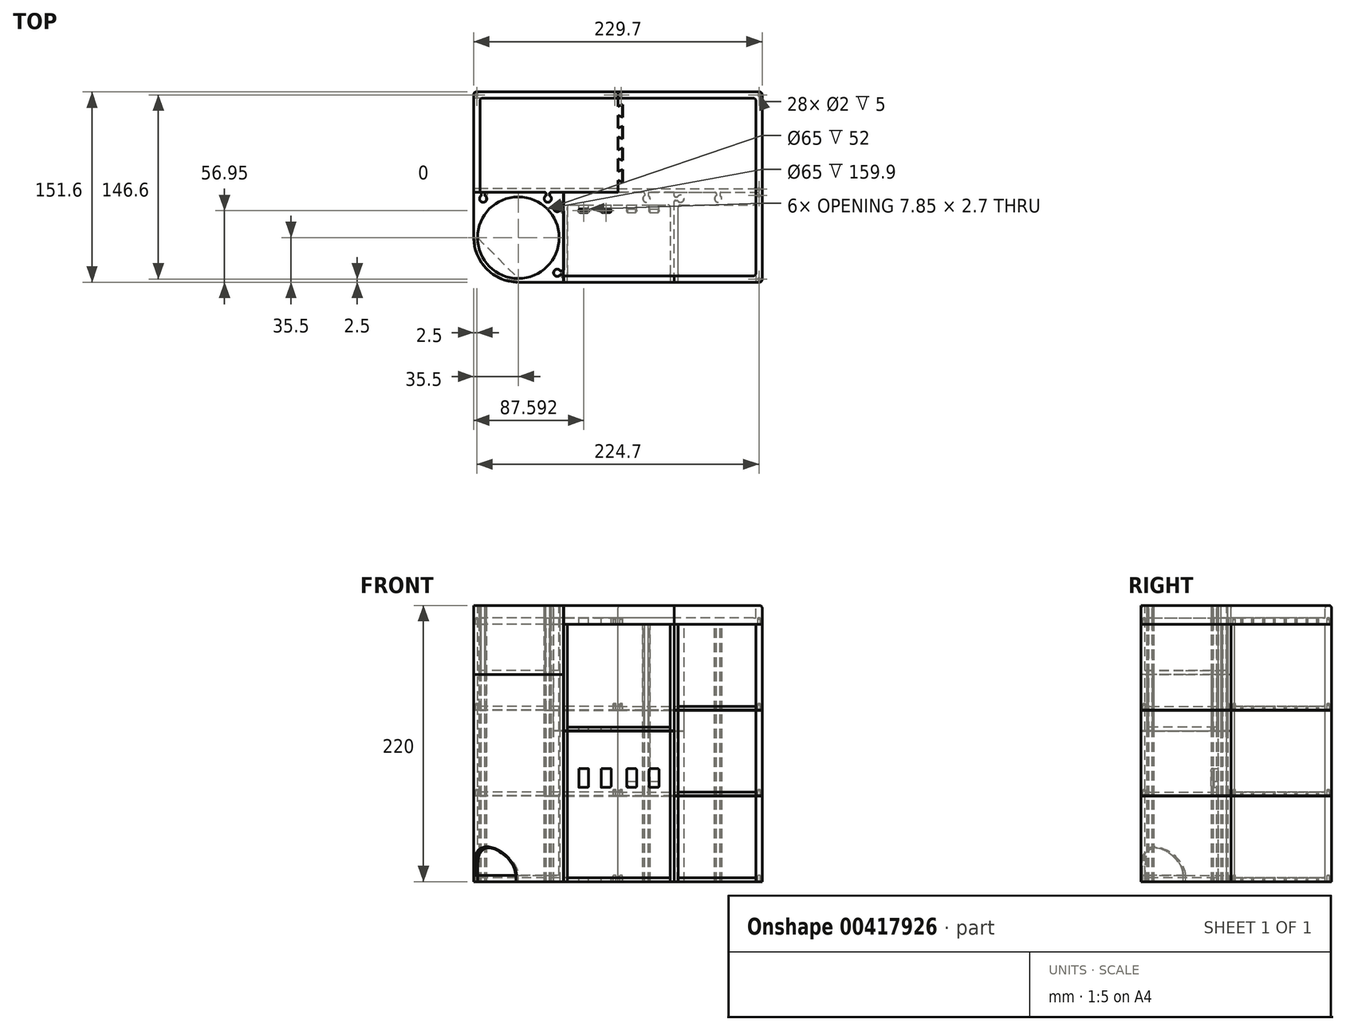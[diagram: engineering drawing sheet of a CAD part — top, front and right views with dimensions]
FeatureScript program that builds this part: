
annotation { "Feature Type Name" : "Feature", "Feature Type Description" : "" }
export const myFeature = defineFeature(function(context is Context, id is Id, definition is map)
    precondition{}
    {
        {
            var Q0;
            Q0=qCreatedBy(makeId("Top.planeOp"),FACE);
            var sketch = newSketch(context, id + "F0", { "sketchPlane" : qUnion([Q0])});
            skLineSegment(sketch, "E0", {"start": v(-2, 0) * mm, "end": v(-114.85, 0) * mm});
            skLineSegment(sketch, "E1", {"start": v(-114.85, 0) * mm, "end": v(-114.95, 0) * mm, "construction": true});
            skLineSegment(sketch, "E2", {"start": v(-114.95, 0) * mm, "end": v(-227.7, 0) * mm});
            skLineSegment(sketch, "E3", {"start": v(0, -2) * mm, "end": v(0, -80) * mm});
            skLineSegment(sketch, "E4", {"start": v(0, -80) * mm, "end": v(0, -80.1) * mm});
            skLineSegment(sketch, "E5", {"start": v(0, -80.1) * mm, "end": v(0, -149.6) * mm});
            skLineSegment(sketch, "E6", {"start": v(-2, -151.6) * mm, "end": v(-70, -151.6) * mm});
            skLineSegment(sketch, "E7", {"start": v(-70, -151.6) * mm, "end": v(-70.1, -151.6) * mm});
            skLineSegment(sketch, "E8", {"start": v(-70.1, -151.6) * mm, "end": v(-158.1, -151.6) * mm});
            skLineSegment(sketch, "E9", {"start": v(-158.1, -151.6) * mm, "end": v(-158.1, -146.26) * mm});
            skLineSegment(sketch, "E10", {"start": v(-70, -151.6) * mm, "end": v(-70, -87.55) * mm});
            skLineSegment(sketch, "E11", {"start": v(-70, -80.1) * mm, "end": v(-37.5, -80.1) * mm});
            skLineSegment(sketch, "E12", {"start": v(-70.1, -151.6) * mm, "end": v(-70.1, -87.21) * mm});
            skLineSegment(sketch, "E13", {"start": v(-70.1, -80.1) * mm, "end": v(-89.6, -80.1) * mm});
            skLineSegment(sketch, "E14", {"start": v(-70.1, -151.6) * mm, "end": v(-70, -151.6) * mm});
            skLineSegment(sketch, "E15", {"start": v(-158.1, -151.6) * mm, "end": v(-158.2, -151.6) * mm, "construction": true});
            skLineSegment(sketch, "E16", {"start": v(-158.2, -151.6) * mm, "end": v(-194.2, -151.6) * mm});
            skLineSegment(sketch, "E17", {"start": v(-194.2, -151.6) * mm, "end": v(-194.2, -116.1) * mm, "construction": true});
            skLineSegment(sketch, "E18", {"start": v(-194.2, -116.1) * mm, "end": v(-229.7, -116.1) * mm, "construction": true});
            skCircle(sketch, "E19", {"center": v(-194.2, -116.1) * mm, "radius": 32.5 * mm});
            skArc(sketch, "E20", {"start": v(-229.7, -116.1) * mm, "mid": v(-219.3, -141.2) * mm, "end": v(-194.2, -151.6) * mm});
            skLineSegment(sketch, "E21", {"start": v(-194.2, -151.6) * mm, "end": v(-194.2, -148.6) * mm});
            skLineSegment(sketch, "E22", {"start": v(-229.7, -116.1) * mm, "end": v(-226.7, -116.1) * mm});
            skLineSegment(sketch, "E23", {"start": v(-226.7, -116.1) * mm, "end": v(-194.2, -148.6) * mm});
            skLineSegment(sketch, "E24", {"start": v(-229.7, -116.1) * mm, "end": v(-229.7, -80.1) * mm});
            skLineSegment(sketch, "E25", {"start": v(-229.7, -80.1) * mm, "end": v(-224.7, -80.1) * mm});
            skLineSegment(sketch, "E26", {"start": v(-158.2, -80.1) * mm, "end": v(-158.2, -90.1) * mm});
            skLineSegment(sketch, "E27", {"start": v(-229.7, -80.1) * mm, "end": v(-229.7, -80) * mm, "construction": true});
            skLineSegment(sketch, "E28", {"start": v(-229.7, -80) * mm, "end": v(-229.7, -2) * mm});
            skLineSegment(sketch, "E29", {"start": v(-114.85, -80) * mm, "end": v(-94.26, -80) * mm});
            skLineSegment(sketch, "E30", {"start": v(-220.7, -81.1) * mm, "end": v(-220.7, -82.6) * mm});
            skLineSegment(sketch, "E31", {"start": v(-220.7, -82.6) * mm, "end": v(-222.2, -82.6) * mm, "construction": true});
            skLineSegment(sketch, "E32", {"start": v(-222.2, -82.6) * mm, "end": v(-222.2, -80.1) * mm, "construction": true});
            skLineSegment(sketch, "E33", {"start": v(-222.2, -82.6) * mm, "end": v(-222.2, -85.1) * mm, "construction": true});
            skArc(sketch, "E34", {"start": v(-220.7, -82.6) * mm, "mid": v(-219.4, -85.88) * mm, "end": v(-222.2, -88.02) * mm});
            skArc(sketch, "E35", {"start": v(-220.7, -81.1) * mm, "mid": v(-220.4, -80.4) * mm, "end": v(-219.7, -80.1) * mm});
            skPoint(sketch, "E36.orphan", {"position": v(-220.7, -80.1) * mm});
            skArc(sketch, "E37.MirrorCS", {"start": v(-223.7, -81.1) * mm, "mid": v(-224, -80.4) * mm, "end": v(-224.7, -80.1) * mm});
            skLineSegment(sketch, "E38.MirrorCS", {"start": v(-223.7, -81.1) * mm, "end": v(-223.7, -82.6) * mm});
            skArc(sketch, "E39.MirrorCS", {"start": v(-223.7, -82.6) * mm, "mid": v(-225, -85.88) * mm, "end": v(-222.2, -88.02) * mm});
            skArc(sketch, "E40.0", {"start": v(-223.55, -81.1) * mm, "mid": v(-223.78, -80.42) * mm, "end": v(-224.36, -80) * mm});
            skLineSegment(sketch, "E40.1", {"start": v(-223.55, -81.1) * mm, "end": v(-223.55, -82.69) * mm});
            skArc(sketch, "E40.2", {"start": v(-220.85, -81.1) * mm, "mid": v(-220.62, -80.42) * mm, "end": v(-220.04, -80) * mm});
            skLineSegment(sketch, "E40.3", {"start": v(-220.85, -81.1) * mm, "end": v(-220.85, -82.69) * mm});
            skArc(sketch, "E40.4", {"start": v(-220.85, -82.69) * mm, "mid": v(-219.52, -85.8) * mm, "end": v(-222.2, -87.87) * mm});
            skArc(sketch, "E40.5", {"start": v(-223.55, -82.69) * mm, "mid": v(-224.88, -85.8) * mm, "end": v(-222.2, -87.87) * mm});
            skLineSegment(sketch, "E41.trimOffspring", {"start": v(-224.13, -80.1) * mm, "end": v(-220.27, -80.1) * mm, "construction": true});
            skLineSegment(sketch, "E42.trimOffspring", {"start": v(-219.7, -80.1) * mm, "end": v(-173.2, -80.1) * mm});
            skLineSegment(sketch, "E43.trimOffspring", {"start": v(-224.36, -80) * mm, "end": v(-229.7, -80) * mm});
            skLineSegment(sketch, "E44", {"start": v(-169.2, -81.1) * mm, "end": v(-169.2, -82.6) * mm});
            skLineSegment(sketch, "E45", {"start": v(-169.2, -82.6) * mm, "end": v(-170.7, -82.6) * mm, "construction": true});
            skLineSegment(sketch, "E46", {"start": v(-170.7, -82.6) * mm, "end": v(-170.7, -80.1) * mm, "construction": true});
            skLineSegment(sketch, "E47", {"start": v(-170.7, -82.6) * mm, "end": v(-170.7, -85.1) * mm, "construction": true});
            skArc(sketch, "E48", {"start": v(-169.2, -82.6) * mm, "mid": v(-167.9, -85.88) * mm, "end": v(-170.7, -88.02) * mm});
            skArc(sketch, "E49", {"start": v(-169.2, -81.1) * mm, "mid": v(-168.9, -80.4) * mm, "end": v(-168.2, -80.1) * mm});
            skPoint(sketch, "E50.orphan", {"position": v(-169.2, -80.1) * mm});
            skArc(sketch, "E51.MirrorCS", {"start": v(-172.2, -81.1) * mm, "mid": v(-172.5, -80.4) * mm, "end": v(-173.2, -80.1) * mm});
            skLineSegment(sketch, "E52.MirrorCS", {"start": v(-172.2, -81.1) * mm, "end": v(-172.2, -82.6) * mm});
            skArc(sketch, "E53.MirrorCS", {"start": v(-172.2, -82.6) * mm, "mid": v(-173.5, -85.88) * mm, "end": v(-170.7, -88.02) * mm});
            skArc(sketch, "E54.0", {"start": v(-172.05, -81.1) * mm, "mid": v(-172.28, -80.42) * mm, "end": v(-172.86, -80) * mm});
            skLineSegment(sketch, "E54.1", {"start": v(-172.05, -81.1) * mm, "end": v(-172.05, -82.69) * mm});
            skArc(sketch, "E54.2", {"start": v(-169.35, -81.1) * mm, "mid": v(-169.12, -80.42) * mm, "end": v(-168.54, -80) * mm});
            skLineSegment(sketch, "E54.3", {"start": v(-169.35, -81.1) * mm, "end": v(-169.35, -82.69) * mm});
            skArc(sketch, "E54.4", {"start": v(-169.35, -82.69) * mm, "mid": v(-168.02, -85.8) * mm, "end": v(-170.7, -87.87) * mm});
            skArc(sketch, "E54.5", {"start": v(-172.05, -82.69) * mm, "mid": v(-173.38, -85.8) * mm, "end": v(-170.7, -87.87) * mm});
            skLineSegment(sketch, "E55.trimOffspring", {"start": v(-172.63, -80.1) * mm, "end": v(-168.77, -80.1) * mm, "construction": true});
            skLineSegment(sketch, "E56.trimOffspring", {"start": v(-168.2, -80.1) * mm, "end": v(-158.2, -80.1) * mm});
            skLineSegment(sketch, "E57.trimOffspring", {"start": v(-172.86, -80) * mm, "end": v(-220.04, -80) * mm});
            skLineSegment(sketch, "E58", {"start": v(-159.2, -94.1) * mm, "end": v(-160.7, -94.1) * mm});
            skLineSegment(sketch, "E59", {"start": v(-160.7, -94.1) * mm, "end": v(-160.7, -92.6) * mm, "construction": true});
            skLineSegment(sketch, "E60", {"start": v(-160.7, -92.6) * mm, "end": v(-158.2, -92.6) * mm, "construction": true});
            skLineSegment(sketch, "E61", {"start": v(-160.7, -92.6) * mm, "end": v(-163.2, -92.6) * mm, "construction": true});
            skArc(sketch, "E62", {"start": v(-160.7, -94.1) * mm, "mid": v(-163.98, -95.4) * mm, "end": v(-166.12, -92.6) * mm});
            skArc(sketch, "E63", {"start": v(-159.2, -94.1) * mm, "mid": v(-158.5, -94.4) * mm, "end": v(-158.2, -95.1) * mm});
            skPoint(sketch, "E64.orphan", {"position": v(-158.2, -94.1) * mm});
            skArc(sketch, "E65.MirrorCS", {"start": v(-159.2, -91.1) * mm, "mid": v(-158.5, -90.8) * mm, "end": v(-158.2, -90.1) * mm});
            skLineSegment(sketch, "E66.MirrorCS", {"start": v(-159.2, -91.1) * mm, "end": v(-160.7, -91.1) * mm});
            skArc(sketch, "E67.MirrorCS", {"start": v(-160.7, -91.1) * mm, "mid": v(-163.98, -89.8) * mm, "end": v(-166.12, -92.6) * mm});
            skArc(sketch, "E68.0", {"start": v(-159.2, -91.25) * mm, "mid": v(-158.52, -91.02) * mm, "end": v(-158.1, -90.44) * mm});
            skLineSegment(sketch, "E68.1", {"start": v(-159.2, -91.25) * mm, "end": v(-160.79, -91.25) * mm});
            skArc(sketch, "E68.2", {"start": v(-159.2, -93.95) * mm, "mid": v(-158.52, -94.18) * mm, "end": v(-158.1, -94.76) * mm});
            skLineSegment(sketch, "E68.3", {"start": v(-159.2, -93.95) * mm, "end": v(-160.79, -93.95) * mm});
            skArc(sketch, "E68.4", {"start": v(-160.79, -93.95) * mm, "mid": v(-163.9, -95.28) * mm, "end": v(-165.97, -92.6) * mm});
            skArc(sketch, "E68.5", {"start": v(-160.79, -91.25) * mm, "mid": v(-163.9, -89.92) * mm, "end": v(-165.97, -92.6) * mm});
            skLineSegment(sketch, "E69.trimOffspring", {"start": v(-158.2, -90.67) * mm, "end": v(-158.2, -94.53) * mm, "construction": true});
            skLineSegment(sketch, "E70.trimOffspring", {"start": v(-158.1, -90.44) * mm, "end": v(-158.1, -80.1) * mm});
            skLineSegment(sketch, "E71.trimOffspring", {"start": v(-158.2, -95.1) * mm, "end": v(-158.2, -141.6) * mm});
            skLineSegment(sketch, "E72", {"start": v(-159.2, -145.6) * mm, "end": v(-160.7, -145.6) * mm});
            skLineSegment(sketch, "E73", {"start": v(-160.7, -145.6) * mm, "end": v(-160.7, -144.1) * mm, "construction": true});
            skLineSegment(sketch, "E74", {"start": v(-160.7, -144.1) * mm, "end": v(-158.2, -144.1) * mm, "construction": true});
            skLineSegment(sketch, "E75", {"start": v(-160.7, -144.1) * mm, "end": v(-163.2, -144.1) * mm, "construction": true});
            skArc(sketch, "E76", {"start": v(-160.7, -145.6) * mm, "mid": v(-163.98, -146.9) * mm, "end": v(-166.12, -144.1) * mm});
            skArc(sketch, "E77", {"start": v(-159.2, -145.6) * mm, "mid": v(-158.5, -145.9) * mm, "end": v(-158.2, -146.6) * mm});
            skPoint(sketch, "E78.orphan", {"position": v(-158.2, -145.6) * mm});
            skArc(sketch, "E79.MirrorCS", {"start": v(-159.2, -142.6) * mm, "mid": v(-158.5, -142.3) * mm, "end": v(-158.2, -141.6) * mm});
            skLineSegment(sketch, "E80.MirrorCS", {"start": v(-159.2, -142.6) * mm, "end": v(-160.7, -142.6) * mm});
            skArc(sketch, "E81.MirrorCS", {"start": v(-160.7, -142.6) * mm, "mid": v(-163.98, -141.3) * mm, "end": v(-166.12, -144.1) * mm});
            skArc(sketch, "E82.0", {"start": v(-159.2, -142.75) * mm, "mid": v(-158.52, -142.52) * mm, "end": v(-158.1, -141.94) * mm});
            skLineSegment(sketch, "E82.1", {"start": v(-159.2, -142.75) * mm, "end": v(-160.79, -142.75) * mm});
            skArc(sketch, "E82.2", {"start": v(-159.2, -145.45) * mm, "mid": v(-158.52, -145.68) * mm, "end": v(-158.1, -146.26) * mm});
            skLineSegment(sketch, "E82.3", {"start": v(-159.2, -145.45) * mm, "end": v(-160.79, -145.45) * mm});
            skArc(sketch, "E82.4", {"start": v(-160.79, -145.45) * mm, "mid": v(-163.9, -146.78) * mm, "end": v(-165.97, -144.1) * mm});
            skArc(sketch, "E82.5", {"start": v(-160.79, -142.75) * mm, "mid": v(-163.9, -141.42) * mm, "end": v(-165.97, -144.1) * mm});
            skLineSegment(sketch, "E83.trimOffspring", {"start": v(-158.2, -142.17) * mm, "end": v(-158.2, -146.03) * mm, "construction": true});
            skLineSegment(sketch, "E84.trimOffspring", {"start": v(-158.1, -141.94) * mm, "end": v(-158.1, -94.76) * mm});
            skLineSegment(sketch, "E85.trimOffspring", {"start": v(-158.2, -146.6) * mm, "end": v(-158.2, -151.6) * mm});
            skLineSegment(sketch, "E86.0", {"start": v(-114.95, -5) * mm, "end": v(-117.95, -5) * mm});
            skLineSegment(sketch, "E87.0", {"start": v(-111.85, -5) * mm, "end": v(-114.85, -5) * mm});
            skLineSegment(sketch, "E88.0", {"start": v(-5, -77) * mm, "end": v(-5, -80) * mm});
            skLineSegment(sketch, "E89.0", {"start": v(-114.85, -77) * mm, "end": v(-7, -77) * mm});
            skLineSegment(sketch, "E90", {"start": v(-158.1, -80.1) * mm, "end": v(-158.1, -80) * mm});
            skLineSegment(sketch, "E91", {"start": v(-114.85, 0) * mm, "end": v(-114.85, -5) * mm});
            skLineSegment(sketch, "E92", {"start": v(-114.95, 0) * mm, "end": v(-114.95, -5) * mm});
            skLineSegment(sketch, "E93", {"start": v(-168.54, -80) * mm, "end": v(-158.2, -80) * mm});
            skLineSegment(sketch, "E94", {"start": v(-158.1, -80) * mm, "end": v(-114.95, -80) * mm});
            skLineSegment(sketch, "E95", {"start": v(-114.85, -77) * mm, "end": v(-114.85, -80) * mm});
            skLineSegment(sketch, "E96", {"start": v(-114.95, -77) * mm, "end": v(-222.7, -77) * mm});
            skLineSegment(sketch, "E97", {"start": v(-114.85, -5) * mm, "end": v(-114.85, -11.47) * mm});
            skLineSegment(sketch, "E98", {"start": v(-114.85, -11.47) * mm, "end": v(-111.1, -10.1) * mm});
            skLineSegment(sketch, "E99", {"start": v(-111.1, -10.1) * mm, "end": v(-111.1, -20.1) * mm});
            skLineSegment(sketch, "E100", {"start": v(-111.1, -20.1) * mm, "end": v(-114.85, -18.74) * mm});
            skLineSegment(sketch, "E101", {"start": v(-114.85, -18.74) * mm, "end": v(-114.85, -28.74) * mm});
            skLineSegment(sketch, "E102", {"start": v(-114.85, -28.74) * mm, "end": v(-111.1, -27.37) * mm});
            skLineSegment(sketch, "E103", {"start": v(-111.1, -27.37) * mm, "end": v(-111.1, -37.37) * mm});
            skLineSegment(sketch, "E104", {"start": v(-111.1, -37.37) * mm, "end": v(-114.85, -36) * mm});
            skLineSegment(sketch, "E105", {"start": v(-114.85, -36) * mm, "end": v(-114.85, -46) * mm});
            skLineSegment(sketch, "E106", {"start": v(-114.85, -46) * mm, "end": v(-111.1, -44.63) * mm});
            skLineSegment(sketch, "E107", {"start": v(-111.1, -44.63) * mm, "end": v(-111.1, -54.63) * mm});
            skLineSegment(sketch, "E108", {"start": v(-111.1, -54.63) * mm, "end": v(-114.85, -53.26) * mm});
            skLineSegment(sketch, "E109", {"start": v(-114.85, -53.26) * mm, "end": v(-114.85, -63.26) * mm});
            skLineSegment(sketch, "E110", {"start": v(-114.85, -63.26) * mm, "end": v(-111.1, -61.9) * mm});
            skLineSegment(sketch, "E111", {"start": v(-111.1, -61.9) * mm, "end": v(-111.1, -71.9) * mm});
            skLineSegment(sketch, "E112", {"start": v(-111.1, -71.9) * mm, "end": v(-114.85, -70.53) * mm});
            skLineSegment(sketch, "E113", {"start": v(-114.85, -70.53) * mm, "end": v(-114.85, -77) * mm});
            skLineSegment(sketch, "E114.0", {"start": v(-114.95, -70.38) * mm, "end": v(-114.95, -77) * mm});
            skLineSegment(sketch, "E114.1", {"start": v(-111.2, -71.75) * mm, "end": v(-114.95, -70.38) * mm});
            skLineSegment(sketch, "E114.2", {"start": v(-111.2, -62.04) * mm, "end": v(-111.2, -71.75) * mm});
            skLineSegment(sketch, "E114.3", {"start": v(-114.95, -63.4) * mm, "end": v(-111.2, -62.04) * mm});
            skLineSegment(sketch, "E114.4", {"start": v(-114.95, -53.12) * mm, "end": v(-114.95, -63.4) * mm});
            skLineSegment(sketch, "E114.5", {"start": v(-111.2, -54.49) * mm, "end": v(-114.95, -53.12) * mm});
            skLineSegment(sketch, "E114.6", {"start": v(-111.2, -44.77) * mm, "end": v(-111.2, -54.49) * mm});
            skLineSegment(sketch, "E114.7", {"start": v(-111.2, -19.96) * mm, "end": v(-114.95, -18.6) * mm});
            skLineSegment(sketch, "E114.8", {"start": v(-111.2, -10.25) * mm, "end": v(-111.2, -19.96) * mm});
            skLineSegment(sketch, "E114.9", {"start": v(-114.95, -11.62) * mm, "end": v(-111.2, -10.25) * mm});
            skLineSegment(sketch, "E114.10", {"start": v(-114.95, -5) * mm, "end": v(-114.95, -11.62) * mm});
            skLineSegment(sketch, "E114.11", {"start": v(-114.95, -18.6) * mm, "end": v(-114.95, -28.88) * mm});
            skLineSegment(sketch, "E114.12", {"start": v(-114.95, -28.88) * mm, "end": v(-111.2, -27.51) * mm});
            skLineSegment(sketch, "E114.13", {"start": v(-111.2, -27.51) * mm, "end": v(-111.2, -37.23) * mm});
            skLineSegment(sketch, "E114.14", {"start": v(-111.2, -37.23) * mm, "end": v(-114.95, -35.86) * mm});
            skLineSegment(sketch, "E114.15", {"start": v(-114.95, -35.86) * mm, "end": v(-114.95, -46.14) * mm});
            skLineSegment(sketch, "E114.16", {"start": v(-114.95, -46.14) * mm, "end": v(-111.2, -44.77) * mm});
            skLineSegment(sketch, "E115", {"start": v(-158.2, -80) * mm, "end": v(-158.1, -80) * mm});
            skLineSegment(sketch, "E116.1", {"start": v(-153.1, -90) * mm, "end": v(-75.1, -90) * mm});
            skLineSegment(sketch, "E117.bottom", {"start": v(-107.02, -93.3) * mm, "end": v(-100.87, -93.3) * mm});
            skLineSegment(sketch, "E117.top", {"start": v(-107.02, -96) * mm, "end": v(-100.87, -96) * mm});
            skLineSegment(sketch, "E117.left", {"start": v(-107.87, -94.15) * mm, "end": v(-107.87, -95.15) * mm});
            skLineSegment(sketch, "E117.right", {"start": v(-100.02, -94.15) * mm, "end": v(-100.02, -95.15) * mm});
            skPoint(sketch, "E118.visualSharp", {"position": v(-100.02, -96) * mm});
            skArc(sketch, "E118.filletArc", {"start": v(-100.87, -96) * mm, "mid": v(-100.27, -95.75) * mm, "end": v(-100.02, -95.15) * mm});
            skPoint(sketch, "E119.visualSharp", {"position": v(-100.02, -93.3) * mm});
            skArc(sketch, "E119.filletArc", {"start": v(-100.02, -94.15) * mm, "mid": v(-100.27, -93.55) * mm, "end": v(-100.87, -93.3) * mm});
            skPoint(sketch, "E120.visualSharp", {"position": v(-107.87, -93.3) * mm});
            skArc(sketch, "E120.filletArc", {"start": v(-107.02, -93.3) * mm, "mid": v(-107.62, -93.55) * mm, "end": v(-107.87, -94.15) * mm});
            skPoint(sketch, "E121.visualSharp", {"position": v(-107.87, -96) * mm});
            skArc(sketch, "E121.filletArc", {"start": v(-107.87, -95.15) * mm, "mid": v(-107.62, -95.75) * mm, "end": v(-107.02, -96) * mm});
            skLineSegment(sketch, "E122.bottom", {"start": v(-89.17, -93.3) * mm, "end": v(-83.02, -93.3) * mm});
            skLineSegment(sketch, "E122.top", {"start": v(-89.17, -96) * mm, "end": v(-83.02, -96) * mm});
            skLineSegment(sketch, "E122.left", {"start": v(-90.02, -94.15) * mm, "end": v(-90.02, -95.15) * mm});
            skLineSegment(sketch, "E122.right", {"start": v(-82.17, -94.15) * mm, "end": v(-82.17, -95.15) * mm});
            skPoint(sketch, "E123.visualSharp", {"position": v(-82.17, -96) * mm});
            skArc(sketch, "E123.filletArc", {"start": v(-83.02, -96) * mm, "mid": v(-82.42, -95.75) * mm, "end": v(-82.17, -95.15) * mm});
            skPoint(sketch, "E124.visualSharp", {"position": v(-82.17, -93.3) * mm});
            skArc(sketch, "E124.filletArc", {"start": v(-82.17, -94.15) * mm, "mid": v(-82.42, -93.55) * mm, "end": v(-83.02, -93.3) * mm});
            skPoint(sketch, "E125.visualSharp", {"position": v(-90.02, -93.3) * mm});
            skArc(sketch, "E125.filletArc", {"start": v(-89.17, -93.3) * mm, "mid": v(-89.77, -93.55) * mm, "end": v(-90.02, -94.15) * mm});
            skPoint(sketch, "E126.visualSharp", {"position": v(-90.02, -96) * mm});
            skArc(sketch, "E126.filletArc", {"start": v(-90.02, -95.15) * mm, "mid": v(-89.77, -95.75) * mm, "end": v(-89.17, -96) * mm});
            skLineSegment(sketch, "E127", {"start": v(-107.87, -94.15) * mm, "end": v(-107.87, -90) * mm});
            skLineSegment(sketch, "E128", {"start": v(-100.02, -94.15) * mm, "end": v(-100.02, -90) * mm});
            skLineSegment(sketch, "E129", {"start": v(-90.02, -94.15) * mm, "end": v(-90.02, -90) * mm});
            skLineSegment(sketch, "E130", {"start": v(-82.17, -94.15) * mm, "end": v(-82.17, -90) * mm});
            skLineSegment(sketch, "E131", {"start": v(-155.1, -92) * mm, "end": v(-155.1, -144.6) * mm});
            skLineSegment(sketch, "E132", {"start": v(-73.1, -92) * mm, "end": v(-73.1, -144.6) * mm});
            skLineSegment(sketch, "E133", {"start": v(-114.1, -90) * mm, "end": v(-114.1, -102.22) * mm, "construction": true});
            skLineSegment(sketch, "E134.MirrorCS", {"start": v(-120.33, -94.15) * mm, "end": v(-120.33, -90) * mm});
            skArc(sketch, "E135.MirrorCS", {"start": v(-121.18, -93.3) * mm, "mid": v(-120.58, -93.55) * mm, "end": v(-120.33, -94.15) * mm});
            skLineSegment(sketch, "E136.MirrorCS", {"start": v(-120.33, -94.15) * mm, "end": v(-120.33, -95.15) * mm});
            skArc(sketch, "E137.MirrorCS", {"start": v(-120.33, -95.15) * mm, "mid": v(-120.58, -95.75) * mm, "end": v(-121.18, -96) * mm});
            skLineSegment(sketch, "E138.MirrorCS", {"start": v(-121.18, -96) * mm, "end": v(-127.33, -96) * mm});
            skLineSegment(sketch, "E139.MirrorCS", {"start": v(-121.18, -93.3) * mm, "end": v(-127.33, -93.3) * mm});
            skArc(sketch, "E140.MirrorCS", {"start": v(-128.18, -94.15) * mm, "mid": v(-127.93, -93.55) * mm, "end": v(-127.33, -93.3) * mm});
            skLineSegment(sketch, "E141.MirrorCS", {"start": v(-128.18, -94.15) * mm, "end": v(-128.18, -95.15) * mm});
            skArc(sketch, "E142.MirrorCS", {"start": v(-127.33, -96) * mm, "mid": v(-127.93, -95.75) * mm, "end": v(-128.18, -95.15) * mm});
            skLineSegment(sketch, "E143.MirrorCS", {"start": v(-128.18, -94.15) * mm, "end": v(-128.18, -90) * mm});
            skLineSegment(sketch, "E144.MirrorCS", {"start": v(-138.18, -94.15) * mm, "end": v(-138.18, -90) * mm});
            skArc(sketch, "E145.MirrorCS", {"start": v(-139.03, -93.3) * mm, "mid": v(-138.43, -93.55) * mm, "end": v(-138.18, -94.15) * mm});
            skLineSegment(sketch, "E146.MirrorCS", {"start": v(-138.18, -94.15) * mm, "end": v(-138.18, -95.15) * mm});
            skArc(sketch, "E147.MirrorCS", {"start": v(-138.18, -95.15) * mm, "mid": v(-138.43, -95.75) * mm, "end": v(-139.03, -96) * mm});
            skLineSegment(sketch, "E148.MirrorCS", {"start": v(-139.03, -96) * mm, "end": v(-145.18, -96) * mm});
            skArc(sketch, "E149.MirrorCS", {"start": v(-145.18, -96) * mm, "mid": v(-145.78, -95.75) * mm, "end": v(-146.03, -95.15) * mm});
            skLineSegment(sketch, "E150.MirrorCS", {"start": v(-146.03, -94.15) * mm, "end": v(-146.03, -95.15) * mm});
            skArc(sketch, "E151.MirrorCS", {"start": v(-146.03, -94.15) * mm, "mid": v(-145.78, -93.55) * mm, "end": v(-145.18, -93.3) * mm});
            skLineSegment(sketch, "E152.MirrorCS", {"start": v(-139.03, -93.3) * mm, "end": v(-145.18, -93.3) * mm});
            skLineSegment(sketch, "E153.MirrorCS", {"start": v(-146.03, -94.15) * mm, "end": v(-146.03, -90) * mm});
            skLineSegment(sketch, "E154", {"start": v(-114.95, -77) * mm, "end": v(-114.95, -80) * mm});
            skLineSegment(sketch, "E155.0", {"start": v(-5, -80.1) * mm, "end": v(-5, -83.1) * mm});
            skLineSegment(sketch, "E156.trimOffspring", {"start": v(-7, -146.6) * mm, "end": v(-65, -146.6) * mm});
            skLineSegment(sketch, "E157.0", {"start": v(-65, -90) * mm, "end": v(-7, -90) * mm});
            skLineSegment(sketch, "E158.0", {"start": v(-70.1, -146.6) * mm, "end": v(-71.1, -146.6) * mm});
            skLineSegment(sketch, "E159", {"start": v(-69, -83.55) * mm, "end": v(-67.5, -83.55) * mm});
            skLineSegment(sketch, "E160", {"start": v(-67.5, -83.55) * mm, "end": v(-67.5, -85.05) * mm, "construction": true});
            skLineSegment(sketch, "E161", {"start": v(-67.5, -85.05) * mm, "end": v(-70, -85.05) * mm, "construction": true});
            skLineSegment(sketch, "E162", {"start": v(-67.5, -85.05) * mm, "end": v(-65, -85.05) * mm, "construction": true});
            skArc(sketch, "E163", {"start": v(-67.5, -83.55) * mm, "mid": v(-64.22, -82.24) * mm, "end": v(-62.08, -85.05) * mm});
            skArc(sketch, "E164", {"start": v(-69, -83.55) * mm, "mid": v(-69.7, -83.26) * mm, "end": v(-70, -82.55) * mm});
            skPoint(sketch, "E165.orphan", {"position": v(-70, -83.55) * mm});
            skArc(sketch, "E166.MirrorCS", {"start": v(-69, -86.55) * mm, "mid": v(-69.7, -86.84) * mm, "end": v(-70, -87.55) * mm});
            skLineSegment(sketch, "E167.MirrorCS", {"start": v(-69, -86.55) * mm, "end": v(-67.5, -86.55) * mm});
            skArc(sketch, "E168.MirrorCS", {"start": v(-67.5, -86.55) * mm, "mid": v(-64.22, -87.86) * mm, "end": v(-62.08, -85.05) * mm});
            skArc(sketch, "E169.0", {"start": v(-69, -86.4) * mm, "mid": v(-69.68, -86.63) * mm, "end": v(-70.1, -87.21) * mm});
            skLineSegment(sketch, "E169.1", {"start": v(-69, -86.4) * mm, "end": v(-67.41, -86.4) * mm});
            skArc(sketch, "E169.2", {"start": v(-69, -83.7) * mm, "mid": v(-69.68, -83.47) * mm, "end": v(-70.1, -82.89) * mm});
            skLineSegment(sketch, "E169.3", {"start": v(-69, -83.7) * mm, "end": v(-67.41, -83.7) * mm});
            skArc(sketch, "E169.4", {"start": v(-67.41, -83.7) * mm, "mid": v(-64.3, -82.37) * mm, "end": v(-62.23, -85.05) * mm});
            skArc(sketch, "E169.5", {"start": v(-67.41, -86.4) * mm, "mid": v(-64.3, -87.73) * mm, "end": v(-62.23, -85.05) * mm});
            skLineSegment(sketch, "E170.trimOffspring", {"start": v(-70.1, -82.89) * mm, "end": v(-70.1, -80.1) * mm});
            skLineSegment(sketch, "E171.trimOffspring", {"start": v(-70, -86.98) * mm, "end": v(-70, -83.12) * mm, "construction": true});
            skLineSegment(sketch, "E172.trimOffspring", {"start": v(-70, -82.55) * mm, "end": v(-70, -80.1) * mm});
            skLineSegment(sketch, "E173.trimOffspring", {"start": v(-67, -144.6) * mm, "end": v(-67, -92) * mm});
            skLineSegment(sketch, "E174.0", {"start": v(-224.7, -75) * mm, "end": v(-224.7, -7) * mm});
            skLineSegment(sketch, "E175", {"start": v(-33.5, -81.1) * mm, "end": v(-33.5, -82.6) * mm});
            skLineSegment(sketch, "E176", {"start": v(-33.5, -82.6) * mm, "end": v(-35, -82.6) * mm, "construction": true});
            skLineSegment(sketch, "E177", {"start": v(-35, -82.6) * mm, "end": v(-35, -80.1) * mm, "construction": true});
            skLineSegment(sketch, "E178", {"start": v(-35, -82.6) * mm, "end": v(-35, -85.1) * mm, "construction": true});
            skArc(sketch, "E179", {"start": v(-33.5, -82.6) * mm, "mid": v(-32.2, -85.88) * mm, "end": v(-35, -88.02) * mm});
            skArc(sketch, "E180", {"start": v(-33.5, -81.1) * mm, "mid": v(-33.2, -80.4) * mm, "end": v(-32.5, -80.1) * mm});
            skPoint(sketch, "E181.orphan", {"position": v(-33.5, -80.1) * mm});
            skArc(sketch, "E182.MirrorCS", {"start": v(-36.5, -81.1) * mm, "mid": v(-36.8, -80.4) * mm, "end": v(-37.5, -80.1) * mm});
            skLineSegment(sketch, "E183.MirrorCS", {"start": v(-36.5, -81.1) * mm, "end": v(-36.5, -82.6) * mm});
            skArc(sketch, "E184.MirrorCS", {"start": v(-36.5, -82.6) * mm, "mid": v(-37.8, -85.88) * mm, "end": v(-35, -88.02) * mm});
            skArc(sketch, "E185.0", {"start": v(-36.35, -81.1) * mm, "mid": v(-36.58, -80.42) * mm, "end": v(-37.16, -80) * mm});
            skLineSegment(sketch, "E185.1", {"start": v(-36.35, -81.1) * mm, "end": v(-36.35, -82.69) * mm});
            skArc(sketch, "E185.2", {"start": v(-33.65, -81.1) * mm, "mid": v(-33.42, -80.42) * mm, "end": v(-32.84, -80) * mm});
            skLineSegment(sketch, "E185.3", {"start": v(-33.65, -81.1) * mm, "end": v(-33.65, -82.69) * mm});
            skArc(sketch, "E185.4", {"start": v(-33.65, -82.69) * mm, "mid": v(-32.32, -85.8) * mm, "end": v(-35, -87.87) * mm});
            skArc(sketch, "E185.5", {"start": v(-36.35, -82.69) * mm, "mid": v(-37.68, -85.8) * mm, "end": v(-35, -87.87) * mm});
            skPoint(sketch, "E186", {"position": v(-35, -80.1) * mm});
            skPoint(sketch, "E187", {"position": v(-35, -80) * mm});
            skLineSegment(sketch, "E188.trimOffspring", {"start": v(-32.84, -80) * mm, "end": v(0, -80) * mm});
            skLineSegment(sketch, "E189.trimOffspring", {"start": v(-36.93, -80.1) * mm, "end": v(-33.07, -80.1) * mm, "construction": true});
            skLineSegment(sketch, "E190.trimOffspring", {"start": v(-32.5, -80.1) * mm, "end": v(0, -80.1) * mm});
            skLineSegment(sketch, "E191", {"start": v(-90.6, -81.1) * mm, "end": v(-90.6, -82.6) * mm});
            skLineSegment(sketch, "E192", {"start": v(-90.6, -82.6) * mm, "end": v(-92.1, -82.6) * mm, "construction": true});
            skLineSegment(sketch, "E193", {"start": v(-92.1, -82.6) * mm, "end": v(-92.1, -80.1) * mm, "construction": true});
            skLineSegment(sketch, "E194", {"start": v(-92.1, -82.6) * mm, "end": v(-92.1, -85.1) * mm, "construction": true});
            skArc(sketch, "E195", {"start": v(-90.6, -82.6) * mm, "mid": v(-89.3, -85.88) * mm, "end": v(-92.1, -88.02) * mm});
            skArc(sketch, "E196", {"start": v(-90.6, -81.1) * mm, "mid": v(-90.3, -80.4) * mm, "end": v(-89.6, -80.1) * mm});
            skPoint(sketch, "E197.orphan", {"position": v(-90.6, -80.1) * mm});
            skArc(sketch, "E198.MirrorCS", {"start": v(-93.6, -81.1) * mm, "mid": v(-93.9, -80.4) * mm, "end": v(-94.6, -80.1) * mm});
            skLineSegment(sketch, "E199.MirrorCS", {"start": v(-93.6, -81.1) * mm, "end": v(-93.6, -82.6) * mm});
            skArc(sketch, "E200.MirrorCS", {"start": v(-93.6, -82.6) * mm, "mid": v(-94.9, -85.88) * mm, "end": v(-92.1, -88.02) * mm});
            skArc(sketch, "E201.0", {"start": v(-93.45, -81.1) * mm, "mid": v(-93.68, -80.42) * mm, "end": v(-94.26, -80) * mm});
            skLineSegment(sketch, "E201.1", {"start": v(-93.45, -81.1) * mm, "end": v(-93.45, -82.69) * mm});
            skArc(sketch, "E201.2", {"start": v(-90.75, -81.1) * mm, "mid": v(-90.52, -80.42) * mm, "end": v(-89.94, -80) * mm});
            skLineSegment(sketch, "E201.3", {"start": v(-90.75, -81.1) * mm, "end": v(-90.75, -82.69) * mm});
            skArc(sketch, "E201.4", {"start": v(-90.75, -82.69) * mm, "mid": v(-89.42, -85.8) * mm, "end": v(-92.1, -87.87) * mm});
            skArc(sketch, "E201.5", {"start": v(-93.45, -82.69) * mm, "mid": v(-94.78, -85.8) * mm, "end": v(-92.1, -87.87) * mm});
            skPoint(sketch, "E202", {"position": v(-70.1, -80) * mm});
            skPoint(sketch, "E203", {"position": v(-92.1, -80.1) * mm});
            skLineSegment(sketch, "E204.trimOffspring", {"start": v(-89.94, -80) * mm, "end": v(-37.16, -80) * mm});
            skLineSegment(sketch, "E205.trimOffspring", {"start": v(-94.6, -80.1) * mm, "end": v(-158.1, -80.1) * mm});
            skLineSegment(sketch, "E206.trimOffspring", {"start": v(-90.17, -80.1) * mm, "end": v(-94.03, -80.1) * mm, "construction": true});
            skLineSegment(sketch, "E207", {"start": v(-224.7, -3) * mm, "end": v(-224.7, 0) * mm});
            skPoint(sketch, "E208", {"position": v(-227.2, 0) * mm});
            skCircle(sketch, "E209", {"center": v(-227.2, -2.5) * mm, "radius": 1 * mm});
            skPoint(sketch, "E209.centerSnap0", {"position": v(-224.7, -2.5) * mm});
            skPoint(sketch, "E210", {"position": v(-119.95, 0) * mm});
            skPoint(sketch, "E211", {"position": v(-109.85, 0) * mm});
            skPoint(sketch, "E212", {"position": v(-117.45, 0) * mm});
            skPoint(sketch, "E213", {"position": v(-112.35, 0) * mm});
            skLineSegment(sketch, "E214", {"start": v(-119.95, 0) * mm, "end": v(-119.95, -3) * mm});
            skLineSegment(sketch, "E215", {"start": v(-109.85, 0) * mm, "end": v(-109.85, -3) * mm});
            skCircle(sketch, "E216", {"center": v(-117.45, -2.5) * mm, "radius": 1 * mm});
            skCircle(sketch, "E217", {"center": v(-112.35, -2.5) * mm, "radius": 1 * mm});
            skCircle(sketch, "E218", {"center": v(-112.35, -2.5) * mm, "radius": 0.9 * mm});
            skCircle(sketch, "E219", {"center": v(-117.45, -2.5) * mm, "radius": 0.9 * mm});
            skCircle(sketch, "E220", {"center": v(-227.2, -2.5) * mm, "radius": 0.9 * mm});
            skLineSegment(sketch, "E221", {"start": v(-5, -3) * mm, "end": v(-5, 0) * mm});
            skLineSegment(sketch, "E222", {"start": v(-3, -5) * mm, "end": v(0, -5) * mm});
            skCircle(sketch, "E223", {"center": v(-2.5, -2.5) * mm, "radius": 1 * mm});
            skPoint(sketch, "E223.centerSnap0", {"position": v(-5, -2.5) * mm});
            skPoint(sketch, "E223.centerSnap1", {"position": v(-2.5, -5) * mm});
            skCircle(sketch, "E224", {"center": v(-2.5, -2.5) * mm, "radius": 0.9 * mm});
            skPoint(sketch, "E225", {"position": v(0, -77.5) * mm});
            skPoint(sketch, "E226", {"position": v(0, -75) * mm});
            skLineSegment(sketch, "E227", {"start": v(0, -75) * mm, "end": v(-3, -75) * mm});
            skCircle(sketch, "E228", {"center": v(-2.5, -77.5) * mm, "radius": 1 * mm});
            skPoint(sketch, "E228.centerSnap0", {"position": v(-2.5, -75) * mm});
            skCircle(sketch, "E229", {"center": v(-2.5, -77.5) * mm, "radius": 0.9 * mm});
            skPoint(sketch, "E230", {"position": v(0, -82.6) * mm});
            skPoint(sketch, "E231", {"position": v(0, -85.1) * mm});
            skLineSegment(sketch, "E232", {"start": v(0, -85.1) * mm, "end": v(-3, -85.1) * mm});
            skCircle(sketch, "E233", {"center": v(-2.5, -82.6) * mm, "radius": 1 * mm});
            skPoint(sketch, "E233.centerSnap0", {"position": v(-2.5, -85.1) * mm});
            skCircle(sketch, "E234", {"center": v(-2.5, -82.6) * mm, "radius": 0.9 * mm});
            skLineSegment(sketch, "E235", {"start": v(-3, -146.6) * mm, "end": v(0, -146.6) * mm});
            skLineSegment(sketch, "E236", {"start": v(-5, -148.6) * mm, "end": v(-5, -151.6) * mm});
            skCircle(sketch, "E237", {"center": v(-2.5, -149.1) * mm, "radius": 1 * mm});
            skPoint(sketch, "E237.centerSnap0", {"position": v(-5, -149.1) * mm});
            skPoint(sketch, "E237.centerSnap1", {"position": v(-2.5, -146.6) * mm});
            skCircle(sketch, "E238", {"center": v(-2.5, -149.1) * mm, "radius": 0.9 * mm});
            skLineSegment(sketch, "E239", {"start": v(-67, -148.6) * mm, "end": v(-67, -151.6) * mm});
            skLineSegment(sketch, "E240", {"start": v(-73.1, -148.6) * mm, "end": v(-73.1, -151.6) * mm});
            skLineSegment(sketch, "E241", {"start": v(-114.85, -80) * mm, "end": v(-114.85, -80.1) * mm});
            skLineSegment(sketch, "E242", {"start": v(-5, -80) * mm, "end": v(-5, -80.1) * mm});
            skLineSegment(sketch, "E243", {"start": v(-70.1, -146.6) * mm, "end": v(-70, -146.6) * mm});
            skPoint(sketch, "E244.visualSharp", {"position": v(0, 0) * mm});
            skArc(sketch, "E244.filletArc", {"start": v(0, -2) * mm, "mid": v(-0.59, -0.59) * mm, "end": v(-2, 0) * mm});
            skPoint(sketch, "E245.visualSharp", {"position": v(-5, -5) * mm});
            skArc(sketch, "E245.filletArc", {"start": v(-5, -7) * mm, "mid": v(-5.59, -5.59) * mm, "end": v(-7, -5) * mm});
            skPoint(sketch, "E246.visualSharp", {"position": v(-229.7, 0) * mm});
            skArc(sketch, "E246.filletArc", {"start": v(-227.7, 0) * mm, "mid": v(-229.11, -0.59) * mm, "end": v(-229.7, -2) * mm});
            skArc(sketch, "E247.filletArc", {"start": v(-222.7, -5) * mm, "mid": v(-224.11, -5.59) * mm, "end": v(-224.7, -7) * mm});
            skLineSegment(sketch, "E248", {"start": v(-226.7, -5) * mm, "end": v(-229.7, -5) * mm});
            skArc(sketch, "E249.filletArc", {"start": v(-224.7, -75) * mm, "mid": v(-224.11, -76.41) * mm, "end": v(-222.7, -77) * mm});
            skLineSegment(sketch, "E250", {"start": v(-229.7, -77) * mm, "end": v(-226.7, -77) * mm});
            skLineSegment(sketch, "E251", {"start": v(-224.7, -79) * mm, "end": v(-224.7, -80) * mm});
            skPoint(sketch, "E252.visualSharp", {"position": v(0, -151.6) * mm});
            skArc(sketch, "E252.filletArc", {"start": v(-2, -151.6) * mm, "mid": v(-0.59, -151.01) * mm, "end": v(0, -149.6) * mm});
            skPoint(sketch, "E253.visualSharp", {"position": v(-5, -146.6) * mm});
            skArc(sketch, "E253.filletArc", {"start": v(-7, -146.6) * mm, "mid": v(-5.59, -146.01) * mm, "end": v(-5, -144.6) * mm});
            skArc(sketch, "E254.filletArc", {"start": v(-3, -146.6) * mm, "mid": v(-4.41, -147.19) * mm, "end": v(-5, -148.6) * mm});
            skArc(sketch, "E255.filletArc", {"start": v(-5, -3) * mm, "mid": v(-4.41, -4.41) * mm, "end": v(-3, -5) * mm});
            skPoint(sketch, "E256.visualSharp", {"position": v(-224.7, -5) * mm});
            skArc(sketch, "E256.filletArc", {"start": v(-226.7, -5) * mm, "mid": v(-225.29, -4.41) * mm, "end": v(-224.7, -3) * mm});
            skPoint(sketch, "E257.visualSharp", {"position": v(-224.7, -77) * mm});
            skArc(sketch, "E257.filletArc", {"start": v(-224.7, -79) * mm, "mid": v(-225.29, -77.59) * mm, "end": v(-226.7, -77) * mm});
            skLineSegment(sketch, "E258", {"start": v(-114.95, -77) * mm, "end": v(-117.95, -77) * mm, "construction": true});
            skLineSegment(sketch, "E259", {"start": v(-114.85, -77) * mm, "end": v(-111.85, -77) * mm, "construction": true});
            skLineSegment(sketch, "E260", {"start": v(-119.95, -79) * mm, "end": v(-119.95, -80) * mm});
            skLineSegment(sketch, "E261", {"start": v(-109.85, -79) * mm, "end": v(-109.85, -80) * mm});
            skPoint(sketch, "E262.visualSharp", {"position": v(-119.95, -77) * mm});
            skArc(sketch, "E262.filletArc", {"start": v(-117.95, -77) * mm, "mid": v(-119.36, -77.59) * mm, "end": v(-119.95, -79) * mm});
            skPoint(sketch, "E263.visualSharp", {"position": v(-109.85, -77) * mm});
            skArc(sketch, "E263.filletArc", {"start": v(-109.85, -79) * mm, "mid": v(-110.44, -77.59) * mm, "end": v(-111.85, -77) * mm});
            skPoint(sketch, "E264.newPointA", {"position": v(-119.95, -5) * mm});
            skPoint(sketch, "E264.newPointB", {"position": v(-222.7, -5) * mm});
            skArc(sketch, "E264.filletArc", {"start": v(-119.95, -3) * mm, "mid": v(-119.36, -4.41) * mm, "end": v(-117.95, -5) * mm});
            skPoint(sketch, "E265.newPointA", {"position": v(-109.85, -5) * mm});
            skArc(sketch, "E265.filletArc", {"start": v(-111.85, -5) * mm, "mid": v(-110.44, -4.41) * mm, "end": v(-109.85, -3) * mm});
            skPoint(sketch, "E266", {"position": v(-114.95, -2.5) * mm});
            skLineSegment(sketch, "E267", {"start": v(-117.95, -5) * mm, "end": v(-222.7, -5) * mm});
            skLineSegment(sketch, "E268", {"start": v(-111.85, -5) * mm, "end": v(-7, -5) * mm});
            skPoint(sketch, "E269.newPointA", {"position": v(-5, -75) * mm});
            skArc(sketch, "E269.filletArc", {"start": v(-3, -75) * mm, "mid": v(-4.41, -75.59) * mm, "end": v(-5, -77) * mm});
            skLineSegment(sketch, "E270", {"start": v(-5, -75) * mm, "end": v(-5, -7) * mm});
            skPoint(sketch, "E271.visualSharp", {"position": v(-5, -77) * mm});
            skArc(sketch, "E271.filletArc", {"start": v(-7, -77) * mm, "mid": v(-5.59, -76.41) * mm, "end": v(-5, -75) * mm});
            skPoint(sketch, "E272.newPointB", {"position": v(-5, -85.1) * mm});
            skArc(sketch, "E272.filletArc", {"start": v(-5, -83.1) * mm, "mid": v(-4.41, -84.51) * mm, "end": v(-3, -85.1) * mm});
            skLineSegment(sketch, "E273", {"start": v(-5, -92) * mm, "end": v(-5, -144.6) * mm});
            skArc(sketch, "E274.filletArc", {"start": v(-5, -92) * mm, "mid": v(-5.59, -90.59) * mm, "end": v(-7, -90) * mm});
            skPoint(sketch, "E275.newPointA", {"position": v(-70, -90) * mm});
            skArc(sketch, "E275.filletArc", {"start": v(-65, -90) * mm, "mid": v(-66.41, -90.59) * mm, "end": v(-67, -92) * mm});
            skArc(sketch, "E276.filletArc", {"start": v(-67, -144.6) * mm, "mid": v(-66.41, -146.01) * mm, "end": v(-65, -146.6) * mm});
            skLineSegment(sketch, "E277", {"start": v(-69, -146.6) * mm, "end": v(-70, -146.6) * mm});
            skPoint(sketch, "E278.visualSharp", {"position": v(-67, -146.6) * mm});
            skArc(sketch, "E278.filletArc", {"start": v(-67, -148.6) * mm, "mid": v(-67.59, -147.19) * mm, "end": v(-69, -146.6) * mm});
            skArc(sketch, "E279.filletArc", {"start": v(-71.1, -146.6) * mm, "mid": v(-72.51, -147.19) * mm, "end": v(-73.1, -148.6) * mm});
            skLineSegment(sketch, "E280", {"start": v(-75.1, -146.6) * mm, "end": v(-153.1, -146.6) * mm});
            skPoint(sketch, "E281.visualSharp", {"position": v(-73.1, -146.6) * mm});
            skArc(sketch, "E281.filletArc", {"start": v(-75.1, -146.6) * mm, "mid": v(-73.69, -146.01) * mm, "end": v(-73.1, -144.6) * mm});
            skPoint(sketch, "E282.visualSharp", {"position": v(-73.1, -90) * mm});
            skArc(sketch, "E282.filletArc", {"start": v(-73.1, -92) * mm, "mid": v(-73.69, -90.59) * mm, "end": v(-75.1, -90) * mm});
            skPoint(sketch, "E283.visualSharp", {"position": v(-155.1, -90) * mm});
            skArc(sketch, "E283.filletArc", {"start": v(-153.1, -90) * mm, "mid": v(-154.51, -90.59) * mm, "end": v(-155.1, -92) * mm});
            skPoint(sketch, "E284.newPointA", {"position": v(-155.1, -151.6) * mm});
            skArc(sketch, "E284.filletArc", {"start": v(-155.1, -144.6) * mm, "mid": v(-154.51, -146.01) * mm, "end": v(-153.1, -146.6) * mm});
            skLineSegment(sketch, "E285", {"start": v(-222.7, -77) * mm, "end": v(-226.7, -77) * mm});
            skLineSegment(sketch, "E286", {"start": v(-5, -75) * mm, "end": v(-5, -77) * mm});
            skLineSegment(sketch, "E287", {"start": v(-5, -83.1) * mm, "end": v(-5, -92) * mm});
            skLineSegment(sketch, "E288", {"start": v(-65, -146.6) * mm, "end": v(-69, -146.6) * mm});
            skLineSegment(sketch, "E289", {"start": v(-71.1, -146.6) * mm, "end": v(-75.1, -146.6) * mm});
            skLineSegment(sketch, "E290", {"start": v(-153.1, -146.6) * mm, "end": v(-158.1, -146.6) * mm});
            skLineSegment(sketch, "E291", {"start": v(-224.7, -75) * mm, "end": v(-224.7, -79) * mm});
            skLineSegment(sketch, "E292", {"start": v(-155.1, -151.6) * mm, "end": v(-155.1, -144.6) * mm});
            skLineSegment(sketch, "E293", {"start": v(-73.1, -148.6) * mm, "end": v(-73.1, -144.6) * mm});
            skLineSegment(sketch, "E294", {"start": v(-67, -148.6) * mm, "end": v(-67, -144.6) * mm});
            skLineSegment(sketch, "E295", {"start": v(-5, -148.6) * mm, "end": v(-5, -144.6) * mm});
            skLineSegment(sketch, "E296", {"start": v(-7, -146.6) * mm, "end": v(-3, -146.6) * mm});
            skLineSegment(sketch, "E297", {"start": v(-222.7, -5) * mm, "end": v(-226.7, -5) * mm});
            skLineSegment(sketch, "E298", {"start": v(-224.7, -7) * mm, "end": v(-224.7, -3) * mm});
            skSolve(sketch);
        }
        {
            var Q0;
            Q0=makeQuery(id+"F0.imprint","IMPRINT",FACE,{"disambiguationData":[TD([[makeQuery(id+"F0.imprint","IMPRINT",EDGE,{"derivedFrom":sQuery(id+"F0.wireOp",EDGE,"E86.0")}),1.0]])]});
            var Q1;
            {var subQ6=sQuery(id+"F0.wireOp",EDGE,"E174.0");Q1=makeQuery(id+"F0.imprint","IMPRINT",FACE,{"disambiguationData":[TD([[makeQuery(id+"F0.imprint","IMPRINT",EDGE,{"derivedFrom":subQ6}),1.0]])]});}
            var Q2;
            {var subQ0=sQuery(id+"F0.wireOp",EDGE,"E207");Q2=makeQuery(id+"F0.imprint","IMPRINT",FACE,{"disambiguationData":[TD([[makeQuery(id+"F0.imprint","IMPRINT",EDGE,{"derivedFrom":subQ0}),1.0]])]});}
            var Q3;
            Q3=makeQuery(id+"F0.imprint","IMPRINT",FACE,{"disambiguationData":[TD([[makeQuery(id+"F0.imprint","IMPRINT",EDGE,{"derivedFrom":sQuery(id+"F0.wireOp",EDGE,"E86.0")}),-1.0]])]});
            var Q4;
            {var subQ1=sQuery(id+"F0.wireOp",EDGE,"E154");Q4=makeQuery(id+"F0.imprint","IMPRINT",FACE,{"disambiguationData":[TD([[makeQuery(id+"F0.imprint","IMPRINT",EDGE,{"derivedFrom":subQ1}),-1.0]])]});}
            var Q5;
            {var subQ0=sQuery(id+"F0.wireOp",EDGE,"E249.filletArc");Q5=makeQuery(id+"F0.imprint","IMPRINT",FACE,{"disambiguationData":[TD([[makeQuery(id+"F0.imprint","IMPRINT",EDGE,{"derivedFrom":subQ0}),-1.0]])]});}
            var Q6;
            {var subQ1=sQuery(id+"F0.wireOp",EDGE,"E250");Q6=makeQuery(id+"F0.imprint","IMPRINT",FACE,{"disambiguationData":[TD([[makeQuery(id+"F0.imprint","IMPRINT",EDGE,{"derivedFrom":subQ1}),-1.0]])]});}
            var Q7;
            {var subQ0=sQuery(id+"F0.wireOp",EDGE,"E257.filletArc");Q7=makeQuery(id+"F0.imprint","IMPRINT",FACE,{"disambiguationData":[TD([[makeQuery(id+"F0.imprint","IMPRINT",EDGE,{"derivedFrom":subQ0}),-1.0]])]});}
            var Q8;
            {var subQ5=sQuery(id+"F0.wireOp",EDGE,"E40.0");Q8=makeQuery(id+"F0.imprint","IMPRINT",FACE,{"disambiguationData":[TD([[makeQuery(id+"F0.imprint","IMPRINT",EDGE,{"derivedFrom":subQ5}),-1.0]])]});}
            var Q9;
            {var subQ0=sQuery(id+"F0.wireOp",EDGE,"E247.filletArc");Q9=makeQuery(id+"F0.imprint","IMPRINT",FACE,{"disambiguationData":[TD([[makeQuery(id+"F0.imprint","IMPRINT",EDGE,{"derivedFrom":subQ0}),-1.0]])]});}
            var Q10;
            {var subQ0=sQuery(id+"F0.wireOp",EDGE,"E256.filletArc");Q10=makeQuery(id+"F0.imprint","IMPRINT",FACE,{"disambiguationData":[TD([[makeQuery(id+"F0.imprint","IMPRINT",EDGE,{"derivedFrom":subQ0}),-1.0]])]});}
            var Q11;
            {var subQ1=sQuery(id+"F0.wireOp",EDGE,"E207");Q11=makeQuery(id+"F0.imprint","IMPRINT",FACE,{"disambiguationData":[TD([[makeQuery(id+"F0.imprint","IMPRINT",EDGE,{"derivedFrom":subQ1}),-1.0]])]});}
            extrude(context, id + "F1", {"entities" : qUnion([Q0, Q1, Q2, Q3, Q4, Q5, Q6, Q7, Q8, Q9, Q10, Q11]), "oppositeDirection" : true, "depth" : 15 * mm, "hasSecondDirection" : true, "secondDirectionOppositeDirection" : true, "secondDirectionDepth" : 10 * mm});
        }
        {
            var Q0;
            Q0=makeQuery(id+"F0.imprint","IMPRINT",FACE,{"disambiguationData":[TD([[makeQuery(id+"F0.imprint","IMPRINT",EDGE,{"derivedFrom":sQuery(id+"F0.wireOp",EDGE,"E174.0")}),1.0]])]});
            var Q1;
            {var subQ0=sQuery(id+"F0.wireOp",EDGE,"E207");Q1=makeQuery(id+"F0.imprint","IMPRINT",FACE,{"disambiguationData":[TD([[makeQuery(id+"F0.imprint","IMPRINT",EDGE,{"derivedFrom":subQ0}),1.0]])]});}
            var Q2;
            Q2=makeQuery(id+"F0.imprint","IMPRINT",FACE,{"disambiguationData":[TD([[makeQuery(id+"F0.imprint","IMPRINT",EDGE,{"derivedFrom":sQuery(id+"F0.wireOp",EDGE,"E209")}),1.0]])]});
            var Q3;
            Q3=makeQuery(id+"F0.imprint","IMPRINT",FACE,{"disambiguationData":[TD([[makeQuery(id+"F0.imprint","IMPRINT",EDGE,{"derivedFrom":sQuery(id+"F0.wireOp",EDGE,"E220")}),1.0]])]});
            var Q4;
            Q4=makeQuery(id+"F0.imprint","IMPRINT",FACE,{"disambiguationData":[TD([[makeQuery(id+"F0.imprint","IMPRINT",EDGE,{"derivedFrom":sQuery(id+"F0.wireOp",EDGE,"E219")}),1.0]])]});
            var Q5;
            Q5=makeQuery(id+"F0.imprint","IMPRINT",FACE,{"disambiguationData":[TD([[makeQuery(id+"F0.imprint","IMPRINT",EDGE,{"derivedFrom":sQuery(id+"F0.wireOp",EDGE,"E216")}),1.0]])]});
            var Q6;
            Q6=makeQuery(id+"F0.imprint","IMPRINT",FACE,{"disambiguationData":[TD([[makeQuery(id+"F0.imprint","IMPRINT",EDGE,{"derivedFrom":sQuery(id+"F0.wireOp",EDGE,"E86.0")}),-1.0]])]});
            var Q7;
            {var subQ1=sQuery(id+"F0.wireOp",EDGE,"E250");Q7=makeQuery(id+"F0.imprint","IMPRINT",FACE,{"disambiguationData":[TD([[makeQuery(id+"F0.imprint","IMPRINT",EDGE,{"derivedFrom":subQ1}),-1.0]])]});}
            var Q8;
            {var subQ0=sQuery(id+"F0.wireOp",EDGE,"E257.filletArc");Q8=makeQuery(id+"F0.imprint","IMPRINT",FACE,{"disambiguationData":[TD([[makeQuery(id+"F0.imprint","IMPRINT",EDGE,{"derivedFrom":subQ0}),-1.0]])]});}
            var Q9;
            {var subQ0=sQuery(id+"F0.wireOp",EDGE,"E256.filletArc");Q9=makeQuery(id+"F0.imprint","IMPRINT",FACE,{"disambiguationData":[TD([[makeQuery(id+"F0.imprint","IMPRINT",EDGE,{"derivedFrom":subQ0}),-1.0]])]});}
            var Q10;
            {var subQ1=sQuery(id+"F0.wireOp",EDGE,"E207");Q10=makeQuery(id+"F0.imprint","IMPRINT",FACE,{"disambiguationData":[TD([[makeQuery(id+"F0.imprint","IMPRINT",EDGE,{"derivedFrom":subQ1}),-1.0]])]});}
            var Q11;
            {var subQ0=sQuery(id+"F0.wireOp",EDGE,"E247.filletArc");Q11=makeQuery(id+"F0.imprint","IMPRINT",FACE,{"disambiguationData":[TD([[makeQuery(id+"F0.imprint","IMPRINT",EDGE,{"derivedFrom":subQ0}),-1.0]])]});}
            extrude(context, id + "F2", {"entities" : qUnion([Q0, Q1, Q2, Q3, Q4, Q5, Q6, Q7, Q8, Q9, Q10, Q11]), "operationType" : NewBodyOperationType.ADD, "oppositeDirection" : true, "depth" : 10 * mm});
        }
        {
            var Q0;
            Q0=makeQuery(id+"F0.imprint","IMPRINT",FACE,{"disambiguationData":[TD([[makeQuery(id+"F0.imprint","IMPRINT",EDGE,{"derivedFrom":sQuery(id+"F0.wireOp",EDGE,"E87.0")}),1.0]])]});
            var Q1;
            {var subQ1=sQuery(id+"F0.wireOp",EDGE,"E88.0");Q1=makeQuery(id+"F0.imprint","IMPRINT",FACE,{"disambiguationData":[TD([[makeQuery(id+"F0.imprint","IMPRINT",EDGE,{"derivedFrom":subQ1}),-1.0]])]});}
            var Q2;
            Q2=makeQuery(id+"F0.imprint","IMPRINT",FACE,{"disambiguationData":[TD([[makeQuery(id+"F0.imprint","IMPRINT",EDGE,{"derivedFrom":sQuery(id+"F0.wireOp",EDGE,"E11")}),-1.0]])]});
            var Q3;
            Q3=makeQuery(id+"F0.imprint","IMPRINT",FACE,{"disambiguationData":[TD([[makeQuery(id+"F0.imprint","IMPRINT",EDGE,{"derivedFrom":sQuery(id+"F0.wireOp",EDGE,"E156.trimOffspring")}),-1.0]])]});
            var Q4;
            Q4=makeQuery(id+"F0.imprint","IMPRINT",FACE,{"disambiguationData":[TD([[makeQuery(id+"F0.imprint","IMPRINT",EDGE,{"derivedFrom":sQuery(id+"F0.wireOp",EDGE,"E117.top")}),-1.0]])]});
            var Q5;
            Q5=makeQuery(id+"F0.imprint","IMPRINT",FACE,{"disambiguationData":[TD([[makeQuery(id+"F0.imprint","IMPRINT",EDGE,{"derivedFrom":sQuery(id+"F0.wireOp",EDGE,"E13")}),1.0]])]});
            var Q6;
            {var subQ1=sQuery(id+"F0.wireOp",EDGE,"E95");Q6=makeQuery(id+"F0.imprint","IMPRINT",FACE,{"disambiguationData":[TD([[makeQuery(id+"F0.imprint","IMPRINT",EDGE,{"derivedFrom":subQ1}),1.0]])]});}
            var Q7;
            Q7=makeQuery(id+"F0.imprint","IMPRINT",FACE,{"disambiguationData":[TD([[makeQuery(id+"F0.imprint","IMPRINT",EDGE,{"derivedFrom":sQuery(id+"F0.wireOp",EDGE,"E11")}),1.0]])]});
            var Q8;
            {var subQ0=sQuery(id+"F0.wireOp",EDGE,"E215");Q8=makeQuery(id+"F0.imprint","IMPRINT",FACE,{"disambiguationData":[TD([[makeQuery(id+"F0.imprint","IMPRINT",EDGE,{"derivedFrom":subQ0}),1.0]])]});}
            var Q9;
            Q9=makeQuery(id+"F0.imprint","IMPRINT",FACE,{"disambiguationData":[TD([[makeQuery(id+"F0.imprint","IMPRINT",EDGE,{"derivedFrom":sQuery(id+"F0.wireOp",EDGE,"E87.0")}),-1.0]])]});
            var Q10;
            {var subQ3=sQuery(id+"F0.wireOp",EDGE,"E221");Q10=makeQuery(id+"F0.imprint","IMPRINT",FACE,{"disambiguationData":[TD([[makeQuery(id+"F0.imprint","IMPRINT",EDGE,{"derivedFrom":subQ3}),-1.0]])]});}
            var Q11;
            {var subQ1=sQuery(id+"F0.wireOp",EDGE,"E88.0");Q11=makeQuery(id+"F0.imprint","IMPRINT",FACE,{"disambiguationData":[TD([[makeQuery(id+"F0.imprint","IMPRINT",EDGE,{"derivedFrom":subQ1}),1.0]])]});}
            var Q12;
            {var subQ4=sQuery(id+"F0.wireOp",EDGE,"E155.0");Q12=makeQuery(id+"F0.imprint","IMPRINT",FACE,{"disambiguationData":[TD([[makeQuery(id+"F0.imprint","IMPRINT",EDGE,{"derivedFrom":subQ4}),1.0]])]});}
            var Q13;
            {var subQ0=sQuery(id+"F0.wireOp",EDGE,"E232");Q13=makeQuery(id+"F0.imprint","IMPRINT",FACE,{"disambiguationData":[TD([[makeQuery(id+"F0.imprint","IMPRINT",EDGE,{"derivedFrom":subQ0}),1.0]])]});}
            var Q14;
            Q14=makeQuery(id+"F0.imprint","IMPRINT",FACE,{"disambiguationData":[TD([[makeQuery(id+"F0.imprint","IMPRINT",EDGE,{"derivedFrom":sQuery(id+"F0.wireOp",EDGE,"E122.bottom")}),1.0]])]});
            var Q15;
            Q15=makeQuery(id+"F0.imprint","IMPRINT",FACE,{"disambiguationData":[TD([[makeQuery(id+"F0.imprint","IMPRINT",EDGE,{"derivedFrom":sQuery(id+"F0.wireOp",EDGE,"E122.bottom")}),-1.0]])]});
            var Q16;
            Q16=makeQuery(id+"F0.imprint","IMPRINT",FACE,{"disambiguationData":[TD([[makeQuery(id+"F0.imprint","IMPRINT",EDGE,{"derivedFrom":sQuery(id+"F0.wireOp",EDGE,"E117.bottom")}),1.0]])]});
            var Q17;
            Q17=makeQuery(id+"F0.imprint","IMPRINT",FACE,{"disambiguationData":[TD([[makeQuery(id+"F0.imprint","IMPRINT",EDGE,{"derivedFrom":sQuery(id+"F0.wireOp",EDGE,"E117.bottom")}),-1.0]])]});
            var Q18;
            {var subQ0=sQuery(id+"F0.wireOp",EDGE,"E134.MirrorCS");Q18=makeQuery(id+"F0.imprint","IMPRINT",FACE,{"disambiguationData":[TD([[makeQuery(id+"F0.imprint","IMPRINT",EDGE,{"derivedFrom":subQ0}),1.0]])]});}
            var Q19;
            Q19=makeQuery(id+"F0.imprint","IMPRINT",FACE,{"disambiguationData":[TD([[makeQuery(id+"F0.imprint","IMPRINT",EDGE,{"derivedFrom":sQuery(id+"F0.wireOp",EDGE,"E135.MirrorCS")}),-1.0]])]});
            var Q20;
            {var subQ0=sQuery(id+"F0.wireOp",EDGE,"E144.MirrorCS");Q20=makeQuery(id+"F0.imprint","IMPRINT",FACE,{"disambiguationData":[TD([[makeQuery(id+"F0.imprint","IMPRINT",EDGE,{"derivedFrom":subQ0}),1.0]])]});}
            var Q21;
            Q21=makeQuery(id+"F0.imprint","IMPRINT",FACE,{"disambiguationData":[TD([[makeQuery(id+"F0.imprint","IMPRINT",EDGE,{"derivedFrom":sQuery(id+"F0.wireOp",EDGE,"E145.MirrorCS")}),-1.0]])]});
            var Q22;
            {var subQ1=sQuery(id+"F0.wireOp",EDGE,"E235");Q22=makeQuery(id+"F0.imprint","IMPRINT",FACE,{"disambiguationData":[TD([[makeQuery(id+"F0.imprint","IMPRINT",EDGE,{"derivedFrom":subQ1}),-1.0]])]});}
            var Q23;
            {var subQ0=sQuery(id+"F0.wireOp",EDGE,"E276.filletArc");Q23=makeQuery(id+"F0.imprint","IMPRINT",FACE,{"disambiguationData":[TD([[makeQuery(id+"F0.imprint","IMPRINT",EDGE,{"derivedFrom":subQ0}),-1.0]])]});}
            var Q24;
            {var subQ1=sQuery(id+"F0.wireOp",EDGE,"E156.trimOffspring");Q24=makeQuery(id+"F0.imprint","IMPRINT",FACE,{"disambiguationData":[TD([[makeQuery(id+"F0.imprint","IMPRINT",EDGE,{"derivedFrom":subQ1}),1.0]])]});}
            var Q25;
            {var subQ0=sQuery(id+"F0.wireOp",EDGE,"E278.filletArc");Q25=makeQuery(id+"F0.imprint","IMPRINT",FACE,{"disambiguationData":[TD([[makeQuery(id+"F0.imprint","IMPRINT",EDGE,{"derivedFrom":subQ0}),-1.0]])]});}
            var Q26;
            {var subQ1=sQuery(id+"F0.wireOp",EDGE,"E239");Q26=makeQuery(id+"F0.imprint","IMPRINT",FACE,{"disambiguationData":[TD([[makeQuery(id+"F0.imprint","IMPRINT",EDGE,{"derivedFrom":subQ1}),-1.0]])]});}
            var Q27;
            {var subQ0=sQuery(id+"F0.wireOp",EDGE,"E14");Q27=makeQuery(id+"F0.imprint","IMPRINT",FACE,{"disambiguationData":[TD([[makeQuery(id+"F0.imprint","IMPRINT",EDGE,{"derivedFrom":subQ0}),1.0]])]});}
            var Q28;
            {var subQ1=sQuery(id+"F0.wireOp",EDGE,"E158.0");Q28=makeQuery(id+"F0.imprint","IMPRINT",FACE,{"disambiguationData":[TD([[makeQuery(id+"F0.imprint","IMPRINT",EDGE,{"derivedFrom":subQ1}),1.0]])]});}
            var Q29;
            {var subQ0=sQuery(id+"F0.wireOp",EDGE,"E279.filletArc");Q29=makeQuery(id+"F0.imprint","IMPRINT",FACE,{"disambiguationData":[TD([[makeQuery(id+"F0.imprint","IMPRINT",EDGE,{"derivedFrom":subQ0}),-1.0]])]});}
            var Q30;
            {var subQ0=sQuery(id+"F0.wireOp",EDGE,"E281.filletArc");Q30=makeQuery(id+"F0.imprint","IMPRINT",FACE,{"disambiguationData":[TD([[makeQuery(id+"F0.imprint","IMPRINT",EDGE,{"derivedFrom":subQ0}),-1.0]])]});}
            var Q31;
            {var subQ0=sQuery(id+"F0.wireOp",EDGE,"E284.filletArc");Q31=makeQuery(id+"F0.imprint","IMPRINT",FACE,{"disambiguationData":[TD([[makeQuery(id+"F0.imprint","IMPRINT",EDGE,{"derivedFrom":subQ0}),-1.0]])]});}
            var Q32;
            {var subQ0=sQuery(id+"F0.wireOp",EDGE,"E9");var subQ1=sQuery(id+"F0.wireOp",EDGE,"E8");var subQ2=makeQuery(id+"F0.imprint","INTERSECT",VERTEX,{"derivedFrom":[subQ1,subQ0]});Q32=makeQuery(id+"F0.imprint","IMPRINT",FACE,{"disambiguationData":[TD([[makeQuery(id+"F0.imprint","IMPRINT",EDGE,{"disambiguationData":[TD([[subQ2,1.0]])],"derivedFrom":subQ1}),-1.0]])]});}
            var Q33;
            {var subQ4=sQuery(id+"F0.wireOp",EDGE,"E240");Q33=makeQuery(id+"F0.imprint","IMPRINT",FACE,{"disambiguationData":[TD([[makeQuery(id+"F0.imprint","IMPRINT",EDGE,{"derivedFrom":subQ4}),-1.0]])]});}
            var Q34;
            {var subQ0=sQuery(id+"F0.wireOp",EDGE,"E4");Q34=makeQuery(id+"F0.imprint","IMPRINT",FACE,{"disambiguationData":[TD([[makeQuery(id+"F0.imprint","IMPRINT",EDGE,{"derivedFrom":subQ0}),-1.0]])]});}
            var Q35;
            {var subQ0=sQuery(id+"F0.wireOp",EDGE,"E254.filletArc");Q35=makeQuery(id+"F0.imprint","IMPRINT",FACE,{"disambiguationData":[TD([[makeQuery(id+"F0.imprint","IMPRINT",EDGE,{"derivedFrom":subQ0}),-1.0]])]});}
            var Q36;
            {var subQ0=sQuery(id+"F0.wireOp",EDGE,"E253.filletArc");Q36=makeQuery(id+"F0.imprint","IMPRINT",FACE,{"disambiguationData":[TD([[makeQuery(id+"F0.imprint","IMPRINT",EDGE,{"derivedFrom":subQ0}),-1.0]])]});}
            extrude(context, id + "F3", {"entities" : qUnion([Q0, Q1, Q2, Q3, Q4, Q5, Q6, Q7, Q8, Q9, Q10, Q11, Q12, Q13, Q14, Q15, Q16, Q17, Q18, Q19, Q20, Q21, Q22, Q23, Q24, Q25, Q26, Q27, Q28, Q29, Q30, Q31, Q32, Q33, Q34, Q35, Q36]), "oppositeDirection" : true, "depth" : 15 * mm, "hasSecondDirection" : true, "secondDirectionOppositeDirection" : true, "secondDirectionDepth" : 10 * mm});
        }
        {
            var Q0;
            Q0=makeQuery(id+"F0.imprint","IMPRINT",FACE,{"disambiguationData":[TD([[makeQuery(id+"F0.imprint","IMPRINT",EDGE,{"derivedFrom":sQuery(id+"F0.wireOp",EDGE,"E218")}),1.0]])]});
            var Q1;
            Q1=makeQuery(id+"F0.imprint","IMPRINT",FACE,{"disambiguationData":[TD([[makeQuery(id+"F0.imprint","IMPRINT",EDGE,{"derivedFrom":sQuery(id+"F0.wireOp",EDGE,"E217")}),1.0]])]});
            var Q2;
            Q2=makeQuery(id+"F0.imprint","IMPRINT",FACE,{"disambiguationData":[TD([[makeQuery(id+"F0.imprint","IMPRINT",EDGE,{"derivedFrom":sQuery(id+"F0.wireOp",EDGE,"E87.0")}),-1.0]])]});
            var Q3;
            {var subQ0=sQuery(id+"F0.wireOp",EDGE,"E215");Q3=makeQuery(id+"F0.imprint","IMPRINT",FACE,{"disambiguationData":[TD([[makeQuery(id+"F0.imprint","IMPRINT",EDGE,{"derivedFrom":subQ0}),1.0]])]});}
            var Q4;
            {var subQ3=sQuery(id+"F0.wireOp",EDGE,"E221");Q4=makeQuery(id+"F0.imprint","IMPRINT",FACE,{"disambiguationData":[TD([[makeQuery(id+"F0.imprint","IMPRINT",EDGE,{"derivedFrom":subQ3}),-1.0]])]});}
            var Q5;
            Q5=makeQuery(id+"F0.imprint","IMPRINT",FACE,{"disambiguationData":[TD([[makeQuery(id+"F0.imprint","IMPRINT",EDGE,{"derivedFrom":sQuery(id+"F0.wireOp",EDGE,"E223")}),1.0]])]});
            var Q6;
            Q6=makeQuery(id+"F0.imprint","IMPRINT",FACE,{"disambiguationData":[TD([[makeQuery(id+"F0.imprint","IMPRINT",EDGE,{"derivedFrom":sQuery(id+"F0.wireOp",EDGE,"E224")}),1.0]])]});
            var Q7;
            {var subQ1=sQuery(id+"F0.wireOp",EDGE,"E88.0");Q7=makeQuery(id+"F0.imprint","IMPRINT",FACE,{"disambiguationData":[TD([[makeQuery(id+"F0.imprint","IMPRINT",EDGE,{"derivedFrom":subQ1}),1.0]])]});}
            var Q8;
            Q8=makeQuery(id+"F0.imprint","IMPRINT",FACE,{"disambiguationData":[TD([[makeQuery(id+"F0.imprint","IMPRINT",EDGE,{"derivedFrom":sQuery(id+"F0.wireOp",EDGE,"E228")}),1.0]])]});
            var Q9;
            Q9=makeQuery(id+"F0.imprint","IMPRINT",FACE,{"disambiguationData":[TD([[makeQuery(id+"F0.imprint","IMPRINT",EDGE,{"derivedFrom":sQuery(id+"F0.wireOp",EDGE,"E229")}),1.0]])]});
            var Q10;
            {var subQ4=sQuery(id+"F0.wireOp",EDGE,"E155.0");Q10=makeQuery(id+"F0.imprint","IMPRINT",FACE,{"disambiguationData":[TD([[makeQuery(id+"F0.imprint","IMPRINT",EDGE,{"derivedFrom":subQ4}),1.0]])]});}
            var Q11;
            Q11=makeQuery(id+"F0.imprint","IMPRINT",FACE,{"disambiguationData":[TD([[makeQuery(id+"F0.imprint","IMPRINT",EDGE,{"derivedFrom":sQuery(id+"F0.wireOp",EDGE,"E233")}),1.0]])]});
            var Q12;
            Q12=makeQuery(id+"F0.imprint","IMPRINT",FACE,{"disambiguationData":[TD([[makeQuery(id+"F0.imprint","IMPRINT",EDGE,{"derivedFrom":sQuery(id+"F0.wireOp",EDGE,"E234")}),1.0]])]});
            var Q13;
            {var subQ0=sQuery(id+"F0.wireOp",EDGE,"E232");Q13=makeQuery(id+"F0.imprint","IMPRINT",FACE,{"disambiguationData":[TD([[makeQuery(id+"F0.imprint","IMPRINT",EDGE,{"derivedFrom":subQ0}),1.0]])]});}
            var Q14;
            {var subQ1=sQuery(id+"F0.wireOp",EDGE,"E235");Q14=makeQuery(id+"F0.imprint","IMPRINT",FACE,{"disambiguationData":[TD([[makeQuery(id+"F0.imprint","IMPRINT",EDGE,{"derivedFrom":subQ1}),-1.0]])]});}
            var Q15;
            Q15=makeQuery(id+"F0.imprint","IMPRINT",FACE,{"disambiguationData":[TD([[makeQuery(id+"F0.imprint","IMPRINT",EDGE,{"derivedFrom":sQuery(id+"F0.wireOp",EDGE,"E237")}),1.0]])]});
            var Q16;
            Q16=makeQuery(id+"F0.imprint","IMPRINT",FACE,{"disambiguationData":[TD([[makeQuery(id+"F0.imprint","IMPRINT",EDGE,{"derivedFrom":sQuery(id+"F0.wireOp",EDGE,"E238")}),1.0]])]});
            var Q17;
            {var subQ1=sQuery(id+"F0.wireOp",EDGE,"E156.trimOffspring");Q17=makeQuery(id+"F0.imprint","IMPRINT",FACE,{"disambiguationData":[TD([[makeQuery(id+"F0.imprint","IMPRINT",EDGE,{"derivedFrom":subQ1}),1.0]])]});}
            var Q18;
            {var subQ0=sQuery(id+"F0.wireOp",EDGE,"E278.filletArc");Q18=makeQuery(id+"F0.imprint","IMPRINT",FACE,{"disambiguationData":[TD([[makeQuery(id+"F0.imprint","IMPRINT",EDGE,{"derivedFrom":subQ0}),-1.0]])]});}
            var Q19;
            {var subQ1=sQuery(id+"F0.wireOp",EDGE,"E239");Q19=makeQuery(id+"F0.imprint","IMPRINT",FACE,{"disambiguationData":[TD([[makeQuery(id+"F0.imprint","IMPRINT",EDGE,{"derivedFrom":subQ1}),-1.0]])]});}
            var Q20;
            {var subQ0=sQuery(id+"F0.wireOp",EDGE,"E14");Q20=makeQuery(id+"F0.imprint","IMPRINT",FACE,{"disambiguationData":[TD([[makeQuery(id+"F0.imprint","IMPRINT",EDGE,{"derivedFrom":subQ0}),1.0]])]});}
            var Q21;
            {var subQ1=sQuery(id+"F0.wireOp",EDGE,"E158.0");Q21=makeQuery(id+"F0.imprint","IMPRINT",FACE,{"disambiguationData":[TD([[makeQuery(id+"F0.imprint","IMPRINT",EDGE,{"derivedFrom":subQ1}),1.0]])]});}
            var Q22;
            {var subQ0=sQuery(id+"F0.wireOp",EDGE,"E279.filletArc");Q22=makeQuery(id+"F0.imprint","IMPRINT",FACE,{"disambiguationData":[TD([[makeQuery(id+"F0.imprint","IMPRINT",EDGE,{"derivedFrom":subQ0}),-1.0]])]});}
            var Q23;
            {var subQ4=sQuery(id+"F0.wireOp",EDGE,"E240");Q23=makeQuery(id+"F0.imprint","IMPRINT",FACE,{"disambiguationData":[TD([[makeQuery(id+"F0.imprint","IMPRINT",EDGE,{"derivedFrom":subQ4}),-1.0]])]});}
            var Q24;
            {var subQ0=sQuery(id+"F0.wireOp",EDGE,"E9");var subQ1=sQuery(id+"F0.wireOp",EDGE,"E8");var subQ2=makeQuery(id+"F0.imprint","INTERSECT",VERTEX,{"derivedFrom":[subQ1,subQ0]});Q24=makeQuery(id+"F0.imprint","IMPRINT",FACE,{"disambiguationData":[TD([[makeQuery(id+"F0.imprint","IMPRINT",EDGE,{"disambiguationData":[TD([[subQ2,1.0]])],"derivedFrom":subQ1}),-1.0]])]});}
            var Q25;
            {var subQ0=sQuery(id+"F0.wireOp",EDGE,"E4");Q25=makeQuery(id+"F0.imprint","IMPRINT",FACE,{"disambiguationData":[TD([[makeQuery(id+"F0.imprint","IMPRINT",EDGE,{"derivedFrom":subQ0}),-1.0]])]});}
            var Q26;
            {var subQ0=sQuery(id+"F0.wireOp",EDGE,"E254.filletArc");Q26=makeQuery(id+"F0.imprint","IMPRINT",FACE,{"disambiguationData":[TD([[makeQuery(id+"F0.imprint","IMPRINT",EDGE,{"derivedFrom":subQ0}),-1.0]])]});}
            var Q27;
            {var subQ0=sQuery(id+"F0.wireOp",EDGE,"E253.filletArc");Q27=makeQuery(id+"F0.imprint","IMPRINT",FACE,{"disambiguationData":[TD([[makeQuery(id+"F0.imprint","IMPRINT",EDGE,{"derivedFrom":subQ0}),-1.0]])]});}
            extrude(context, id + "F4", {"entities" : qUnion([Q0, Q1, Q2, Q3, Q4, Q5, Q6, Q7, Q8, Q9, Q10, Q11, Q12, Q13, Q14, Q15, Q16, Q17, Q18, Q19, Q20, Q21, Q22, Q23, Q24, Q25, Q26, Q27]), "operationType" : NewBodyOperationType.ADD, "oppositeDirection" : true, "depth" : 10 * mm});
        }
        {
            var Q0;
            Q0=makeQuery(id+"F0.imprint","IMPRINT",FACE,{"disambiguationData":[TD([[makeQuery(id+"F0.imprint","IMPRINT",EDGE,{"derivedFrom":sQuery(id+"F0.wireOp",EDGE,"E16")}),-1.0]])]});
            var Q1;
            Q1=makeQuery(id+"F0.imprint","IMPRINT",FACE,{"disambiguationData":[TD([[makeQuery(id+"F0.imprint","IMPRINT",EDGE,{"derivedFrom":sQuery(id+"F0.wireOp",EDGE,"E20")}),1.0]])]});
            extrude(context, id + "F5", {"entities" : qUnion([Q0, Q1]), "oppositeDirection" : true, "depth" : 55 * mm});
        }
        {
            var Q0;
            {var subQ0=sQuery(id+"F0.wireOp",EDGE,"E23");Q0=makeQuery(id+"F0.imprint","IMPRINT",FACE,{"disambiguationData":[TD([[makeQuery(id+"F0.imprint","IMPRINT",EDGE,{"derivedFrom":subQ0}),1.0]])]});}
            var Q1;
            {var subQ0=sQuery(id+"F0.wireOp",EDGE,"E23");Q1=makeQuery(id+"F0.imprint","IMPRINT",FACE,{"disambiguationData":[TD([[makeQuery(id+"F0.imprint","IMPRINT",EDGE,{"derivedFrom":subQ0}),-1.0]])]});}
            var Q2;
            Q2=makeQuery(id+"F5.opExtrude","CAP_FACE",FACE,{"disambiguationData":[OSD([sQuery(id+"F0.wireOp",EDGE,"E16"),sQuery(id+"F0.wireOp",EDGE,"E19"),sQuery(id+"F0.wireOp",EDGE,"E20"),sQuery(id+"F0.wireOp",EDGE,"E24"),sQuery(id+"F0.wireOp",EDGE,"E25"),sQuery(id+"F0.wireOp",EDGE,"E26"),sQuery(id+"F0.wireOp",EDGE,"E30"),sQuery(id+"F0.wireOp",EDGE,"E34"),sQuery(id+"F0.wireOp",EDGE,"E35"),sQuery(id+"F0.wireOp",EDGE,"E37.MirrorCS"),sQuery(id+"F0.wireOp",EDGE,"E38.MirrorCS"),sQuery(id+"F0.wireOp",EDGE,"E39.MirrorCS"),sQuery(id+"F0.wireOp",EDGE,"E42.trimOffspring"),sQuery(id+"F0.wireOp",EDGE,"E44"),sQuery(id+"F0.wireOp",EDGE,"E48"),sQuery(id+"F0.wireOp",EDGE,"E49"),sQuery(id+"F0.wireOp",EDGE,"E51.MirrorCS"),sQuery(id+"F0.wireOp",EDGE,"E52.MirrorCS"),sQuery(id+"F0.wireOp",EDGE,"E53.MirrorCS"),sQuery(id+"F0.wireOp",EDGE,"E56.trimOffspring"),sQuery(id+"F0.wireOp",EDGE,"E58"),sQuery(id+"F0.wireOp",EDGE,"E62"),sQuery(id+"F0.wireOp",EDGE,"E63"),sQuery(id+"F0.wireOp",EDGE,"E65.MirrorCS"),sQuery(id+"F0.wireOp",EDGE,"E66.MirrorCS"),sQuery(id+"F0.wireOp",EDGE,"E67.MirrorCS"),sQuery(id+"F0.wireOp",EDGE,"E71.trimOffspring"),sQuery(id+"F0.wireOp",EDGE,"E72"),sQuery(id+"F0.wireOp",EDGE,"E76"),sQuery(id+"F0.wireOp",EDGE,"E77"),sQuery(id+"F0.wireOp",EDGE,"E79.MirrorCS"),sQuery(id+"F0.wireOp",EDGE,"E80.MirrorCS"),sQuery(id+"F0.wireOp",EDGE,"E81.MirrorCS"),sQuery(id+"F0.wireOp",EDGE,"E85.trimOffspring")])],"isStart":false});
            extrude(context, id + "F6", {"entities" : qUnion([Q0, Q1]), "operationType" : NewBodyOperationType.ADD, "oppositeDirection" : true, "endBoundEntityFace" : qUnion([Q2]), "depth" : 55 * mm, "hasSecondDirection" : true, "secondDirectionOppositeDirection" : true, "secondDirectionDepth" : 52 * mm});
        }
        {
            var Q0;
            Q0=makeQuery(id+"F5.opExtrude","CAP_FACE",FACE,{"disambiguationData":[OSD([sQuery(id+"F0.wireOp",EDGE,"E16"),sQuery(id+"F0.wireOp",EDGE,"E19"),sQuery(id+"F0.wireOp",EDGE,"E20"),sQuery(id+"F0.wireOp",EDGE,"E24"),sQuery(id+"F0.wireOp",EDGE,"E25"),sQuery(id+"F0.wireOp",EDGE,"E26"),sQuery(id+"F0.wireOp",EDGE,"E30"),sQuery(id+"F0.wireOp",EDGE,"E34"),sQuery(id+"F0.wireOp",EDGE,"E35"),sQuery(id+"F0.wireOp",EDGE,"E37.MirrorCS"),sQuery(id+"F0.wireOp",EDGE,"E38.MirrorCS"),sQuery(id+"F0.wireOp",EDGE,"E39.MirrorCS"),sQuery(id+"F0.wireOp",EDGE,"E42.trimOffspring"),sQuery(id+"F0.wireOp",EDGE,"E44"),sQuery(id+"F0.wireOp",EDGE,"E48"),sQuery(id+"F0.wireOp",EDGE,"E49"),sQuery(id+"F0.wireOp",EDGE,"E51.MirrorCS"),sQuery(id+"F0.wireOp",EDGE,"E52.MirrorCS"),sQuery(id+"F0.wireOp",EDGE,"E53.MirrorCS"),sQuery(id+"F0.wireOp",EDGE,"E56.trimOffspring"),sQuery(id+"F0.wireOp",EDGE,"E58"),sQuery(id+"F0.wireOp",EDGE,"E62"),sQuery(id+"F0.wireOp",EDGE,"E63"),sQuery(id+"F0.wireOp",EDGE,"E65.MirrorCS"),sQuery(id+"F0.wireOp",EDGE,"E66.MirrorCS"),sQuery(id+"F0.wireOp",EDGE,"E67.MirrorCS"),sQuery(id+"F0.wireOp",EDGE,"E71.trimOffspring"),sQuery(id+"F0.wireOp",EDGE,"E72"),sQuery(id+"F0.wireOp",EDGE,"E76"),sQuery(id+"F0.wireOp",EDGE,"E77"),sQuery(id+"F0.wireOp",EDGE,"E79.MirrorCS"),sQuery(id+"F0.wireOp",EDGE,"E80.MirrorCS"),sQuery(id+"F0.wireOp",EDGE,"E81.MirrorCS"),sQuery(id+"F0.wireOp",EDGE,"E85.trimOffspring")])],"isStart":true});
            var sketch = newSketch(context, id + "F7", { "sketchPlane" : qUnion([Q0])});
            skLineSegment(sketch, "E299.0.0", {"start": v(-229.7, -80.1) * mm, "end": v(-229.7, -116.1) * mm});
            skArc(sketch, "E299.0.1", {"start": v(-229.7, -116.1) * mm, "mid": v(-219.3, -141.2) * mm, "end": v(-194.2, -151.6) * mm});
            skLineSegment(sketch, "E299.0.2", {"start": v(-194.2, -151.6) * mm, "end": v(-158.2, -151.6) * mm});
            skLineSegment(sketch, "E299.0.3", {"start": v(-158.2, -151.6) * mm, "end": v(-158.2, -146.6) * mm});
            skArc(sketch, "E299.0.4", {"start": v(-158.2, -146.6) * mm, "mid": v(-158.5, -145.9) * mm, "end": v(-159.2, -145.6) * mm});
            skLineSegment(sketch, "E299.0.5", {"start": v(-159.2, -145.6) * mm, "end": v(-160.7, -145.6) * mm});
            skArc(sketch, "E299.0.6", {"start": v(-160.7, -145.6) * mm, "mid": v(-166.12, -144.1) * mm, "end": v(-160.7, -142.6) * mm});
            skLineSegment(sketch, "E299.0.7", {"start": v(-160.7, -142.6) * mm, "end": v(-159.2, -142.6) * mm});
            skArc(sketch, "E299.0.8", {"start": v(-159.2, -142.6) * mm, "mid": v(-158.5, -142.3) * mm, "end": v(-158.2, -141.6) * mm});
            skLineSegment(sketch, "E299.0.9", {"start": v(-158.2, -141.6) * mm, "end": v(-158.2, -95.1) * mm});
            skArc(sketch, "E299.0.10", {"start": v(-158.2, -95.1) * mm, "mid": v(-158.5, -94.4) * mm, "end": v(-159.2, -94.1) * mm});
            skLineSegment(sketch, "E299.0.11", {"start": v(-159.2, -94.1) * mm, "end": v(-160.7, -94.1) * mm});
            skArc(sketch, "E299.0.12", {"start": v(-160.7, -94.1) * mm, "mid": v(-166.12, -92.6) * mm, "end": v(-160.7, -91.1) * mm});
            skLineSegment(sketch, "E299.0.13", {"start": v(-160.7, -91.1) * mm, "end": v(-159.2, -91.1) * mm});
            skArc(sketch, "E299.0.14", {"start": v(-159.2, -91.1) * mm, "mid": v(-158.5, -90.8) * mm, "end": v(-158.2, -90.1) * mm});
            skLineSegment(sketch, "E299.0.15", {"start": v(-158.2, -90.1) * mm, "end": v(-158.2, -80.1) * mm});
            skLineSegment(sketch, "E299.0.16", {"start": v(-158.2, -80.1) * mm, "end": v(-168.2, -80.1) * mm});
            skArc(sketch, "E299.0.17", {"start": v(-168.2, -80.1) * mm, "mid": v(-168.9, -80.4) * mm, "end": v(-169.2, -81.1) * mm});
            skLineSegment(sketch, "E299.0.18", {"start": v(-169.2, -81.1) * mm, "end": v(-169.2, -82.6) * mm});
            skArc(sketch, "E299.0.19", {"start": v(-169.2, -82.6) * mm, "mid": v(-170.7, -88.02) * mm, "end": v(-172.2, -82.6) * mm});
            skLineSegment(sketch, "E299.0.20", {"start": v(-172.2, -82.6) * mm, "end": v(-172.2, -81.1) * mm});
            skArc(sketch, "E299.0.21", {"start": v(-172.2, -81.1) * mm, "mid": v(-172.5, -80.4) * mm, "end": v(-173.2, -80.1) * mm});
            skLineSegment(sketch, "E299.0.22", {"start": v(-173.2, -80.1) * mm, "end": v(-219.7, -80.1) * mm});
            skArc(sketch, "E299.0.23", {"start": v(-219.7, -80.1) * mm, "mid": v(-220.4, -80.4) * mm, "end": v(-220.7, -81.1) * mm});
            skLineSegment(sketch, "E299.0.24", {"start": v(-220.7, -81.1) * mm, "end": v(-220.7, -82.6) * mm});
            skArc(sketch, "E299.0.25", {"start": v(-220.7, -82.6) * mm, "mid": v(-222.2, -88.02) * mm, "end": v(-223.7, -82.6) * mm});
            skLineSegment(sketch, "E299.0.26", {"start": v(-223.7, -82.6) * mm, "end": v(-223.7, -81.1) * mm});
            skArc(sketch, "E299.0.27", {"start": v(-223.7, -81.1) * mm, "mid": v(-224, -80.4) * mm, "end": v(-224.7, -80.1) * mm});
            skLineSegment(sketch, "E299.0.28", {"start": v(-224.7, -80.1) * mm, "end": v(-229.7, -80.1) * mm});
            skLineSegment(sketch, "E300", {"start": v(-224.7, -80.1) * mm, "end": v(-219.7, -80.1) * mm});
            skLineSegment(sketch, "E301", {"start": v(-173.2, -80.1) * mm, "end": v(-168.2, -80.1) * mm});
            skLineSegment(sketch, "E302", {"start": v(-158.2, -90.1) * mm, "end": v(-158.2, -95.1) * mm});
            skLineSegment(sketch, "E303", {"start": v(-158.2, -141.6) * mm, "end": v(-158.2, -146.6) * mm});
            skLineSegment(sketch, "E304.0", {"start": v(-158.1, -90.44) * mm, "end": v(-158.1, -80.1) * mm});
            skArc(sketch, "E305.0", {"start": v(-160.79, -91.25) * mm, "mid": v(-163.9, -89.92) * mm, "end": v(-165.97, -92.6) * mm});
            skArc(sketch, "E306.0", {"start": v(-160.79, -93.95) * mm, "mid": v(-163.9, -95.28) * mm, "end": v(-165.97, -92.6) * mm});
            skLineSegment(sketch, "E307.0", {"start": v(-159.2, -93.95) * mm, "end": v(-160.79, -93.95) * mm});
            skLineSegment(sketch, "E308.0", {"start": v(-159.2, -91.25) * mm, "end": v(-160.79, -91.25) * mm});
            skArc(sketch, "E309.0", {"start": v(-159.2, -91.25) * mm, "mid": v(-158.52, -91.02) * mm, "end": v(-158.1, -90.44) * mm});
            skPoint(sketch, "E310.0", {"position": v(-158.52, -94.18) * mm});
            skArc(sketch, "E311.0", {"start": v(-159.2, -93.95) * mm, "mid": v(-158.52, -94.18) * mm, "end": v(-158.1, -94.76) * mm});
            skLineSegment(sketch, "E312", {"start": v(-158.1, -90.44) * mm, "end": v(-158.1, -94.76) * mm});
            skArc(sketch, "E313.0", {"start": v(-172.05, -81.1) * mm, "mid": v(-172.28, -80.42) * mm, "end": v(-172.86, -80) * mm});
            skLineSegment(sketch, "E314.0", {"start": v(-172.05, -81.1) * mm, "end": v(-172.05, -82.69) * mm});
            skPoint(sketch, "E315.0", {"position": v(-169.12, -80.42) * mm});
            skLineSegment(sketch, "E316.0", {"start": v(-169.35, -81.1) * mm, "end": v(-169.35, -82.69) * mm});
            skArc(sketch, "E317.0", {"start": v(-169.35, -82.69) * mm, "mid": v(-168.02, -85.8) * mm, "end": v(-170.7, -87.87) * mm});
            skArc(sketch, "E318.0", {"start": v(-169.35, -81.1) * mm, "mid": v(-169.12, -80.42) * mm, "end": v(-168.54, -80) * mm});
            skLineSegment(sketch, "E319", {"start": v(-172.86, -80) * mm, "end": v(-168.54, -80) * mm});
            skArc(sketch, "E320.0", {"start": v(-223.55, -81.1) * mm, "mid": v(-223.78, -80.42) * mm, "end": v(-224.36, -80) * mm});
            skLineSegment(sketch, "E321.0", {"start": v(-223.55, -81.1) * mm, "end": v(-223.55, -82.69) * mm});
            skArc(sketch, "E322.0", {"start": v(-223.55, -82.69) * mm, "mid": v(-224.88, -85.8) * mm, "end": v(-222.2, -87.87) * mm});
            skArc(sketch, "E323.0", {"start": v(-220.85, -82.69) * mm, "mid": v(-219.52, -85.8) * mm, "end": v(-222.2, -87.87) * mm});
            skLineSegment(sketch, "E324.0", {"start": v(-220.85, -81.1) * mm, "end": v(-220.85, -82.69) * mm});
            skArc(sketch, "E325.0", {"start": v(-220.85, -81.1) * mm, "mid": v(-220.62, -80.42) * mm, "end": v(-220.04, -80) * mm});
            skLineSegment(sketch, "E326", {"start": v(-224.36, -80) * mm, "end": v(-220.04, -80) * mm});
            skArc(sketch, "E327.0", {"start": v(-159.2, -142.75) * mm, "mid": v(-158.52, -142.52) * mm, "end": v(-158.1, -141.94) * mm});
            skLineSegment(sketch, "E328.0", {"start": v(-159.2, -142.75) * mm, "end": v(-160.79, -142.75) * mm});
            skArc(sketch, "E329.0", {"start": v(-160.79, -142.75) * mm, "mid": v(-163.9, -141.42) * mm, "end": v(-165.97, -144.1) * mm});
            skArc(sketch, "E330.0", {"start": v(-160.79, -145.45) * mm, "mid": v(-163.9, -146.78) * mm, "end": v(-165.97, -144.1) * mm});
            skLineSegment(sketch, "E331.0", {"start": v(-159.2, -145.45) * mm, "end": v(-160.79, -145.45) * mm});
            skArc(sketch, "E332.0", {"start": v(-159.2, -145.45) * mm, "mid": v(-158.52, -145.68) * mm, "end": v(-158.1, -146.26) * mm});
            skLineSegment(sketch, "E333", {"start": v(-158.1, -141.94) * mm, "end": v(-158.1, -146.26) * mm});
            skSolve(sketch);
        }
        {
            var Q0;
            Q0=makeQuery(id+"F7.imprint","IMPRINT",FACE,{"disambiguationData":[TD([[makeQuery(id+"F7.imprint","IMPRINT",EDGE,{"derivedFrom":sQuery(id+"F7.wireOp",EDGE,"E299.0.4")}),1.0]])]});
            var Q1;
            Q1=makeQuery(id+"F7.imprint","IMPRINT",FACE,{"disambiguationData":[TD([[makeQuery(id+"F7.imprint","IMPRINT",EDGE,{"derivedFrom":sQuery(id+"F7.wireOp",EDGE,"E299.0.10")}),1.0]])]});
            var Q2;
            Q2=makeQuery(id+"F7.imprint","IMPRINT",FACE,{"disambiguationData":[TD([[makeQuery(id+"F7.imprint","IMPRINT",EDGE,{"derivedFrom":sQuery(id+"F7.wireOp",EDGE,"E299.0.17")}),1.0]])]});
            var Q3;
            Q3=makeQuery(id+"F7.imprint","IMPRINT",FACE,{"disambiguationData":[TD([[makeQuery(id+"F7.imprint","IMPRINT",EDGE,{"derivedFrom":sQuery(id+"F7.wireOp",EDGE,"E299.0.23")}),1.0]])]});
            var Q4;
            {var subQ0=sQuery(id+"F7.wireOp",EDGE,"E321.0");Q4=makeQuery(id+"F7.imprint","IMPRINT",FACE,{"disambiguationData":[TD([[makeQuery(id+"F7.imprint","IMPRINT",EDGE,{"derivedFrom":subQ0}),1.0]])]});}
            var Q5;
            Q5=makeQuery(id+"F7.imprint","IMPRINT",FACE,{"disambiguationData":[TD([[makeQuery(id+"F7.imprint","IMPRINT",EDGE,{"derivedFrom":sQuery(id+"F7.wireOp",EDGE,"E305.0")}),1.0]])]});
            var Q6;
            {var subQ0=sQuery(id+"F7.wireOp",EDGE,"E328.0");Q6=makeQuery(id+"F7.imprint","IMPRINT",FACE,{"disambiguationData":[TD([[makeQuery(id+"F7.imprint","IMPRINT",EDGE,{"derivedFrom":subQ0}),1.0]])]});}
            extrude(context, id + "F8", {"entities" : qUnion([Q0, Q1, Q2, Q3, Q4, Q5, Q6]), "operationType" : NewBodyOperationType.ADD, "oppositeDirection" : true, "depth" : 9.9 * mm});
        }
        {
            var Q0;
            Q0=makeQuery(id+"F0.imprint","IMPRINT",FACE,{"disambiguationData":[TD([[makeQuery(id+"F0.imprint","IMPRINT",EDGE,{"derivedFrom":sQuery(id+"F0.wireOp",EDGE,"E16")}),-1.0]])]});
            var Q1;
            Q1=makeQuery(id+"F0.imprint","IMPRINT",FACE,{"disambiguationData":[TD([[makeQuery(id+"F0.imprint","IMPRINT",EDGE,{"derivedFrom":sQuery(id+"F0.wireOp",EDGE,"E20")}),1.0]])]});
            extrude(context, id + "F9", {"entities" : qUnion([Q0, Q1]), "oppositeDirection" : true, "depth" : 220 * mm, "hasSecondDirection" : true, "secondDirectionOppositeDirection" : true, "secondDirectionDepth" : 55.1 * mm});
        }
        {
            var Q0;
            {var subQ0=sQuery(id+"F0.wireOp",EDGE,"E23");Q0=makeQuery(id+"F0.imprint","IMPRINT",FACE,{"disambiguationData":[TD([[makeQuery(id+"F0.imprint","IMPRINT",EDGE,{"derivedFrom":subQ0}),1.0]])]});}
            extrude(context, id + "F10", {"entities" : qUnion([Q0]), "operationType" : NewBodyOperationType.ADD, "oppositeDirection" : true, "depth" : 220 * mm, "hasSecondDirection" : true, "secondDirectionOppositeDirection" : true, "secondDirectionDepth" : 215 * mm});
        }
        {
            var Q0;
            Q0=makeQuery(id+"F10.opExtrude","SWEPT_FACE",FACE,{"disambiguationData":[OSD([sQuery(id+"F0.wireOp",EDGE,"E23")])]});
            var sketch = newSketch(context, id + "F11", { "sketchPlane" : qUnion([Q0])});
            skLineSegment(sketch, "E334.0.0", {"start": v(-32.24, -215) * mm, "end": v(-78.2, -215) * mm});
            skLineSegment(sketch, "E334.0.1", {"start": v(-78.2, -215) * mm, "end": v(-78.2, -220) * mm});
            skLineSegment(sketch, "E334.0.2", {"start": v(-78.2, -220) * mm, "end": v(-32.24, -220) * mm});
            skLineSegment(sketch, "E334.0.3", {"start": v(-32.24, -220) * mm, "end": v(-32.24, -215) * mm});
            skArc(sketch, "E335", {"start": v(-32.24, -215) * mm, "mid": v(-55.23, -192.94) * mm, "end": v(-78.2, -215) * mm});
            skSolve(sketch);
        }
        {
            var Q0;
            Q0=makeQuery(id+"F11.imprint","IMPRINT",FACE,{"disambiguationData":[TD([[makeQuery(id+"F11.imprint","IMPRINT",EDGE,{"derivedFrom":sQuery(id+"F11.wireOp",EDGE,"E334.0.0")}),1.0]])]});
            var Q1;
            Q1=makeQuery(id+"F11.imprint","IMPRINT",FACE,{"disambiguationData":[TD([[makeQuery(id+"F11.imprint","IMPRINT",EDGE,{"derivedFrom":sQuery(id+"F11.wireOp",EDGE,"E334.0.0")}),-1.0]])]});
            extrude(context, id + "F12", {"entities" : qUnion([Q0, Q1]), "operationType" : NewBodyOperationType.REMOVE, "depth" : 25 * mm});
        }
        {
            var Q0;
            Q0=makeQuery(id+"F12.boolean.opBoolean","INTERSECT",EDGE,{"derivedFrom":[makeQuery(id+"F9.opExtrude","SWEPT_FACE",FACE,{"disambiguationData":[OSD([sQuery(id+"F0.wireOp",EDGE,"E20")])]}),makeQuery(id+"F12.opExtrude","SWEPT_FACE",FACE,{"disambiguationData":[OSD([sQuery(id+"F11.wireOp",EDGE,"E334.0.3")])]})]});
            var Q1;
            Q1=makeQuery(id+"F12.boolean.opBoolean","INTERSECT",EDGE,{"derivedFrom":[makeQuery(id+"F9.opExtrude","SWEPT_FACE",FACE,{"disambiguationData":[OSD([sQuery(id+"F0.wireOp",EDGE,"E20")])]}),makeQuery(id+"F12.opExtrude","SWEPT_FACE",FACE,{"disambiguationData":[OSD([sQuery(id+"F11.wireOp",EDGE,"E335")])]})]});
            var Q2;
            Q2=makeQuery(id+"F12.boolean.opBoolean","INTERSECT",EDGE,{"derivedFrom":[makeQuery(id+"F9.opExtrude","SWEPT_FACE",FACE,{"disambiguationData":[OSD([sQuery(id+"F0.wireOp",EDGE,"E20")])]}),makeQuery(id+"F12.opExtrude","SWEPT_FACE",FACE,{"disambiguationData":[OSD([sQuery(id+"F11.wireOp",EDGE,"E334.0.1")])]})]});
            var Q3;
            Q3=makeQuery(id+"F12.boolean.opBoolean","MERGE",EDGE,{"derivedFrom":[makeQuery(id+"F10.opExtrude","SWEPT_EDGE",EDGE,{"disambiguationData":[OSD([sQuery(id+"F0.wireOp",EDGE,"E19"),sQuery(id+"F0.wireOp",EDGE,"E22"),sQuery(id+"F0.wireOp",EDGE,"E23")])]}),makeQuery(id+"F12.opExtrude","CAP_EDGE",EDGE,{"disambiguationData":[OSD([sQuery(id+"F11.wireOp",EDGE,"E334.0.1")])],"isStart":true})]});
            var Q4;
            Q4=makeQuery(id+"F12.boolean.opBoolean","MERGE",EDGE,{"derivedFrom":[makeQuery(id+"F10.opExtrude","SWEPT_EDGE",EDGE,{"disambiguationData":[OSD([sQuery(id+"F0.wireOp",EDGE,"E19"),sQuery(id+"F0.wireOp",EDGE,"E21"),sQuery(id+"F0.wireOp",EDGE,"E23")])]}),makeQuery(id+"F12.opExtrude","CAP_EDGE",EDGE,{"disambiguationData":[OSD([sQuery(id+"F11.wireOp",EDGE,"E334.0.3")])],"isStart":true})]});
            fillet(context, id + "F13", {"entities" : qUnion([Q0, Q1, Q2, Q3, Q4]), "radius" : 0.7 * mm, "tangentPropagation" : true, "allowEdgeOverflow" : false});
        }
        {
            var Q0;
            Q0=makeQuery(id+"F0.imprint","IMPRINT",FACE,{"disambiguationData":[TD([[makeQuery(id+"F0.imprint","IMPRINT",EDGE,{"derivedFrom":sQuery(id+"F0.wireOp",EDGE,"E13")}),1.0]])]});
            var Q1;
            {var subQ0=sQuery(id+"F0.wireOp",EDGE,"E9");var subQ1=sQuery(id+"F0.wireOp",EDGE,"E8");var subQ2=makeQuery(id+"F0.imprint","INTERSECT",VERTEX,{"derivedFrom":[subQ1,subQ0]});Q1=makeQuery(id+"F0.imprint","IMPRINT",FACE,{"disambiguationData":[TD([[makeQuery(id+"F0.imprint","IMPRINT",EDGE,{"disambiguationData":[TD([[subQ2,1.0]])],"derivedFrom":subQ1}),-1.0]])]});}
            var Q2;
            {var subQ1=sQuery(id+"F0.wireOp",EDGE,"E158.0");Q2=makeQuery(id+"F0.imprint","IMPRINT",FACE,{"disambiguationData":[TD([[makeQuery(id+"F0.imprint","IMPRINT",EDGE,{"derivedFrom":subQ1}),1.0]])]});}
            var Q3;
            {var subQ0=sQuery(id+"F0.wireOp",EDGE,"E279.filletArc");Q3=makeQuery(id+"F0.imprint","IMPRINT",FACE,{"disambiguationData":[TD([[makeQuery(id+"F0.imprint","IMPRINT",EDGE,{"derivedFrom":subQ0}),-1.0]])]});}
            extrude(context, id + "F14", {"entities" : qUnion([Q0, Q1, Q2, Q3]), "oppositeDirection" : true, "depth" : 220 * mm, "hasSecondDirection" : true, "secondDirectionOppositeDirection" : true, "secondDirectionDepth" : 100 * mm});
        }
        {
            var Q0;
            Q0=makeQuery(id+"F0.imprint","IMPRINT",FACE,{"disambiguationData":[TD([[makeQuery(id+"F0.imprint","IMPRINT",EDGE,{"derivedFrom":sQuery(id+"F0.wireOp",EDGE,"E117.top")}),-1.0]])]});
            var Q1;
            {var subQ0=sQuery(id+"F0.wireOp",EDGE,"E281.filletArc");Q1=makeQuery(id+"F0.imprint","IMPRINT",FACE,{"disambiguationData":[TD([[makeQuery(id+"F0.imprint","IMPRINT",EDGE,{"derivedFrom":subQ0}),-1.0]])]});}
            var Q2;
            {var subQ0=sQuery(id+"F0.wireOp",EDGE,"E284.filletArc");Q2=makeQuery(id+"F0.imprint","IMPRINT",FACE,{"disambiguationData":[TD([[makeQuery(id+"F0.imprint","IMPRINT",EDGE,{"derivedFrom":subQ0}),-1.0]])]});}
            var Q3;
            {var subQ0=sQuery(id+"F0.wireOp",EDGE,"E144.MirrorCS");Q3=makeQuery(id+"F0.imprint","IMPRINT",FACE,{"disambiguationData":[TD([[makeQuery(id+"F0.imprint","IMPRINT",EDGE,{"derivedFrom":subQ0}),1.0]])]});}
            var Q4;
            Q4=makeQuery(id+"F0.imprint","IMPRINT",FACE,{"disambiguationData":[TD([[makeQuery(id+"F0.imprint","IMPRINT",EDGE,{"derivedFrom":sQuery(id+"F0.wireOp",EDGE,"E145.MirrorCS")}),-1.0]])]});
            var Q5;
            {var subQ0=sQuery(id+"F0.wireOp",EDGE,"E134.MirrorCS");Q5=makeQuery(id+"F0.imprint","IMPRINT",FACE,{"disambiguationData":[TD([[makeQuery(id+"F0.imprint","IMPRINT",EDGE,{"derivedFrom":subQ0}),1.0]])]});}
            var Q6;
            Q6=makeQuery(id+"F0.imprint","IMPRINT",FACE,{"disambiguationData":[TD([[makeQuery(id+"F0.imprint","IMPRINT",EDGE,{"derivedFrom":sQuery(id+"F0.wireOp",EDGE,"E135.MirrorCS")}),-1.0]])]});
            var Q7;
            Q7=makeQuery(id+"F0.imprint","IMPRINT",FACE,{"disambiguationData":[TD([[makeQuery(id+"F0.imprint","IMPRINT",EDGE,{"derivedFrom":sQuery(id+"F0.wireOp",EDGE,"E117.bottom")}),1.0]])]});
            var Q8;
            Q8=makeQuery(id+"F0.imprint","IMPRINT",FACE,{"disambiguationData":[TD([[makeQuery(id+"F0.imprint","IMPRINT",EDGE,{"derivedFrom":sQuery(id+"F0.wireOp",EDGE,"E117.bottom")}),-1.0]])]});
            var Q9;
            Q9=makeQuery(id+"F0.imprint","IMPRINT",FACE,{"disambiguationData":[TD([[makeQuery(id+"F0.imprint","IMPRINT",EDGE,{"derivedFrom":sQuery(id+"F0.wireOp",EDGE,"E122.bottom")}),1.0]])]});
            var Q10;
            Q10=makeQuery(id+"F0.imprint","IMPRINT",FACE,{"disambiguationData":[TD([[makeQuery(id+"F0.imprint","IMPRINT",EDGE,{"derivedFrom":sQuery(id+"F0.wireOp",EDGE,"E122.bottom")}),-1.0]])]});
            extrude(context, id + "F15", {"entities" : qUnion([Q0, Q1, Q2, Q3, Q4, Q5, Q6, Q7, Q8, Q9, Q10]), "operationType" : NewBodyOperationType.ADD, "oppositeDirection" : true, "depth" : 220 * mm, "hasSecondDirection" : true, "secondDirectionOppositeDirection" : true, "secondDirectionDepth" : 217 * mm});
        }
        {
            var Q0;
            {var subQ0=sQuery(id+"F0.wireOp",EDGE,"E144.MirrorCS");Q0=makeQuery(id+"F0.imprint","IMPRINT",FACE,{"disambiguationData":[TD([[makeQuery(id+"F0.imprint","IMPRINT",EDGE,{"derivedFrom":subQ0}),1.0]])]});}
            var Q1;
            Q1=makeQuery(id+"F0.imprint","IMPRINT",FACE,{"disambiguationData":[TD([[makeQuery(id+"F0.imprint","IMPRINT",EDGE,{"derivedFrom":sQuery(id+"F0.wireOp",EDGE,"E145.MirrorCS")}),-1.0]])]});
            var Q2;
            {var subQ0=sQuery(id+"F0.wireOp",EDGE,"E134.MirrorCS");Q2=makeQuery(id+"F0.imprint","IMPRINT",FACE,{"disambiguationData":[TD([[makeQuery(id+"F0.imprint","IMPRINT",EDGE,{"derivedFrom":subQ0}),1.0]])]});}
            var Q3;
            Q3=makeQuery(id+"F0.imprint","IMPRINT",FACE,{"disambiguationData":[TD([[makeQuery(id+"F0.imprint","IMPRINT",EDGE,{"derivedFrom":sQuery(id+"F0.wireOp",EDGE,"E135.MirrorCS")}),-1.0]])]});
            var Q4;
            Q4=makeQuery(id+"F0.imprint","IMPRINT",FACE,{"disambiguationData":[TD([[makeQuery(id+"F0.imprint","IMPRINT",EDGE,{"derivedFrom":sQuery(id+"F0.wireOp",EDGE,"E117.bottom")}),1.0]])]});
            var Q5;
            Q5=makeQuery(id+"F0.imprint","IMPRINT",FACE,{"disambiguationData":[TD([[makeQuery(id+"F0.imprint","IMPRINT",EDGE,{"derivedFrom":sQuery(id+"F0.wireOp",EDGE,"E117.bottom")}),-1.0]])]});
            var Q6;
            Q6=makeQuery(id+"F0.imprint","IMPRINT",FACE,{"disambiguationData":[TD([[makeQuery(id+"F0.imprint","IMPRINT",EDGE,{"derivedFrom":sQuery(id+"F0.wireOp",EDGE,"E122.bottom")}),1.0]])]});
            var Q7;
            Q7=makeQuery(id+"F0.imprint","IMPRINT",FACE,{"disambiguationData":[TD([[makeQuery(id+"F0.imprint","IMPRINT",EDGE,{"derivedFrom":sQuery(id+"F0.wireOp",EDGE,"E122.bottom")}),-1.0]])]});
            extrude(context, id + "F16", {"entities" : qUnion([Q0, Q1, Q2, Q3, Q4, Q5, Q6, Q7]), "operationType" : NewBodyOperationType.ADD, "oppositeDirection" : true, "depth" : 145 * mm, "hasSecondDirection" : true, "secondDirectionOppositeDirection" : true, "secondDirectionDepth" : 140 * mm});
        }
        {
            var Q0;
            Q0=makeQuery(id+"F0.imprint","IMPRINT",FACE,{"disambiguationData":[TD([[makeQuery(id+"F0.imprint","IMPRINT",EDGE,{"derivedFrom":sQuery(id+"F0.wireOp",EDGE,"E145.MirrorCS")}),-1.0]])]});
            var Q1;
            Q1=makeQuery(id+"F0.imprint","IMPRINT",FACE,{"disambiguationData":[TD([[makeQuery(id+"F0.imprint","IMPRINT",EDGE,{"derivedFrom":sQuery(id+"F0.wireOp",EDGE,"E135.MirrorCS")}),-1.0]])]});
            var Q2;
            Q2=makeQuery(id+"F0.imprint","IMPRINT",FACE,{"disambiguationData":[TD([[makeQuery(id+"F0.imprint","IMPRINT",EDGE,{"derivedFrom":sQuery(id+"F0.wireOp",EDGE,"E117.bottom")}),-1.0]])]});
            var Q3;
            Q3=makeQuery(id+"F0.imprint","IMPRINT",FACE,{"disambiguationData":[TD([[makeQuery(id+"F0.imprint","IMPRINT",EDGE,{"derivedFrom":sQuery(id+"F0.wireOp",EDGE,"E122.bottom")}),-1.0]])]});
            extrude(context, id + "F17", {"entities" : qUnion([Q0, Q1, Q2, Q3]), "operationType" : NewBodyOperationType.ADD, "oppositeDirection" : true, "depth" : 140 * mm, "hasSecondDirection" : true, "secondDirectionOppositeDirection" : true, "secondDirectionDepth" : 130 * mm});
        }
        {
            var Q0;
            {var subQ0=sQuery(id+"F0.wireOp",EDGE,"E116.1");Q0=makeQuery(id+"F16.opExtrude","CAP_EDGE",EDGE,{"disambiguationData":[OSD([subQ0]),TDD([makeQuery(id+"F0.imprint","IMPRINT",EDGE,{"disambiguationData":[TD([[makeQuery(id+"F0.imprint","INTERSECT",VERTEX,{"derivedFrom":[subQ0,sQuery(id+"F0.wireOp",EDGE,"E144.MirrorCS")]}),1.0]])],"derivedFrom":subQ0})])],"isStart":false});}
            var Q1;
            {var subQ0=sQuery(id+"F0.wireOp",EDGE,"E116.1");Q1=makeQuery(id+"F16.opExtrude","CAP_EDGE",EDGE,{"disambiguationData":[OSD([subQ0]),TDD([makeQuery(id+"F0.imprint","IMPRINT",EDGE,{"disambiguationData":[TD([[makeQuery(id+"F0.imprint","INTERSECT",VERTEX,{"derivedFrom":[subQ0,sQuery(id+"F0.wireOp",EDGE,"E134.MirrorCS")]}),1.0]])],"derivedFrom":subQ0})])],"isStart":false});}
            var Q2;
            {var subQ0=sQuery(id+"F0.wireOp",EDGE,"E116.1");Q2=makeQuery(id+"F16.opExtrude","CAP_EDGE",EDGE,{"disambiguationData":[OSD([subQ0]),TDD([makeQuery(id+"F0.imprint","IMPRINT",EDGE,{"disambiguationData":[TD([[makeQuery(id+"F0.imprint","INTERSECT",VERTEX,{"derivedFrom":[subQ0,sQuery(id+"F0.wireOp",EDGE,"E127")]}),-1.0]])],"derivedFrom":subQ0})])],"isStart":false});}
            var Q3;
            {var subQ0=sQuery(id+"F0.wireOp",EDGE,"E116.1");Q3=makeQuery(id+"F16.opExtrude","CAP_EDGE",EDGE,{"disambiguationData":[OSD([subQ0]),TDD([makeQuery(id+"F0.imprint","IMPRINT",EDGE,{"disambiguationData":[TD([[makeQuery(id+"F0.imprint","INTERSECT",VERTEX,{"derivedFrom":[subQ0,sQuery(id+"F0.wireOp",EDGE,"E129")]}),-1.0]])],"derivedFrom":subQ0})])],"isStart":false});}
            var Q4;
            Q4=makeQuery(id+"F16.opExtrude","CAP_EDGE",EDGE,{"disambiguationData":[OSD([sQuery(id+"F0.wireOp",EDGE,"E144.MirrorCS"),sQuery(id+"F0.wireOp",EDGE,"E146.MirrorCS")])],"isStart":false});
            var Q5;
            Q5=makeQuery(id+"F16.opExtrude","CAP_EDGE",EDGE,{"disambiguationData":[OSD([sQuery(id+"F0.wireOp",EDGE,"E134.MirrorCS"),sQuery(id+"F0.wireOp",EDGE,"E136.MirrorCS")])],"isStart":false});
            var Q6;
            Q6=makeQuery(id+"F16.opExtrude","CAP_EDGE",EDGE,{"disambiguationData":[OSD([sQuery(id+"F0.wireOp",EDGE,"E117.right"),sQuery(id+"F0.wireOp",EDGE,"E128")])],"isStart":false});
            var Q7;
            Q7=makeQuery(id+"F16.opExtrude","CAP_EDGE",EDGE,{"disambiguationData":[OSD([sQuery(id+"F0.wireOp",EDGE,"E122.right"),sQuery(id+"F0.wireOp",EDGE,"E130")])],"isStart":false});
            var Q8;
            Q8=makeQuery(id+"F17.opExtrude","CAP_EDGE",EDGE,{"disambiguationData":[OSD([sQuery(id+"F0.wireOp",EDGE,"E148.MirrorCS")])],"isStart":true});
            var Q9;
            Q9=makeQuery(id+"F17.opExtrude","CAP_EDGE",EDGE,{"disambiguationData":[OSD([sQuery(id+"F0.wireOp",EDGE,"E138.MirrorCS")])],"isStart":true});
            var Q10;
            Q10=makeQuery(id+"F17.opExtrude","CAP_EDGE",EDGE,{"disambiguationData":[OSD([sQuery(id+"F0.wireOp",EDGE,"E117.top")])],"isStart":true});
            var Q11;
            Q11=makeQuery(id+"F17.opExtrude","CAP_EDGE",EDGE,{"disambiguationData":[OSD([sQuery(id+"F0.wireOp",EDGE,"E122.top")])],"isStart":true});
            var Q12;
            Q12=makeQuery(id+"F17.opExtrude","CAP_EDGE",EDGE,{"disambiguationData":[OSD([sQuery(id+"F0.wireOp",EDGE,"E152.MirrorCS")])],"isStart":false});
            var Q13;
            Q13=makeQuery(id+"F17.opExtrude","CAP_EDGE",EDGE,{"disambiguationData":[OSD([sQuery(id+"F0.wireOp",EDGE,"E139.MirrorCS")])],"isStart":false});
            var Q14;
            Q14=makeQuery(id+"F17.opExtrude","CAP_EDGE",EDGE,{"disambiguationData":[OSD([sQuery(id+"F0.wireOp",EDGE,"E117.bottom")])],"isStart":false});
            var Q15;
            Q15=makeQuery(id+"F17.opExtrude","CAP_EDGE",EDGE,{"disambiguationData":[OSD([sQuery(id+"F0.wireOp",EDGE,"E122.bottom")])],"isStart":false});
            var Q16;
            {var subQ0=sQuery(id+"F0.wireOp",EDGE,"E116.1");Q16=makeQuery(id+"F16.opExtrude","CAP_EDGE",EDGE,{"disambiguationData":[OSD([subQ0]),TDD([makeQuery(id+"F0.imprint","IMPRINT",EDGE,{"disambiguationData":[TD([[makeQuery(id+"F0.imprint","INTERSECT",VERTEX,{"derivedFrom":[subQ0,sQuery(id+"F0.wireOp",EDGE,"E144.MirrorCS")]}),1.0]])],"derivedFrom":subQ0})])],"isStart":true});}
            var Q17;
            {var subQ0=sQuery(id+"F0.wireOp",EDGE,"E116.1");Q17=makeQuery(id+"F16.opExtrude","CAP_EDGE",EDGE,{"disambiguationData":[OSD([subQ0]),TDD([makeQuery(id+"F0.imprint","IMPRINT",EDGE,{"disambiguationData":[TD([[makeQuery(id+"F0.imprint","INTERSECT",VERTEX,{"derivedFrom":[subQ0,sQuery(id+"F0.wireOp",EDGE,"E134.MirrorCS")]}),1.0]])],"derivedFrom":subQ0})])],"isStart":true});}
            var Q18;
            {var subQ0=sQuery(id+"F0.wireOp",EDGE,"E116.1");Q18=makeQuery(id+"F16.opExtrude","CAP_EDGE",EDGE,{"disambiguationData":[OSD([subQ0]),TDD([makeQuery(id+"F0.imprint","IMPRINT",EDGE,{"disambiguationData":[TD([[makeQuery(id+"F0.imprint","INTERSECT",VERTEX,{"derivedFrom":[subQ0,sQuery(id+"F0.wireOp",EDGE,"E127")]}),-1.0]])],"derivedFrom":subQ0})])],"isStart":true});}
            var Q19;
            {var subQ0=sQuery(id+"F0.wireOp",EDGE,"E116.1");Q19=makeQuery(id+"F16.opExtrude","CAP_EDGE",EDGE,{"disambiguationData":[OSD([subQ0]),TDD([makeQuery(id+"F0.imprint","IMPRINT",EDGE,{"disambiguationData":[TD([[makeQuery(id+"F0.imprint","INTERSECT",VERTEX,{"derivedFrom":[subQ0,sQuery(id+"F0.wireOp",EDGE,"E129")]}),-1.0]])],"derivedFrom":subQ0})])],"isStart":true});}
            fillet(context, id + "F18", {"entities" : qUnion([Q0, Q1, Q2, Q3, Q4, Q5, Q6, Q7, Q8, Q9, Q10, Q11, Q12, Q13, Q14, Q15, Q16, Q17, Q18, Q19]), "radius" : 1 * mm, "tangentPropagation" : true, "allowEdgeOverflow" : false});
        }
        {
            var Q0;
            Q0=makeQuery(id+"F0.imprint","IMPRINT",FACE,{"disambiguationData":[TD([[makeQuery(id+"F0.imprint","IMPRINT",EDGE,{"derivedFrom":sQuery(id+"F0.wireOp",EDGE,"E13")}),1.0]])]});
            var Q1;
            {var subQ0=sQuery(id+"F0.wireOp",EDGE,"E9");var subQ1=sQuery(id+"F0.wireOp",EDGE,"E8");var subQ2=makeQuery(id+"F0.imprint","INTERSECT",VERTEX,{"derivedFrom":[subQ1,subQ0]});Q1=makeQuery(id+"F0.imprint","IMPRINT",FACE,{"disambiguationData":[TD([[makeQuery(id+"F0.imprint","IMPRINT",EDGE,{"disambiguationData":[TD([[subQ2,1.0]])],"derivedFrom":subQ1}),-1.0]])]});}
            var Q2;
            {var subQ1=sQuery(id+"F0.wireOp",EDGE,"E158.0");Q2=makeQuery(id+"F0.imprint","IMPRINT",FACE,{"disambiguationData":[TD([[makeQuery(id+"F0.imprint","IMPRINT",EDGE,{"derivedFrom":subQ1}),1.0]])]});}
            var Q3;
            {var subQ0=sQuery(id+"F0.wireOp",EDGE,"E279.filletArc");Q3=makeQuery(id+"F0.imprint","IMPRINT",FACE,{"disambiguationData":[TD([[makeQuery(id+"F0.imprint","IMPRINT",EDGE,{"derivedFrom":subQ0}),-1.0]])]});}
            extrude(context, id + "F19", {"entities" : qUnion([Q0, Q1, Q2, Q3]), "oppositeDirection" : true, "depth" : 99.9 * mm, "hasSecondDirection" : true, "secondDirectionOppositeDirection" : true, "secondDirectionDepth" : 15.1 * mm});
        }
        {
            var Q0;
            Q0=makeQuery(id+"F0.imprint","IMPRINT",FACE,{"disambiguationData":[TD([[makeQuery(id+"F0.imprint","IMPRINT",EDGE,{"derivedFrom":sQuery(id+"F0.wireOp",EDGE,"E117.top")}),-1.0]])]});
            var Q1;
            {var subQ0=sQuery(id+"F0.wireOp",EDGE,"E284.filletArc");Q1=makeQuery(id+"F0.imprint","IMPRINT",FACE,{"disambiguationData":[TD([[makeQuery(id+"F0.imprint","IMPRINT",EDGE,{"derivedFrom":subQ0}),-1.0]])]});}
            var Q2;
            {var subQ0=sQuery(id+"F0.wireOp",EDGE,"E281.filletArc");Q2=makeQuery(id+"F0.imprint","IMPRINT",FACE,{"disambiguationData":[TD([[makeQuery(id+"F0.imprint","IMPRINT",EDGE,{"derivedFrom":subQ0}),-1.0]])]});}
            var Q3;
            Q3=makeQuery(id+"F0.imprint","IMPRINT",FACE,{"disambiguationData":[TD([[makeQuery(id+"F0.imprint","IMPRINT",EDGE,{"derivedFrom":sQuery(id+"F0.wireOp",EDGE,"E122.bottom")}),1.0]])]});
            var Q4;
            Q4=makeQuery(id+"F0.imprint","IMPRINT",FACE,{"disambiguationData":[TD([[makeQuery(id+"F0.imprint","IMPRINT",EDGE,{"derivedFrom":sQuery(id+"F0.wireOp",EDGE,"E122.bottom")}),-1.0]])]});
            var Q5;
            Q5=makeQuery(id+"F0.imprint","IMPRINT",FACE,{"disambiguationData":[TD([[makeQuery(id+"F0.imprint","IMPRINT",EDGE,{"derivedFrom":sQuery(id+"F0.wireOp",EDGE,"E117.bottom")}),1.0]])]});
            var Q6;
            Q6=makeQuery(id+"F0.imprint","IMPRINT",FACE,{"disambiguationData":[TD([[makeQuery(id+"F0.imprint","IMPRINT",EDGE,{"derivedFrom":sQuery(id+"F0.wireOp",EDGE,"E117.bottom")}),-1.0]])]});
            var Q7;
            {var subQ0=sQuery(id+"F0.wireOp",EDGE,"E134.MirrorCS");Q7=makeQuery(id+"F0.imprint","IMPRINT",FACE,{"disambiguationData":[TD([[makeQuery(id+"F0.imprint","IMPRINT",EDGE,{"derivedFrom":subQ0}),1.0]])]});}
            var Q8;
            Q8=makeQuery(id+"F0.imprint","IMPRINT",FACE,{"disambiguationData":[TD([[makeQuery(id+"F0.imprint","IMPRINT",EDGE,{"derivedFrom":sQuery(id+"F0.wireOp",EDGE,"E135.MirrorCS")}),-1.0]])]});
            var Q9;
            {var subQ0=sQuery(id+"F0.wireOp",EDGE,"E144.MirrorCS");Q9=makeQuery(id+"F0.imprint","IMPRINT",FACE,{"disambiguationData":[TD([[makeQuery(id+"F0.imprint","IMPRINT",EDGE,{"derivedFrom":subQ0}),1.0]])]});}
            var Q10;
            Q10=makeQuery(id+"F0.imprint","IMPRINT",FACE,{"disambiguationData":[TD([[makeQuery(id+"F0.imprint","IMPRINT",EDGE,{"derivedFrom":sQuery(id+"F0.wireOp",EDGE,"E145.MirrorCS")}),-1.0]])]});
            extrude(context, id + "F20", {"entities" : qUnion([Q0, Q1, Q2, Q3, Q4, Q5, Q6, Q7, Q8, Q9, Q10]), "operationType" : NewBodyOperationType.ADD, "oppositeDirection" : true, "depth" : 99.9 * mm, "hasSecondDirection" : true, "secondDirectionOppositeDirection" : true, "secondDirectionDepth" : 96.9 * mm});
        }
        {
            var Q0;
            Q0=makeQuery(id+"F0.imprint","IMPRINT",FACE,{"disambiguationData":[TD([[makeQuery(id+"F0.imprint","IMPRINT",EDGE,{"derivedFrom":sQuery(id+"F0.wireOp",EDGE,"E11")}),-1.0]])]});
            var Q1;
            {var subQ4=sQuery(id+"F0.wireOp",EDGE,"E155.0");Q1=makeQuery(id+"F0.imprint","IMPRINT",FACE,{"disambiguationData":[TD([[makeQuery(id+"F0.imprint","IMPRINT",EDGE,{"derivedFrom":subQ4}),1.0]])]});}
            var Q2;
            {var subQ0=sQuery(id+"F0.wireOp",EDGE,"E232");Q2=makeQuery(id+"F0.imprint","IMPRINT",FACE,{"disambiguationData":[TD([[makeQuery(id+"F0.imprint","IMPRINT",EDGE,{"derivedFrom":subQ0}),1.0]])]});}
            var Q3;
            {var subQ1=sQuery(id+"F0.wireOp",EDGE,"E235");Q3=makeQuery(id+"F0.imprint","IMPRINT",FACE,{"disambiguationData":[TD([[makeQuery(id+"F0.imprint","IMPRINT",EDGE,{"derivedFrom":subQ1}),-1.0]])]});}
            var Q4;
            {var subQ1=sQuery(id+"F0.wireOp",EDGE,"E239");Q4=makeQuery(id+"F0.imprint","IMPRINT",FACE,{"disambiguationData":[TD([[makeQuery(id+"F0.imprint","IMPRINT",EDGE,{"derivedFrom":subQ1}),-1.0]])]});}
            var Q5;
            {var subQ0=sQuery(id+"F0.wireOp",EDGE,"E278.filletArc");Q5=makeQuery(id+"F0.imprint","IMPRINT",FACE,{"disambiguationData":[TD([[makeQuery(id+"F0.imprint","IMPRINT",EDGE,{"derivedFrom":subQ0}),-1.0]])]});}
            var Q6;
            {var subQ0=sQuery(id+"F0.wireOp",EDGE,"E254.filletArc");Q6=makeQuery(id+"F0.imprint","IMPRINT",FACE,{"disambiguationData":[TD([[makeQuery(id+"F0.imprint","IMPRINT",EDGE,{"derivedFrom":subQ0}),-1.0]])]});}
            var Q7;
            Q7=makeQuery(id+"F0.imprint","IMPRINT",FACE,{"disambiguationData":[TD([[makeQuery(id+"F0.imprint","IMPRINT",EDGE,{"derivedFrom":sQuery(id+"F0.wireOp",EDGE,"E237")}),1.0]])]});
            var Q8;
            Q8=makeQuery(id+"F0.imprint","IMPRINT",FACE,{"disambiguationData":[TD([[makeQuery(id+"F0.imprint","IMPRINT",EDGE,{"derivedFrom":sQuery(id+"F0.wireOp",EDGE,"E238")}),1.0]])]});
            var Q9;
            Q9=makeQuery(id+"F0.imprint","IMPRINT",FACE,{"disambiguationData":[TD([[makeQuery(id+"F0.imprint","IMPRINT",EDGE,{"derivedFrom":sQuery(id+"F0.wireOp",EDGE,"E234")}),1.0]])]});
            var Q10;
            Q10=makeQuery(id+"F0.imprint","IMPRINT",FACE,{"disambiguationData":[TD([[makeQuery(id+"F0.imprint","IMPRINT",EDGE,{"derivedFrom":sQuery(id+"F0.wireOp",EDGE,"E233")}),1.0]])]});
            extrude(context, id + "F21", {"entities" : qUnion([Q0, Q1, Q2, Q3, Q4, Q5, Q6, Q7, Q8, Q9, Q10]), "oppositeDirection" : true, "depth" : 220 * mm, "hasSecondDirection" : true, "secondDirectionOppositeDirection" : true, "secondDirectionDepth" : 151.77 * mm});
        }
        {
            var Q0;
            Q0=makeQuery(id+"F0.imprint","IMPRINT",FACE,{"disambiguationData":[TD([[makeQuery(id+"F0.imprint","IMPRINT",EDGE,{"derivedFrom":sQuery(id+"F0.wireOp",EDGE,"E233")}),1.0]])]});
            var Q1;
            Q1=makeQuery(id+"F0.imprint","IMPRINT",FACE,{"disambiguationData":[TD([[makeQuery(id+"F0.imprint","IMPRINT",EDGE,{"derivedFrom":sQuery(id+"F0.wireOp",EDGE,"E234")}),1.0]])]});
            var Q2;
            Q2=makeQuery(id+"F0.imprint","IMPRINT",FACE,{"disambiguationData":[TD([[makeQuery(id+"F0.imprint","IMPRINT",EDGE,{"derivedFrom":sQuery(id+"F0.wireOp",EDGE,"E237")}),1.0]])]});
            var Q3;
            Q3=makeQuery(id+"F0.imprint","IMPRINT",FACE,{"disambiguationData":[TD([[makeQuery(id+"F0.imprint","IMPRINT",EDGE,{"derivedFrom":sQuery(id+"F0.wireOp",EDGE,"E238")}),1.0]])]});
            extrude(context, id + "F22", {"entities" : qUnion([Q0, Q1, Q2, Q3]), "operationType" : NewBodyOperationType.REMOVE, "oppositeDirection" : true, "depth" : 220 * mm, "hasSecondDirection" : true, "secondDirectionOppositeDirection" : true, "secondDirectionDepth" : 215 * mm});
        }
        {
            var Q0;
            Q0=makeQuery(id+"F0.imprint","IMPRINT",FACE,{"disambiguationData":[TD([[makeQuery(id+"F0.imprint","IMPRINT",EDGE,{"derivedFrom":sQuery(id+"F0.wireOp",EDGE,"E238")}),1.0]])]});
            var Q1;
            Q1=makeQuery(id+"F0.imprint","IMPRINT",FACE,{"disambiguationData":[TD([[makeQuery(id+"F0.imprint","IMPRINT",EDGE,{"derivedFrom":sQuery(id+"F0.wireOp",EDGE,"E234")}),1.0]])]});
            var Q2;
            Q2=makeQuery(id+"F21.opExtrude","CAP_FACE",FACE,{"disambiguationData":[OSD([sQuery(id+"F0.wireOp",EDGE,"E5"),sQuery(id+"F0.wireOp",EDGE,"E6"),sQuery(id+"F0.wireOp",EDGE,"E10"),sQuery(id+"F0.wireOp",EDGE,"E11"),sQuery(id+"F0.wireOp",EDGE,"E157.0"),sQuery(id+"F0.wireOp",EDGE,"E159"),sQuery(id+"F0.wireOp",EDGE,"E163"),sQuery(id+"F0.wireOp",EDGE,"E164"),sQuery(id+"F0.wireOp",EDGE,"E166.MirrorCS"),sQuery(id+"F0.wireOp",EDGE,"E167.MirrorCS"),sQuery(id+"F0.wireOp",EDGE,"E168.MirrorCS"),sQuery(id+"F0.wireOp",EDGE,"E172.trimOffspring"),sQuery(id+"F0.wireOp",EDGE,"E173.trimOffspring"),sQuery(id+"F0.wireOp",EDGE,"E175"),sQuery(id+"F0.wireOp",EDGE,"E179"),sQuery(id+"F0.wireOp",EDGE,"E180"),sQuery(id+"F0.wireOp",EDGE,"E182.MirrorCS"),sQuery(id+"F0.wireOp",EDGE,"E183.MirrorCS"),sQuery(id+"F0.wireOp",EDGE,"E184.MirrorCS"),sQuery(id+"F0.wireOp",EDGE,"E190.trimOffspring"),sQuery(id+"F0.wireOp",EDGE,"E236"),sQuery(id+"F0.wireOp",EDGE,"E239"),sQuery(id+"F0.wireOp",EDGE,"E252.filletArc"),sQuery(id+"F0.wireOp",EDGE,"E273"),sQuery(id+"F0.wireOp",EDGE,"E274.filletArc"),sQuery(id+"F0.wireOp",EDGE,"E275.filletArc"),sQuery(id+"F0.wireOp",EDGE,"E294"),sQuery(id+"F0.wireOp",EDGE,"E295")])],"isStart":true});
            extrude(context, id + "F23", {"entities" : qUnion([Q0, Q1]), "operationType" : NewBodyOperationType.ADD, "oppositeDirection" : true, "endBoundEntityFace" : qUnion([Q2]), "depth" : 151.77 * mm, "hasSecondDirection" : true, "secondDirectionOppositeDirection" : true, "secondDirectionDepth" : 147.77 * mm});
        }
        {
            var Q0;
            Q0=makeQuery(id+"F0.imprint","IMPRINT",FACE,{"disambiguationData":[TD([[makeQuery(id+"F0.imprint","IMPRINT",EDGE,{"derivedFrom":sQuery(id+"F0.wireOp",EDGE,"E156.trimOffspring")}),-1.0]])]});
            var Q1;
            {var subQ0=sQuery(id+"F0.wireOp",EDGE,"E276.filletArc");Q1=makeQuery(id+"F0.imprint","IMPRINT",FACE,{"disambiguationData":[TD([[makeQuery(id+"F0.imprint","IMPRINT",EDGE,{"derivedFrom":subQ0}),-1.0]])]});}
            var Q2;
            {var subQ0=sQuery(id+"F0.wireOp",EDGE,"E254.filletArc");Q2=makeQuery(id+"F0.imprint","IMPRINT",FACE,{"disambiguationData":[TD([[makeQuery(id+"F0.imprint","IMPRINT",EDGE,{"derivedFrom":subQ0}),-1.0]])]});}
            var Q3;
            {var subQ0=sQuery(id+"F0.wireOp",EDGE,"E253.filletArc");Q3=makeQuery(id+"F0.imprint","IMPRINT",FACE,{"disambiguationData":[TD([[makeQuery(id+"F0.imprint","IMPRINT",EDGE,{"derivedFrom":subQ0}),-1.0]])]});}
            extrude(context, id + "F24", {"entities" : qUnion([Q0, Q1, Q2, Q3]), "operationType" : NewBodyOperationType.ADD, "oppositeDirection" : true, "depth" : 220 * mm, "hasSecondDirection" : true, "secondDirectionOppositeDirection" : true, "secondDirectionDepth" : 217 * mm});
        }
        {
            var Q0;
            Q0=makeQuery(id+"F21.opExtrude","SWEPT_BODY",BODY,{"disambiguationData":[OSD([sQuery(id+"F0.wireOp",EDGE,"E5"),sQuery(id+"F0.wireOp",EDGE,"E6"),sQuery(id+"F0.wireOp",EDGE,"E10"),sQuery(id+"F0.wireOp",EDGE,"E11"),sQuery(id+"F0.wireOp",EDGE,"E157.0"),sQuery(id+"F0.wireOp",EDGE,"E159"),sQuery(id+"F0.wireOp",EDGE,"E163"),sQuery(id+"F0.wireOp",EDGE,"E164"),sQuery(id+"F0.wireOp",EDGE,"E166.MirrorCS"),sQuery(id+"F0.wireOp",EDGE,"E167.MirrorCS"),sQuery(id+"F0.wireOp",EDGE,"E168.MirrorCS"),sQuery(id+"F0.wireOp",EDGE,"E172.trimOffspring"),sQuery(id+"F0.wireOp",EDGE,"E173.trimOffspring"),sQuery(id+"F0.wireOp",EDGE,"E175"),sQuery(id+"F0.wireOp",EDGE,"E179"),sQuery(id+"F0.wireOp",EDGE,"E180"),sQuery(id+"F0.wireOp",EDGE,"E182.MirrorCS"),sQuery(id+"F0.wireOp",EDGE,"E183.MirrorCS"),sQuery(id+"F0.wireOp",EDGE,"E184.MirrorCS"),sQuery(id+"F0.wireOp",EDGE,"E190.trimOffspring"),sQuery(id+"F0.wireOp",EDGE,"E236"),sQuery(id+"F0.wireOp",EDGE,"E239"),sQuery(id+"F0.wireOp",EDGE,"E252.filletArc"),sQuery(id+"F0.wireOp",EDGE,"E273"),sQuery(id+"F0.wireOp",EDGE,"E274.filletArc"),sQuery(id+"F0.wireOp",EDGE,"E275.filletArc"),sQuery(id+"F0.wireOp",EDGE,"E294"),sQuery(id+"F0.wireOp",EDGE,"E295")])]});
            transform(context, id + "F25", {"entities" : qUnion([Q0]), "transformType" : TransformType.TRANSLATION_3D, "dx" : 0 * mm, "dy" : 0 * mm, "dz" : 68.33 * mm, "makeCopy" : true});
        }
        {
            var Q0;
            Q0=makeQuery(id+"F25.opPattern","COPY",BODY,{"derivedFrom":makeQuery(id+"F21.opExtrude","SWEPT_BODY",BODY,{"disambiguationData":[OSD([sQuery(id+"F0.wireOp",EDGE,"E5"),sQuery(id+"F0.wireOp",EDGE,"E6"),sQuery(id+"F0.wireOp",EDGE,"E10"),sQuery(id+"F0.wireOp",EDGE,"E11"),sQuery(id+"F0.wireOp",EDGE,"E157.0"),sQuery(id+"F0.wireOp",EDGE,"E159"),sQuery(id+"F0.wireOp",EDGE,"E163"),sQuery(id+"F0.wireOp",EDGE,"E164"),sQuery(id+"F0.wireOp",EDGE,"E166.MirrorCS"),sQuery(id+"F0.wireOp",EDGE,"E167.MirrorCS"),sQuery(id+"F0.wireOp",EDGE,"E168.MirrorCS"),sQuery(id+"F0.wireOp",EDGE,"E172.trimOffspring"),sQuery(id+"F0.wireOp",EDGE,"E173.trimOffspring"),sQuery(id+"F0.wireOp",EDGE,"E175"),sQuery(id+"F0.wireOp",EDGE,"E179"),sQuery(id+"F0.wireOp",EDGE,"E180"),sQuery(id+"F0.wireOp",EDGE,"E182.MirrorCS"),sQuery(id+"F0.wireOp",EDGE,"E183.MirrorCS"),sQuery(id+"F0.wireOp",EDGE,"E184.MirrorCS"),sQuery(id+"F0.wireOp",EDGE,"E190.trimOffspring"),sQuery(id+"F0.wireOp",EDGE,"E236"),sQuery(id+"F0.wireOp",EDGE,"E239"),sQuery(id+"F0.wireOp",EDGE,"E252.filletArc"),sQuery(id+"F0.wireOp",EDGE,"E273"),sQuery(id+"F0.wireOp",EDGE,"E274.filletArc"),sQuery(id+"F0.wireOp",EDGE,"E275.filletArc"),sQuery(id+"F0.wireOp",EDGE,"E294"),sQuery(id+"F0.wireOp",EDGE,"E295")])]}),"instanceName":"1"});
            transform(context, id + "F26", {"entities" : qUnion([Q0]), "transformType" : TransformType.TRANSLATION_3D, "dx" : 0 * mm, "dy" : 0 * mm, "dz" : 68.33 * mm, "makeCopy" : true});
        }
        {
            var Q0;
            Q0=makeQuery(id+"F0.imprint","IMPRINT",FACE,{"disambiguationData":[TD([[makeQuery(id+"F0.imprint","IMPRINT",EDGE,{"derivedFrom":sQuery(id+"F0.wireOp",EDGE,"E87.0")}),1.0]])]});
            var Q1;
            {var subQ0=sQuery(id+"F0.wireOp",EDGE,"E215");Q1=makeQuery(id+"F0.imprint","IMPRINT",FACE,{"disambiguationData":[TD([[makeQuery(id+"F0.imprint","IMPRINT",EDGE,{"derivedFrom":subQ0}),1.0]])]});}
            var Q2;
            Q2=makeQuery(id+"F0.imprint","IMPRINT",FACE,{"disambiguationData":[TD([[makeQuery(id+"F0.imprint","IMPRINT",EDGE,{"derivedFrom":sQuery(id+"F0.wireOp",EDGE,"E87.0")}),-1.0]])]});
            var Q3;
            Q3=makeQuery(id+"F0.imprint","IMPRINT",FACE,{"disambiguationData":[TD([[makeQuery(id+"F0.imprint","IMPRINT",EDGE,{"derivedFrom":sQuery(id+"F0.wireOp",EDGE,"E217")}),1.0]])]});
            var Q4;
            Q4=makeQuery(id+"F0.imprint","IMPRINT",FACE,{"disambiguationData":[TD([[makeQuery(id+"F0.imprint","IMPRINT",EDGE,{"derivedFrom":sQuery(id+"F0.wireOp",EDGE,"E218")}),1.0]])]});
            var Q5;
            Q5=makeQuery(id+"F0.imprint","IMPRINT",FACE,{"disambiguationData":[TD([[makeQuery(id+"F0.imprint","IMPRINT",EDGE,{"derivedFrom":sQuery(id+"F0.wireOp",EDGE,"E224")}),1.0]])]});
            var Q6;
            Q6=makeQuery(id+"F0.imprint","IMPRINT",FACE,{"disambiguationData":[TD([[makeQuery(id+"F0.imprint","IMPRINT",EDGE,{"derivedFrom":sQuery(id+"F0.wireOp",EDGE,"E223")}),1.0]])]});
            var Q7;
            {var subQ3=sQuery(id+"F0.wireOp",EDGE,"E221");Q7=makeQuery(id+"F0.imprint","IMPRINT",FACE,{"disambiguationData":[TD([[makeQuery(id+"F0.imprint","IMPRINT",EDGE,{"derivedFrom":subQ3}),-1.0]])]});}
            var Q8;
            Q8=makeQuery(id+"F0.imprint","IMPRINT",FACE,{"disambiguationData":[TD([[makeQuery(id+"F0.imprint","IMPRINT",EDGE,{"derivedFrom":sQuery(id+"F0.wireOp",EDGE,"E229")}),1.0]])]});
            var Q9;
            Q9=makeQuery(id+"F0.imprint","IMPRINT",FACE,{"disambiguationData":[TD([[makeQuery(id+"F0.imprint","IMPRINT",EDGE,{"derivedFrom":sQuery(id+"F0.wireOp",EDGE,"E228")}),1.0]])]});
            var Q10;
            {var subQ1=sQuery(id+"F0.wireOp",EDGE,"E88.0");Q10=makeQuery(id+"F0.imprint","IMPRINT",FACE,{"disambiguationData":[TD([[makeQuery(id+"F0.imprint","IMPRINT",EDGE,{"derivedFrom":subQ1}),1.0]])]});}
            var Q11;
            {var subQ1=sQuery(id+"F0.wireOp",EDGE,"E88.0");Q11=makeQuery(id+"F0.imprint","IMPRINT",FACE,{"disambiguationData":[TD([[makeQuery(id+"F0.imprint","IMPRINT",EDGE,{"derivedFrom":subQ1}),-1.0]])]});}
            var Q12;
            {var subQ1=sQuery(id+"F0.wireOp",EDGE,"E95");Q12=makeQuery(id+"F0.imprint","IMPRINT",FACE,{"disambiguationData":[TD([[makeQuery(id+"F0.imprint","IMPRINT",EDGE,{"derivedFrom":subQ1}),1.0]])]});}
            extrude(context, id + "F27", {"entities" : qUnion([Q0, Q1, Q2, Q3, Q4, Q5, Q6, Q7, Q8, Q9, Q10, Q11, Q12]), "oppositeDirection" : true, "depth" : 220 * mm, "hasSecondDirection" : true, "secondDirectionOppositeDirection" : true, "secondDirectionDepth" : 217 * mm});
        }
        {
            var Q0;
            {var subQ0=sQuery(id+"F0.wireOp",EDGE,"E215");Q0=makeQuery(id+"F0.imprint","IMPRINT",FACE,{"disambiguationData":[TD([[makeQuery(id+"F0.imprint","IMPRINT",EDGE,{"derivedFrom":subQ0}),1.0]])]});}
            var Q1;
            {var subQ3=sQuery(id+"F0.wireOp",EDGE,"E221");Q1=makeQuery(id+"F0.imprint","IMPRINT",FACE,{"disambiguationData":[TD([[makeQuery(id+"F0.imprint","IMPRINT",EDGE,{"derivedFrom":subQ3}),-1.0]])]});}
            var Q2;
            Q2=makeQuery(id+"F0.imprint","IMPRINT",FACE,{"disambiguationData":[TD([[makeQuery(id+"F0.imprint","IMPRINT",EDGE,{"derivedFrom":sQuery(id+"F0.wireOp",EDGE,"E87.0")}),-1.0]])]});
            var Q3;
            Q3=makeQuery(id+"F0.imprint","IMPRINT",FACE,{"disambiguationData":[TD([[makeQuery(id+"F0.imprint","IMPRINT",EDGE,{"derivedFrom":sQuery(id+"F0.wireOp",EDGE,"E217")}),1.0]])]});
            var Q4;
            Q4=makeQuery(id+"F0.imprint","IMPRINT",FACE,{"disambiguationData":[TD([[makeQuery(id+"F0.imprint","IMPRINT",EDGE,{"derivedFrom":sQuery(id+"F0.wireOp",EDGE,"E218")}),1.0]])]});
            var Q5;
            {var subQ1=sQuery(id+"F0.wireOp",EDGE,"E88.0");Q5=makeQuery(id+"F0.imprint","IMPRINT",FACE,{"disambiguationData":[TD([[makeQuery(id+"F0.imprint","IMPRINT",EDGE,{"derivedFrom":subQ1}),1.0]])]});}
            var Q6;
            Q6=makeQuery(id+"F0.imprint","IMPRINT",FACE,{"disambiguationData":[TD([[makeQuery(id+"F0.imprint","IMPRINT",EDGE,{"derivedFrom":sQuery(id+"F0.wireOp",EDGE,"E228")}),1.0]])]});
            var Q7;
            Q7=makeQuery(id+"F0.imprint","IMPRINT",FACE,{"disambiguationData":[TD([[makeQuery(id+"F0.imprint","IMPRINT",EDGE,{"derivedFrom":sQuery(id+"F0.wireOp",EDGE,"E229")}),1.0]])]});
            var Q8;
            {var subQ1=sQuery(id+"F0.wireOp",EDGE,"E88.0");Q8=makeQuery(id+"F0.imprint","IMPRINT",FACE,{"disambiguationData":[TD([[makeQuery(id+"F0.imprint","IMPRINT",EDGE,{"derivedFrom":subQ1}),-1.0]])]});}
            var Q9;
            Q9=makeQuery(id+"F0.imprint","IMPRINT",FACE,{"disambiguationData":[TD([[makeQuery(id+"F0.imprint","IMPRINT",EDGE,{"derivedFrom":sQuery(id+"F0.wireOp",EDGE,"E223")}),1.0]])]});
            var Q10;
            Q10=makeQuery(id+"F0.imprint","IMPRINT",FACE,{"disambiguationData":[TD([[makeQuery(id+"F0.imprint","IMPRINT",EDGE,{"derivedFrom":sQuery(id+"F0.wireOp",EDGE,"E224")}),1.0]])]});
            var Q11;
            {var subQ1=sQuery(id+"F0.wireOp",EDGE,"E95");Q11=makeQuery(id+"F0.imprint","IMPRINT",FACE,{"disambiguationData":[TD([[makeQuery(id+"F0.imprint","IMPRINT",EDGE,{"derivedFrom":subQ1}),1.0]])]});}
            extrude(context, id + "F28", {"entities" : qUnion([Q0, Q1, Q2, Q3, Q4, Q5, Q6, Q7, Q8, Q9, Q10, Q11]), "operationType" : NewBodyOperationType.ADD, "oppositeDirection" : true, "depth" : 220 * mm, "hasSecondDirection" : true, "secondDirectionOppositeDirection" : true, "secondDirectionDepth" : 151.77 * mm});
        }
        {
            var Q0;
            Q0=makeQuery(id+"F0.imprint","IMPRINT",FACE,{"disambiguationData":[TD([[makeQuery(id+"F0.imprint","IMPRINT",EDGE,{"derivedFrom":sQuery(id+"F0.wireOp",EDGE,"E229")}),1.0]])]});
            var Q1;
            Q1=makeQuery(id+"F0.imprint","IMPRINT",FACE,{"disambiguationData":[TD([[makeQuery(id+"F0.imprint","IMPRINT",EDGE,{"derivedFrom":sQuery(id+"F0.wireOp",EDGE,"E224")}),1.0]])]});
            var Q2;
            Q2=makeQuery(id+"F0.imprint","IMPRINT",FACE,{"disambiguationData":[TD([[makeQuery(id+"F0.imprint","IMPRINT",EDGE,{"derivedFrom":sQuery(id+"F0.wireOp",EDGE,"E218")}),1.0]])]});
            extrude(context, id + "F29", {"entities" : qUnion([Q0, Q1, Q2]), "operationType" : NewBodyOperationType.ADD, "oppositeDirection" : true, "depth" : 151.77 * mm, "hasSecondDirection" : true, "secondDirectionOppositeDirection" : true, "secondDirectionDepth" : 147.77 * mm});
        }
        {
            var Q0;
            {var subQ1=sQuery(id+"F0.wireOp",EDGE,"E207");Q0=makeQuery(id+"F0.imprint","IMPRINT",FACE,{"disambiguationData":[TD([[makeQuery(id+"F0.imprint","IMPRINT",EDGE,{"derivedFrom":subQ1}),-1.0]])]});}
            var Q1;
            {var subQ0=sQuery(id+"F0.wireOp",EDGE,"E207");Q1=makeQuery(id+"F0.imprint","IMPRINT",FACE,{"disambiguationData":[TD([[makeQuery(id+"F0.imprint","IMPRINT",EDGE,{"derivedFrom":subQ0}),1.0]])]});}
            var Q2;
            Q2=makeQuery(id+"F0.imprint","IMPRINT",FACE,{"disambiguationData":[TD([[makeQuery(id+"F0.imprint","IMPRINT",EDGE,{"derivedFrom":sQuery(id+"F0.wireOp",EDGE,"E209")}),1.0]])]});
            var Q3;
            Q3=makeQuery(id+"F0.imprint","IMPRINT",FACE,{"disambiguationData":[TD([[makeQuery(id+"F0.imprint","IMPRINT",EDGE,{"derivedFrom":sQuery(id+"F0.wireOp",EDGE,"E220")}),1.0]])]});
            var Q4;
            {var subQ1=sQuery(id+"F0.wireOp",EDGE,"E154");Q4=makeQuery(id+"F0.imprint","IMPRINT",FACE,{"disambiguationData":[TD([[makeQuery(id+"F0.imprint","IMPRINT",EDGE,{"derivedFrom":subQ1}),-1.0]])]});}
            var Q5;
            {var subQ5=sQuery(id+"F0.wireOp",EDGE,"E40.0");Q5=makeQuery(id+"F0.imprint","IMPRINT",FACE,{"disambiguationData":[TD([[makeQuery(id+"F0.imprint","IMPRINT",EDGE,{"derivedFrom":subQ5}),-1.0]])]});}
            var Q6;
            {var subQ0=sQuery(id+"F0.wireOp",EDGE,"E257.filletArc");Q6=makeQuery(id+"F0.imprint","IMPRINT",FACE,{"disambiguationData":[TD([[makeQuery(id+"F0.imprint","IMPRINT",EDGE,{"derivedFrom":subQ0}),-1.0]])]});}
            var Q7;
            {var subQ1=sQuery(id+"F0.wireOp",EDGE,"E250");Q7=makeQuery(id+"F0.imprint","IMPRINT",FACE,{"disambiguationData":[TD([[makeQuery(id+"F0.imprint","IMPRINT",EDGE,{"derivedFrom":subQ1}),-1.0]])]});}
            var Q8;
            Q8=makeQuery(id+"F0.imprint","IMPRINT",FACE,{"disambiguationData":[TD([[makeQuery(id+"F0.imprint","IMPRINT",EDGE,{"derivedFrom":sQuery(id+"F0.wireOp",EDGE,"E86.0")}),1.0]])]});
            var Q9;
            Q9=makeQuery(id+"F0.imprint","IMPRINT",FACE,{"disambiguationData":[TD([[makeQuery(id+"F0.imprint","IMPRINT",EDGE,{"derivedFrom":sQuery(id+"F0.wireOp",EDGE,"E219")}),1.0]])]});
            var Q10;
            Q10=makeQuery(id+"F0.imprint","IMPRINT",FACE,{"disambiguationData":[TD([[makeQuery(id+"F0.imprint","IMPRINT",EDGE,{"derivedFrom":sQuery(id+"F0.wireOp",EDGE,"E216")}),1.0]])]});
            var Q11;
            Q11=makeQuery(id+"F0.imprint","IMPRINT",FACE,{"disambiguationData":[TD([[makeQuery(id+"F0.imprint","IMPRINT",EDGE,{"derivedFrom":sQuery(id+"F0.wireOp",EDGE,"E86.0")}),-1.0]])]});
            var Q12;
            {var subQ0=sQuery(id+"F0.wireOp",EDGE,"E249.filletArc");Q12=makeQuery(id+"F0.imprint","IMPRINT",FACE,{"disambiguationData":[TD([[makeQuery(id+"F0.imprint","IMPRINT",EDGE,{"derivedFrom":subQ0}),-1.0]])]});}
            var Q13;
            {var subQ0=sQuery(id+"F0.wireOp",EDGE,"E247.filletArc");Q13=makeQuery(id+"F0.imprint","IMPRINT",FACE,{"disambiguationData":[TD([[makeQuery(id+"F0.imprint","IMPRINT",EDGE,{"derivedFrom":subQ0}),-1.0]])]});}
            var Q14;
            {var subQ0=sQuery(id+"F0.wireOp",EDGE,"E256.filletArc");Q14=makeQuery(id+"F0.imprint","IMPRINT",FACE,{"disambiguationData":[TD([[makeQuery(id+"F0.imprint","IMPRINT",EDGE,{"derivedFrom":subQ0}),-1.0]])]});}
            extrude(context, id + "F30", {"entities" : qUnion([Q0, Q1, Q2, Q3, Q4, Q5, Q6, Q7, Q8, Q9, Q10, Q11, Q12, Q13, Q14]), "oppositeDirection" : true, "depth" : 220 * mm, "hasSecondDirection" : true, "secondDirectionOppositeDirection" : true, "secondDirectionDepth" : 217 * mm});
        }
        {
            var Q0;
            Q0=makeQuery(id+"F0.imprint","IMPRINT",FACE,{"disambiguationData":[TD([[makeQuery(id+"F0.imprint","IMPRINT",EDGE,{"derivedFrom":sQuery(id+"F0.wireOp",EDGE,"E220")}),1.0]])]});
            var Q1;
            Q1=makeQuery(id+"F0.imprint","IMPRINT",FACE,{"disambiguationData":[TD([[makeQuery(id+"F0.imprint","IMPRINT",EDGE,{"derivedFrom":sQuery(id+"F0.wireOp",EDGE,"E209")}),1.0]])]});
            var Q2;
            {var subQ0=sQuery(id+"F0.wireOp",EDGE,"E207");Q2=makeQuery(id+"F0.imprint","IMPRINT",FACE,{"disambiguationData":[TD([[makeQuery(id+"F0.imprint","IMPRINT",EDGE,{"derivedFrom":subQ0}),1.0]])]});}
            var Q3;
            {var subQ0=sQuery(id+"F0.wireOp",EDGE,"E256.filletArc");Q3=makeQuery(id+"F0.imprint","IMPRINT",FACE,{"disambiguationData":[TD([[makeQuery(id+"F0.imprint","IMPRINT",EDGE,{"derivedFrom":subQ0}),-1.0]])]});}
            var Q4;
            {var subQ1=sQuery(id+"F0.wireOp",EDGE,"E207");Q4=makeQuery(id+"F0.imprint","IMPRINT",FACE,{"disambiguationData":[TD([[makeQuery(id+"F0.imprint","IMPRINT",EDGE,{"derivedFrom":subQ1}),-1.0]])]});}
            var Q5;
            {var subQ1=sQuery(id+"F0.wireOp",EDGE,"E154");Q5=makeQuery(id+"F0.imprint","IMPRINT",FACE,{"disambiguationData":[TD([[makeQuery(id+"F0.imprint","IMPRINT",EDGE,{"derivedFrom":subQ1}),-1.0]])]});}
            var Q6;
            {var subQ5=sQuery(id+"F0.wireOp",EDGE,"E40.0");Q6=makeQuery(id+"F0.imprint","IMPRINT",FACE,{"disambiguationData":[TD([[makeQuery(id+"F0.imprint","IMPRINT",EDGE,{"derivedFrom":subQ5}),-1.0]])]});}
            var Q7;
            {var subQ1=sQuery(id+"F0.wireOp",EDGE,"E250");Q7=makeQuery(id+"F0.imprint","IMPRINT",FACE,{"disambiguationData":[TD([[makeQuery(id+"F0.imprint","IMPRINT",EDGE,{"derivedFrom":subQ1}),-1.0]])]});}
            var Q8;
            {var subQ0=sQuery(id+"F0.wireOp",EDGE,"E257.filletArc");Q8=makeQuery(id+"F0.imprint","IMPRINT",FACE,{"disambiguationData":[TD([[makeQuery(id+"F0.imprint","IMPRINT",EDGE,{"derivedFrom":subQ0}),-1.0]])]});}
            var Q9;
            Q9=makeQuery(id+"F0.imprint","IMPRINT",FACE,{"disambiguationData":[TD([[makeQuery(id+"F0.imprint","IMPRINT",EDGE,{"derivedFrom":sQuery(id+"F0.wireOp",EDGE,"E86.0")}),-1.0]])]});
            var Q10;
            Q10=makeQuery(id+"F0.imprint","IMPRINT",FACE,{"disambiguationData":[TD([[makeQuery(id+"F0.imprint","IMPRINT",EDGE,{"derivedFrom":sQuery(id+"F0.wireOp",EDGE,"E216")}),1.0]])]});
            var Q11;
            Q11=makeQuery(id+"F0.imprint","IMPRINT",FACE,{"disambiguationData":[TD([[makeQuery(id+"F0.imprint","IMPRINT",EDGE,{"derivedFrom":sQuery(id+"F0.wireOp",EDGE,"E219")}),1.0]])]});
            extrude(context, id + "F31", {"entities" : qUnion([Q0, Q1, Q2, Q3, Q4, Q5, Q6, Q7, Q8, Q9, Q10, Q11]), "operationType" : NewBodyOperationType.ADD, "oppositeDirection" : true, "depth" : 220 * mm, "hasSecondDirection" : true, "secondDirectionOppositeDirection" : true, "secondDirectionDepth" : 151.77 * mm});
        }
        {
            var Q0;
            Q0=makeQuery(id+"F0.imprint","IMPRINT",FACE,{"disambiguationData":[TD([[makeQuery(id+"F0.imprint","IMPRINT",EDGE,{"derivedFrom":sQuery(id+"F0.wireOp",EDGE,"E219")}),1.0]])]});
            var Q1;
            Q1=makeQuery(id+"F0.imprint","IMPRINT",FACE,{"disambiguationData":[TD([[makeQuery(id+"F0.imprint","IMPRINT",EDGE,{"derivedFrom":sQuery(id+"F0.wireOp",EDGE,"E220")}),1.0]])]});
            extrude(context, id + "F32", {"entities" : qUnion([Q0, Q1]), "operationType" : NewBodyOperationType.ADD, "oppositeDirection" : true, "depth" : 151.77 * mm, "hasSecondDirection" : true, "secondDirectionOppositeDirection" : true, "secondDirectionDepth" : 147.77 * mm});
        }
        {
            var Q0;
            Q0=makeQuery(id+"F0.imprint","IMPRINT",FACE,{"disambiguationData":[TD([[makeQuery(id+"F0.imprint","IMPRINT",EDGE,{"derivedFrom":sQuery(id+"F0.wireOp",EDGE,"E229")}),1.0]])]});
            var Q1;
            Q1=makeQuery(id+"F0.imprint","IMPRINT",FACE,{"disambiguationData":[TD([[makeQuery(id+"F0.imprint","IMPRINT",EDGE,{"derivedFrom":sQuery(id+"F0.wireOp",EDGE,"E228")}),1.0]])]});
            var Q2;
            Q2=makeQuery(id+"F0.imprint","IMPRINT",FACE,{"disambiguationData":[TD([[makeQuery(id+"F0.imprint","IMPRINT",EDGE,{"derivedFrom":sQuery(id+"F0.wireOp",EDGE,"E224")}),1.0]])]});
            var Q3;
            Q3=makeQuery(id+"F0.imprint","IMPRINT",FACE,{"disambiguationData":[TD([[makeQuery(id+"F0.imprint","IMPRINT",EDGE,{"derivedFrom":sQuery(id+"F0.wireOp",EDGE,"E223")}),1.0]])]});
            var Q4;
            Q4=makeQuery(id+"F0.imprint","IMPRINT",FACE,{"disambiguationData":[TD([[makeQuery(id+"F0.imprint","IMPRINT",EDGE,{"derivedFrom":sQuery(id+"F0.wireOp",EDGE,"E218")}),1.0]])]});
            var Q5;
            Q5=makeQuery(id+"F0.imprint","IMPRINT",FACE,{"disambiguationData":[TD([[makeQuery(id+"F0.imprint","IMPRINT",EDGE,{"derivedFrom":sQuery(id+"F0.wireOp",EDGE,"E217")}),1.0]])]});
            var Q6;
            Q6=makeQuery(id+"F0.imprint","IMPRINT",FACE,{"disambiguationData":[TD([[makeQuery(id+"F0.imprint","IMPRINT",EDGE,{"derivedFrom":sQuery(id+"F0.wireOp",EDGE,"E219")}),1.0]])]});
            var Q7;
            Q7=makeQuery(id+"F0.imprint","IMPRINT",FACE,{"disambiguationData":[TD([[makeQuery(id+"F0.imprint","IMPRINT",EDGE,{"derivedFrom":sQuery(id+"F0.wireOp",EDGE,"E216")}),1.0]])]});
            var Q8;
            Q8=makeQuery(id+"F0.imprint","IMPRINT",FACE,{"disambiguationData":[TD([[makeQuery(id+"F0.imprint","IMPRINT",EDGE,{"derivedFrom":sQuery(id+"F0.wireOp",EDGE,"E220")}),1.0]])]});
            var Q9;
            Q9=makeQuery(id+"F0.imprint","IMPRINT",FACE,{"disambiguationData":[TD([[makeQuery(id+"F0.imprint","IMPRINT",EDGE,{"derivedFrom":sQuery(id+"F0.wireOp",EDGE,"E209")}),1.0]])]});
            extrude(context, id + "F33", {"entities" : qUnion([Q0, Q1, Q2, Q3, Q4, Q5, Q6, Q7, Q8, Q9]), "operationType" : NewBodyOperationType.REMOVE, "oppositeDirection" : true, "depth" : 220 * mm, "hasSecondDirection" : true, "secondDirectionOppositeDirection" : true, "secondDirectionDepth" : 215 * mm});
        }
        {
            var Q0;
            Q0=makeQuery(id+"F27.opExtrude","SWEPT_BODY",BODY,{"disambiguationData":[OSD([sQuery(id+"F0.wireOp",EDGE,"E0"),sQuery(id+"F0.wireOp",EDGE,"E3"),sQuery(id+"F0.wireOp",EDGE,"E29"),sQuery(id+"F0.wireOp",EDGE,"E91"),sQuery(id+"F0.wireOp",EDGE,"E95"),sQuery(id+"F0.wireOp",EDGE,"E97"),sQuery(id+"F0.wireOp",EDGE,"E98"),sQuery(id+"F0.wireOp",EDGE,"E99"),sQuery(id+"F0.wireOp",EDGE,"E100"),sQuery(id+"F0.wireOp",EDGE,"E101"),sQuery(id+"F0.wireOp",EDGE,"E102"),sQuery(id+"F0.wireOp",EDGE,"E103"),sQuery(id+"F0.wireOp",EDGE,"E104"),sQuery(id+"F0.wireOp",EDGE,"E105"),sQuery(id+"F0.wireOp",EDGE,"E106"),sQuery(id+"F0.wireOp",EDGE,"E107"),sQuery(id+"F0.wireOp",EDGE,"E108"),sQuery(id+"F0.wireOp",EDGE,"E109"),sQuery(id+"F0.wireOp",EDGE,"E110"),sQuery(id+"F0.wireOp",EDGE,"E111"),sQuery(id+"F0.wireOp",EDGE,"E112"),sQuery(id+"F0.wireOp",EDGE,"E113"),sQuery(id+"F0.wireOp",EDGE,"E185.0"),sQuery(id+"F0.wireOp",EDGE,"E185.1"),sQuery(id+"F0.wireOp",EDGE,"E185.2"),sQuery(id+"F0.wireOp",EDGE,"E185.3"),sQuery(id+"F0.wireOp",EDGE,"E185.4"),sQuery(id+"F0.wireOp",EDGE,"E185.5"),sQuery(id+"F0.wireOp",EDGE,"E188.trimOffspring"),sQuery(id+"F0.wireOp",EDGE,"E201.0"),sQuery(id+"F0.wireOp",EDGE,"E201.1"),sQuery(id+"F0.wireOp",EDGE,"E201.2"),sQuery(id+"F0.wireOp",EDGE,"E201.3"),sQuery(id+"F0.wireOp",EDGE,"E201.4"),sQuery(id+"F0.wireOp",EDGE,"E201.5"),sQuery(id+"F0.wireOp",EDGE,"E204.trimOffspring"),sQuery(id+"F0.wireOp",EDGE,"E244.filletArc")])]});
            transform(context, id + "F34", {"entities" : qUnion([Q0]), "transformType" : TransformType.TRANSLATION_3D, "dx" : 0 * mm, "dy" : 0 * mm, "dz" : 68.33 * mm, "makeCopy" : true});
        }
        {
            var Q0;
            Q0=makeQuery(id+"F30.opExtrude","SWEPT_BODY",BODY,{"disambiguationData":[OSD([sQuery(id+"F0.wireOp",EDGE,"E2"),sQuery(id+"F0.wireOp",EDGE,"E28"),sQuery(id+"F0.wireOp",EDGE,"E40.0"),sQuery(id+"F0.wireOp",EDGE,"E40.1"),sQuery(id+"F0.wireOp",EDGE,"E40.2"),sQuery(id+"F0.wireOp",EDGE,"E40.3"),sQuery(id+"F0.wireOp",EDGE,"E40.4"),sQuery(id+"F0.wireOp",EDGE,"E40.5"),sQuery(id+"F0.wireOp",EDGE,"E43.trimOffspring"),sQuery(id+"F0.wireOp",EDGE,"E54.0"),sQuery(id+"F0.wireOp",EDGE,"E54.1"),sQuery(id+"F0.wireOp",EDGE,"E54.2"),sQuery(id+"F0.wireOp",EDGE,"E54.3"),sQuery(id+"F0.wireOp",EDGE,"E54.4"),sQuery(id+"F0.wireOp",EDGE,"E54.5"),sQuery(id+"F0.wireOp",EDGE,"E57.trimOffspring"),sQuery(id+"F0.wireOp",EDGE,"E92"),sQuery(id+"F0.wireOp",EDGE,"E93"),sQuery(id+"F0.wireOp",EDGE,"E94"),sQuery(id+"F0.wireOp",EDGE,"E114.0"),sQuery(id+"F0.wireOp",EDGE,"E114.1"),sQuery(id+"F0.wireOp",EDGE,"E114.2"),sQuery(id+"F0.wireOp",EDGE,"E114.3"),sQuery(id+"F0.wireOp",EDGE,"E114.4"),sQuery(id+"F0.wireOp",EDGE,"E114.5"),sQuery(id+"F0.wireOp",EDGE,"E114.6"),sQuery(id+"F0.wireOp",EDGE,"E114.7"),sQuery(id+"F0.wireOp",EDGE,"E114.8"),sQuery(id+"F0.wireOp",EDGE,"E114.9"),sQuery(id+"F0.wireOp",EDGE,"E114.10"),sQuery(id+"F0.wireOp",EDGE,"E114.11"),sQuery(id+"F0.wireOp",EDGE,"E114.12"),sQuery(id+"F0.wireOp",EDGE,"E114.13"),sQuery(id+"F0.wireOp",EDGE,"E114.14"),sQuery(id+"F0.wireOp",EDGE,"E114.15"),sQuery(id+"F0.wireOp",EDGE,"E114.16"),sQuery(id+"F0.wireOp",EDGE,"E115"),sQuery(id+"F0.wireOp",EDGE,"E154"),sQuery(id+"F0.wireOp",EDGE,"E174.0"),sQuery(id+"F0.wireOp",EDGE,"E246.filletArc"),sQuery(id+"F0.wireOp",EDGE,"E248"),sQuery(id+"F0.wireOp",EDGE,"E250"),sQuery(id+"F0.wireOp",EDGE,"E285"),sQuery(id+"F0.wireOp",EDGE,"E291"),sQuery(id+"F0.wireOp",EDGE,"E297"),sQuery(id+"F0.wireOp",EDGE,"E298")])]});
            transform(context, id + "F35", {"entities" : qUnion([Q0]), "transformType" : TransformType.TRANSLATION_3D, "dx" : 0 * mm, "dy" : 0 * mm, "dz" : 68.33 * mm, "makeCopy" : true});
        }
        {
            var Q0;
            Q0=makeQuery(id+"F34.opPattern","COPY",BODY,{"derivedFrom":makeQuery(id+"F27.opExtrude","SWEPT_BODY",BODY,{"disambiguationData":[OSD([sQuery(id+"F0.wireOp",EDGE,"E0"),sQuery(id+"F0.wireOp",EDGE,"E3"),sQuery(id+"F0.wireOp",EDGE,"E29"),sQuery(id+"F0.wireOp",EDGE,"E91"),sQuery(id+"F0.wireOp",EDGE,"E95"),sQuery(id+"F0.wireOp",EDGE,"E97"),sQuery(id+"F0.wireOp",EDGE,"E98"),sQuery(id+"F0.wireOp",EDGE,"E99"),sQuery(id+"F0.wireOp",EDGE,"E100"),sQuery(id+"F0.wireOp",EDGE,"E101"),sQuery(id+"F0.wireOp",EDGE,"E102"),sQuery(id+"F0.wireOp",EDGE,"E103"),sQuery(id+"F0.wireOp",EDGE,"E104"),sQuery(id+"F0.wireOp",EDGE,"E105"),sQuery(id+"F0.wireOp",EDGE,"E106"),sQuery(id+"F0.wireOp",EDGE,"E107"),sQuery(id+"F0.wireOp",EDGE,"E108"),sQuery(id+"F0.wireOp",EDGE,"E109"),sQuery(id+"F0.wireOp",EDGE,"E110"),sQuery(id+"F0.wireOp",EDGE,"E111"),sQuery(id+"F0.wireOp",EDGE,"E112"),sQuery(id+"F0.wireOp",EDGE,"E113"),sQuery(id+"F0.wireOp",EDGE,"E185.0"),sQuery(id+"F0.wireOp",EDGE,"E185.1"),sQuery(id+"F0.wireOp",EDGE,"E185.2"),sQuery(id+"F0.wireOp",EDGE,"E185.3"),sQuery(id+"F0.wireOp",EDGE,"E185.4"),sQuery(id+"F0.wireOp",EDGE,"E185.5"),sQuery(id+"F0.wireOp",EDGE,"E188.trimOffspring"),sQuery(id+"F0.wireOp",EDGE,"E201.0"),sQuery(id+"F0.wireOp",EDGE,"E201.1"),sQuery(id+"F0.wireOp",EDGE,"E201.2"),sQuery(id+"F0.wireOp",EDGE,"E201.3"),sQuery(id+"F0.wireOp",EDGE,"E201.4"),sQuery(id+"F0.wireOp",EDGE,"E201.5"),sQuery(id+"F0.wireOp",EDGE,"E204.trimOffspring"),sQuery(id+"F0.wireOp",EDGE,"E244.filletArc")])]}),"instanceName":"1"});
            transform(context, id + "F36", {"entities" : qUnion([Q0]), "transformType" : TransformType.TRANSLATION_3D, "dx" : 0 * mm, "dy" : 0 * mm, "dz" : 68.33 * mm, "makeCopy" : true});
        }
        {
            var Q0;
            Q0=makeQuery(id+"F35.opPattern","COPY",BODY,{"derivedFrom":makeQuery(id+"F30.opExtrude","SWEPT_BODY",BODY,{"disambiguationData":[OSD([sQuery(id+"F0.wireOp",EDGE,"E2"),sQuery(id+"F0.wireOp",EDGE,"E28"),sQuery(id+"F0.wireOp",EDGE,"E40.0"),sQuery(id+"F0.wireOp",EDGE,"E40.1"),sQuery(id+"F0.wireOp",EDGE,"E40.2"),sQuery(id+"F0.wireOp",EDGE,"E40.3"),sQuery(id+"F0.wireOp",EDGE,"E40.4"),sQuery(id+"F0.wireOp",EDGE,"E40.5"),sQuery(id+"F0.wireOp",EDGE,"E43.trimOffspring"),sQuery(id+"F0.wireOp",EDGE,"E54.0"),sQuery(id+"F0.wireOp",EDGE,"E54.1"),sQuery(id+"F0.wireOp",EDGE,"E54.2"),sQuery(id+"F0.wireOp",EDGE,"E54.3"),sQuery(id+"F0.wireOp",EDGE,"E54.4"),sQuery(id+"F0.wireOp",EDGE,"E54.5"),sQuery(id+"F0.wireOp",EDGE,"E57.trimOffspring"),sQuery(id+"F0.wireOp",EDGE,"E92"),sQuery(id+"F0.wireOp",EDGE,"E93"),sQuery(id+"F0.wireOp",EDGE,"E94"),sQuery(id+"F0.wireOp",EDGE,"E114.0"),sQuery(id+"F0.wireOp",EDGE,"E114.1"),sQuery(id+"F0.wireOp",EDGE,"E114.2"),sQuery(id+"F0.wireOp",EDGE,"E114.3"),sQuery(id+"F0.wireOp",EDGE,"E114.4"),sQuery(id+"F0.wireOp",EDGE,"E114.5"),sQuery(id+"F0.wireOp",EDGE,"E114.6"),sQuery(id+"F0.wireOp",EDGE,"E114.7"),sQuery(id+"F0.wireOp",EDGE,"E114.8"),sQuery(id+"F0.wireOp",EDGE,"E114.9"),sQuery(id+"F0.wireOp",EDGE,"E114.10"),sQuery(id+"F0.wireOp",EDGE,"E114.11"),sQuery(id+"F0.wireOp",EDGE,"E114.12"),sQuery(id+"F0.wireOp",EDGE,"E114.13"),sQuery(id+"F0.wireOp",EDGE,"E114.14"),sQuery(id+"F0.wireOp",EDGE,"E114.15"),sQuery(id+"F0.wireOp",EDGE,"E114.16"),sQuery(id+"F0.wireOp",EDGE,"E115"),sQuery(id+"F0.wireOp",EDGE,"E154"),sQuery(id+"F0.wireOp",EDGE,"E174.0"),sQuery(id+"F0.wireOp",EDGE,"E246.filletArc"),sQuery(id+"F0.wireOp",EDGE,"E248"),sQuery(id+"F0.wireOp",EDGE,"E250"),sQuery(id+"F0.wireOp",EDGE,"E285"),sQuery(id+"F0.wireOp",EDGE,"E291"),sQuery(id+"F0.wireOp",EDGE,"E297"),sQuery(id+"F0.wireOp",EDGE,"E298")])]}),"instanceName":"1"});
            transform(context, id + "F37", {"entities" : qUnion([Q0]), "transformType" : TransformType.TRANSLATION_3D, "dx" : 0 * mm, "dy" : 0 * mm, "dz" : 68.33 * mm, "makeCopy" : true});
        }
        {
            var Q0;
            Q0=makeQuery(id+"F10.opExtrude","CAP_EDGE",EDGE,{"disambiguationData":[OSD([sQuery(id+"F0.wireOp",EDGE,"E19")])],"isStart":true});
            var Q1;
            Q1=makeQuery(id+"F15.opExtrude","CAP_EDGE",EDGE,{"disambiguationData":[OSD([sQuery(id+"F0.wireOp",EDGE,"E131"),sQuery(id+"F0.wireOp",EDGE,"E292")])],"isStart":true});
            var Q2;
            Q2=makeQuery(id+"F20.opExtrude","CAP_EDGE",EDGE,{"disambiguationData":[OSD([sQuery(id+"F0.wireOp",EDGE,"E131"),sQuery(id+"F0.wireOp",EDGE,"E292")])],"isStart":true});
            var Q3;
            Q3=makeQuery(id+"F24.opExtrude","CAP_EDGE",EDGE,{"disambiguationData":[OSD([sQuery(id+"F0.wireOp",EDGE,"E173.trimOffspring"),sQuery(id+"F0.wireOp",EDGE,"E294")])],"isStart":true});
            var Q4;
            Q4=makeQuery(id+"F25.opPattern","COPY",EDGE,{"derivedFrom":makeQuery(id+"F24.opExtrude","CAP_EDGE",EDGE,{"disambiguationData":[OSD([sQuery(id+"F0.wireOp",EDGE,"E173.trimOffspring"),sQuery(id+"F0.wireOp",EDGE,"E294")])],"isStart":true}),"instanceName":"1"});
            var Q5;
            Q5=makeQuery(id+"F26.opPattern","COPY",EDGE,{"derivedFrom":makeQuery(id+"F25.opPattern","COPY",EDGE,{"derivedFrom":makeQuery(id+"F24.opExtrude","CAP_EDGE",EDGE,{"disambiguationData":[OSD([sQuery(id+"F0.wireOp",EDGE,"E173.trimOffspring"),sQuery(id+"F0.wireOp",EDGE,"E294")])],"isStart":true}),"instanceName":"1"}),"instanceName":"1"});
            var Q6;
            {var subQ0=sQuery(id+"F0.wireOp",EDGE,"E297");var subQ1=sQuery(id+"F0.wireOp",EDGE,"E248");Q6=makeQuery(id+"F31.boolean.opBoolean","INTERSECT",EDGE,{"derivedFrom":[makeQuery(id+"F30.opExtrude","CAP_FACE",FACE,{"disambiguationData":[OSD([sQuery(id+"F0.wireOp",EDGE,"E2"),sQuery(id+"F0.wireOp",EDGE,"E28"),sQuery(id+"F0.wireOp",EDGE,"E40.0"),sQuery(id+"F0.wireOp",EDGE,"E40.1"),sQuery(id+"F0.wireOp",EDGE,"E40.2"),sQuery(id+"F0.wireOp",EDGE,"E40.3"),sQuery(id+"F0.wireOp",EDGE,"E40.4"),sQuery(id+"F0.wireOp",EDGE,"E40.5"),sQuery(id+"F0.wireOp",EDGE,"E43.trimOffspring"),sQuery(id+"F0.wireOp",EDGE,"E54.0"),sQuery(id+"F0.wireOp",EDGE,"E54.1"),sQuery(id+"F0.wireOp",EDGE,"E54.2"),sQuery(id+"F0.wireOp",EDGE,"E54.3"),sQuery(id+"F0.wireOp",EDGE,"E54.4"),sQuery(id+"F0.wireOp",EDGE,"E54.5"),sQuery(id+"F0.wireOp",EDGE,"E57.trimOffspring"),sQuery(id+"F0.wireOp",EDGE,"E92"),sQuery(id+"F0.wireOp",EDGE,"E93"),sQuery(id+"F0.wireOp",EDGE,"E94"),sQuery(id+"F0.wireOp",EDGE,"E114.0"),sQuery(id+"F0.wireOp",EDGE,"E114.1"),sQuery(id+"F0.wireOp",EDGE,"E114.2"),sQuery(id+"F0.wireOp",EDGE,"E114.3"),sQuery(id+"F0.wireOp",EDGE,"E114.4"),sQuery(id+"F0.wireOp",EDGE,"E114.5"),sQuery(id+"F0.wireOp",EDGE,"E114.6"),sQuery(id+"F0.wireOp",EDGE,"E114.7"),sQuery(id+"F0.wireOp",EDGE,"E114.8"),sQuery(id+"F0.wireOp",EDGE,"E114.9"),sQuery(id+"F0.wireOp",EDGE,"E114.10"),sQuery(id+"F0.wireOp",EDGE,"E114.11"),sQuery(id+"F0.wireOp",EDGE,"E114.12"),sQuery(id+"F0.wireOp",EDGE,"E114.13"),sQuery(id+"F0.wireOp",EDGE,"E114.14"),sQuery(id+"F0.wireOp",EDGE,"E114.15"),sQuery(id+"F0.wireOp",EDGE,"E114.16"),sQuery(id+"F0.wireOp",EDGE,"E115"),sQuery(id+"F0.wireOp",EDGE,"E154"),sQuery(id+"F0.wireOp",EDGE,"E174.0"),sQuery(id+"F0.wireOp",EDGE,"E246.filletArc"),subQ1,sQuery(id+"F0.wireOp",EDGE,"E250"),sQuery(id+"F0.wireOp",EDGE,"E285"),sQuery(id+"F0.wireOp",EDGE,"E291"),subQ0,sQuery(id+"F0.wireOp",EDGE,"E298")])],"isStart":true}),makeQuery(id+"F31.opExtrude","SWEPT_FACE",FACE,{"disambiguationData":[OSD([sQuery(id+"F0.wireOp",EDGE,"E86.0"),subQ1,sQuery(id+"F0.wireOp",EDGE,"E267"),subQ0])]})]});}
            var Q7;
            Q7=makeQuery(id+"F28.boolean.opBoolean","INTERSECT",EDGE,{"derivedFrom":[makeQuery(id+"F27.opExtrude","CAP_FACE",FACE,{"disambiguationData":[OSD([sQuery(id+"F0.wireOp",EDGE,"E0"),sQuery(id+"F0.wireOp",EDGE,"E3"),sQuery(id+"F0.wireOp",EDGE,"E29"),sQuery(id+"F0.wireOp",EDGE,"E91"),sQuery(id+"F0.wireOp",EDGE,"E95"),sQuery(id+"F0.wireOp",EDGE,"E97"),sQuery(id+"F0.wireOp",EDGE,"E98"),sQuery(id+"F0.wireOp",EDGE,"E99"),sQuery(id+"F0.wireOp",EDGE,"E100"),sQuery(id+"F0.wireOp",EDGE,"E101"),sQuery(id+"F0.wireOp",EDGE,"E102"),sQuery(id+"F0.wireOp",EDGE,"E103"),sQuery(id+"F0.wireOp",EDGE,"E104"),sQuery(id+"F0.wireOp",EDGE,"E105"),sQuery(id+"F0.wireOp",EDGE,"E106"),sQuery(id+"F0.wireOp",EDGE,"E107"),sQuery(id+"F0.wireOp",EDGE,"E108"),sQuery(id+"F0.wireOp",EDGE,"E109"),sQuery(id+"F0.wireOp",EDGE,"E110"),sQuery(id+"F0.wireOp",EDGE,"E111"),sQuery(id+"F0.wireOp",EDGE,"E112"),sQuery(id+"F0.wireOp",EDGE,"E113"),sQuery(id+"F0.wireOp",EDGE,"E185.0"),sQuery(id+"F0.wireOp",EDGE,"E185.1"),sQuery(id+"F0.wireOp",EDGE,"E185.2"),sQuery(id+"F0.wireOp",EDGE,"E185.3"),sQuery(id+"F0.wireOp",EDGE,"E185.4"),sQuery(id+"F0.wireOp",EDGE,"E185.5"),sQuery(id+"F0.wireOp",EDGE,"E188.trimOffspring"),sQuery(id+"F0.wireOp",EDGE,"E201.0"),sQuery(id+"F0.wireOp",EDGE,"E201.1"),sQuery(id+"F0.wireOp",EDGE,"E201.2"),sQuery(id+"F0.wireOp",EDGE,"E201.3"),sQuery(id+"F0.wireOp",EDGE,"E201.4"),sQuery(id+"F0.wireOp",EDGE,"E201.5"),sQuery(id+"F0.wireOp",EDGE,"E204.trimOffspring"),sQuery(id+"F0.wireOp",EDGE,"E244.filletArc")])],"isStart":true}),makeQuery(id+"F28.opExtrude","SWEPT_FACE",FACE,{"disambiguationData":[OSD([sQuery(id+"F0.wireOp",EDGE,"E87.0"),sQuery(id+"F0.wireOp",EDGE,"E268")])]})]});
            var Q8;
            {var subQ0=sQuery(id+"F0.wireOp",EDGE,"E285");var subQ1=sQuery(id+"F0.wireOp",EDGE,"E250");Q8=makeQuery(id+"F31.boolean.opBoolean","INTERSECT",EDGE,{"derivedFrom":[makeQuery(id+"F30.opExtrude","CAP_FACE",FACE,{"disambiguationData":[OSD([sQuery(id+"F0.wireOp",EDGE,"E2"),sQuery(id+"F0.wireOp",EDGE,"E28"),sQuery(id+"F0.wireOp",EDGE,"E40.0"),sQuery(id+"F0.wireOp",EDGE,"E40.1"),sQuery(id+"F0.wireOp",EDGE,"E40.2"),sQuery(id+"F0.wireOp",EDGE,"E40.3"),sQuery(id+"F0.wireOp",EDGE,"E40.4"),sQuery(id+"F0.wireOp",EDGE,"E40.5"),sQuery(id+"F0.wireOp",EDGE,"E43.trimOffspring"),sQuery(id+"F0.wireOp",EDGE,"E54.0"),sQuery(id+"F0.wireOp",EDGE,"E54.1"),sQuery(id+"F0.wireOp",EDGE,"E54.2"),sQuery(id+"F0.wireOp",EDGE,"E54.3"),sQuery(id+"F0.wireOp",EDGE,"E54.4"),sQuery(id+"F0.wireOp",EDGE,"E54.5"),sQuery(id+"F0.wireOp",EDGE,"E57.trimOffspring"),sQuery(id+"F0.wireOp",EDGE,"E92"),sQuery(id+"F0.wireOp",EDGE,"E93"),sQuery(id+"F0.wireOp",EDGE,"E94"),sQuery(id+"F0.wireOp",EDGE,"E114.0"),sQuery(id+"F0.wireOp",EDGE,"E114.1"),sQuery(id+"F0.wireOp",EDGE,"E114.2"),sQuery(id+"F0.wireOp",EDGE,"E114.3"),sQuery(id+"F0.wireOp",EDGE,"E114.4"),sQuery(id+"F0.wireOp",EDGE,"E114.5"),sQuery(id+"F0.wireOp",EDGE,"E114.6"),sQuery(id+"F0.wireOp",EDGE,"E114.7"),sQuery(id+"F0.wireOp",EDGE,"E114.8"),sQuery(id+"F0.wireOp",EDGE,"E114.9"),sQuery(id+"F0.wireOp",EDGE,"E114.10"),sQuery(id+"F0.wireOp",EDGE,"E114.11"),sQuery(id+"F0.wireOp",EDGE,"E114.12"),sQuery(id+"F0.wireOp",EDGE,"E114.13"),sQuery(id+"F0.wireOp",EDGE,"E114.14"),sQuery(id+"F0.wireOp",EDGE,"E114.15"),sQuery(id+"F0.wireOp",EDGE,"E114.16"),sQuery(id+"F0.wireOp",EDGE,"E115"),sQuery(id+"F0.wireOp",EDGE,"E154"),sQuery(id+"F0.wireOp",EDGE,"E174.0"),sQuery(id+"F0.wireOp",EDGE,"E246.filletArc"),sQuery(id+"F0.wireOp",EDGE,"E248"),subQ1,subQ0,sQuery(id+"F0.wireOp",EDGE,"E291"),sQuery(id+"F0.wireOp",EDGE,"E297"),sQuery(id+"F0.wireOp",EDGE,"E298")])],"isStart":true}),makeQuery(id+"F31.opExtrude","SWEPT_FACE",FACE,{"disambiguationData":[OSD([sQuery(id+"F0.wireOp",EDGE,"E96"),subQ1,subQ0])]})]});}
            var Q9;
            {var subQ0=sQuery(id+"F0.wireOp",EDGE,"E285");var subQ1=sQuery(id+"F0.wireOp",EDGE,"E250");Q9=makeQuery(id+"F35.opPattern","COPY",EDGE,{"derivedFrom":makeQuery(id+"F31.boolean.opBoolean","INTERSECT",EDGE,{"derivedFrom":[makeQuery(id+"F30.opExtrude","CAP_FACE",FACE,{"disambiguationData":[OSD([sQuery(id+"F0.wireOp",EDGE,"E2"),sQuery(id+"F0.wireOp",EDGE,"E28"),sQuery(id+"F0.wireOp",EDGE,"E40.0"),sQuery(id+"F0.wireOp",EDGE,"E40.1"),sQuery(id+"F0.wireOp",EDGE,"E40.2"),sQuery(id+"F0.wireOp",EDGE,"E40.3"),sQuery(id+"F0.wireOp",EDGE,"E40.4"),sQuery(id+"F0.wireOp",EDGE,"E40.5"),sQuery(id+"F0.wireOp",EDGE,"E43.trimOffspring"),sQuery(id+"F0.wireOp",EDGE,"E54.0"),sQuery(id+"F0.wireOp",EDGE,"E54.1"),sQuery(id+"F0.wireOp",EDGE,"E54.2"),sQuery(id+"F0.wireOp",EDGE,"E54.3"),sQuery(id+"F0.wireOp",EDGE,"E54.4"),sQuery(id+"F0.wireOp",EDGE,"E54.5"),sQuery(id+"F0.wireOp",EDGE,"E57.trimOffspring"),sQuery(id+"F0.wireOp",EDGE,"E92"),sQuery(id+"F0.wireOp",EDGE,"E93"),sQuery(id+"F0.wireOp",EDGE,"E94"),sQuery(id+"F0.wireOp",EDGE,"E114.0"),sQuery(id+"F0.wireOp",EDGE,"E114.1"),sQuery(id+"F0.wireOp",EDGE,"E114.2"),sQuery(id+"F0.wireOp",EDGE,"E114.3"),sQuery(id+"F0.wireOp",EDGE,"E114.4"),sQuery(id+"F0.wireOp",EDGE,"E114.5"),sQuery(id+"F0.wireOp",EDGE,"E114.6"),sQuery(id+"F0.wireOp",EDGE,"E114.7"),sQuery(id+"F0.wireOp",EDGE,"E114.8"),sQuery(id+"F0.wireOp",EDGE,"E114.9"),sQuery(id+"F0.wireOp",EDGE,"E114.10"),sQuery(id+"F0.wireOp",EDGE,"E114.11"),sQuery(id+"F0.wireOp",EDGE,"E114.12"),sQuery(id+"F0.wireOp",EDGE,"E114.13"),sQuery(id+"F0.wireOp",EDGE,"E114.14"),sQuery(id+"F0.wireOp",EDGE,"E114.15"),sQuery(id+"F0.wireOp",EDGE,"E114.16"),sQuery(id+"F0.wireOp",EDGE,"E115"),sQuery(id+"F0.wireOp",EDGE,"E154"),sQuery(id+"F0.wireOp",EDGE,"E174.0"),sQuery(id+"F0.wireOp",EDGE,"E246.filletArc"),sQuery(id+"F0.wireOp",EDGE,"E248"),subQ1,subQ0,sQuery(id+"F0.wireOp",EDGE,"E291"),sQuery(id+"F0.wireOp",EDGE,"E297"),sQuery(id+"F0.wireOp",EDGE,"E298")])],"isStart":true}),makeQuery(id+"F31.opExtrude","SWEPT_FACE",FACE,{"disambiguationData":[OSD([sQuery(id+"F0.wireOp",EDGE,"E96"),subQ1,subQ0])]})]}),"instanceName":"1"});}
            var Q10;
            Q10=makeQuery(id+"F34.opPattern","COPY",EDGE,{"derivedFrom":makeQuery(id+"F28.boolean.opBoolean","INTERSECT",EDGE,{"derivedFrom":[makeQuery(id+"F27.opExtrude","CAP_FACE",FACE,{"disambiguationData":[OSD([sQuery(id+"F0.wireOp",EDGE,"E0"),sQuery(id+"F0.wireOp",EDGE,"E3"),sQuery(id+"F0.wireOp",EDGE,"E29"),sQuery(id+"F0.wireOp",EDGE,"E91"),sQuery(id+"F0.wireOp",EDGE,"E95"),sQuery(id+"F0.wireOp",EDGE,"E97"),sQuery(id+"F0.wireOp",EDGE,"E98"),sQuery(id+"F0.wireOp",EDGE,"E99"),sQuery(id+"F0.wireOp",EDGE,"E100"),sQuery(id+"F0.wireOp",EDGE,"E101"),sQuery(id+"F0.wireOp",EDGE,"E102"),sQuery(id+"F0.wireOp",EDGE,"E103"),sQuery(id+"F0.wireOp",EDGE,"E104"),sQuery(id+"F0.wireOp",EDGE,"E105"),sQuery(id+"F0.wireOp",EDGE,"E106"),sQuery(id+"F0.wireOp",EDGE,"E107"),sQuery(id+"F0.wireOp",EDGE,"E108"),sQuery(id+"F0.wireOp",EDGE,"E109"),sQuery(id+"F0.wireOp",EDGE,"E110"),sQuery(id+"F0.wireOp",EDGE,"E111"),sQuery(id+"F0.wireOp",EDGE,"E112"),sQuery(id+"F0.wireOp",EDGE,"E113"),sQuery(id+"F0.wireOp",EDGE,"E185.0"),sQuery(id+"F0.wireOp",EDGE,"E185.1"),sQuery(id+"F0.wireOp",EDGE,"E185.2"),sQuery(id+"F0.wireOp",EDGE,"E185.3"),sQuery(id+"F0.wireOp",EDGE,"E185.4"),sQuery(id+"F0.wireOp",EDGE,"E185.5"),sQuery(id+"F0.wireOp",EDGE,"E188.trimOffspring"),sQuery(id+"F0.wireOp",EDGE,"E201.0"),sQuery(id+"F0.wireOp",EDGE,"E201.1"),sQuery(id+"F0.wireOp",EDGE,"E201.2"),sQuery(id+"F0.wireOp",EDGE,"E201.3"),sQuery(id+"F0.wireOp",EDGE,"E201.4"),sQuery(id+"F0.wireOp",EDGE,"E201.5"),sQuery(id+"F0.wireOp",EDGE,"E204.trimOffspring"),sQuery(id+"F0.wireOp",EDGE,"E244.filletArc")])],"isStart":true}),makeQuery(id+"F28.opExtrude","SWEPT_FACE",FACE,{"disambiguationData":[OSD([sQuery(id+"F0.wireOp",EDGE,"E89.0")])]})]}),"instanceName":"1"});
            var Q11;
            {var subQ0=sQuery(id+"F0.wireOp",EDGE,"E285");var subQ1=sQuery(id+"F0.wireOp",EDGE,"E250");Q11=makeQuery(id+"F37.opPattern","COPY",EDGE,{"derivedFrom":makeQuery(id+"F35.opPattern","COPY",EDGE,{"derivedFrom":makeQuery(id+"F31.boolean.opBoolean","INTERSECT",EDGE,{"derivedFrom":[makeQuery(id+"F30.opExtrude","CAP_FACE",FACE,{"disambiguationData":[OSD([sQuery(id+"F0.wireOp",EDGE,"E2"),sQuery(id+"F0.wireOp",EDGE,"E28"),sQuery(id+"F0.wireOp",EDGE,"E40.0"),sQuery(id+"F0.wireOp",EDGE,"E40.1"),sQuery(id+"F0.wireOp",EDGE,"E40.2"),sQuery(id+"F0.wireOp",EDGE,"E40.3"),sQuery(id+"F0.wireOp",EDGE,"E40.4"),sQuery(id+"F0.wireOp",EDGE,"E40.5"),sQuery(id+"F0.wireOp",EDGE,"E43.trimOffspring"),sQuery(id+"F0.wireOp",EDGE,"E54.0"),sQuery(id+"F0.wireOp",EDGE,"E54.1"),sQuery(id+"F0.wireOp",EDGE,"E54.2"),sQuery(id+"F0.wireOp",EDGE,"E54.3"),sQuery(id+"F0.wireOp",EDGE,"E54.4"),sQuery(id+"F0.wireOp",EDGE,"E54.5"),sQuery(id+"F0.wireOp",EDGE,"E57.trimOffspring"),sQuery(id+"F0.wireOp",EDGE,"E92"),sQuery(id+"F0.wireOp",EDGE,"E93"),sQuery(id+"F0.wireOp",EDGE,"E94"),sQuery(id+"F0.wireOp",EDGE,"E114.0"),sQuery(id+"F0.wireOp",EDGE,"E114.1"),sQuery(id+"F0.wireOp",EDGE,"E114.2"),sQuery(id+"F0.wireOp",EDGE,"E114.3"),sQuery(id+"F0.wireOp",EDGE,"E114.4"),sQuery(id+"F0.wireOp",EDGE,"E114.5"),sQuery(id+"F0.wireOp",EDGE,"E114.6"),sQuery(id+"F0.wireOp",EDGE,"E114.7"),sQuery(id+"F0.wireOp",EDGE,"E114.8"),sQuery(id+"F0.wireOp",EDGE,"E114.9"),sQuery(id+"F0.wireOp",EDGE,"E114.10"),sQuery(id+"F0.wireOp",EDGE,"E114.11"),sQuery(id+"F0.wireOp",EDGE,"E114.12"),sQuery(id+"F0.wireOp",EDGE,"E114.13"),sQuery(id+"F0.wireOp",EDGE,"E114.14"),sQuery(id+"F0.wireOp",EDGE,"E114.15"),sQuery(id+"F0.wireOp",EDGE,"E114.16"),sQuery(id+"F0.wireOp",EDGE,"E115"),sQuery(id+"F0.wireOp",EDGE,"E154"),sQuery(id+"F0.wireOp",EDGE,"E174.0"),sQuery(id+"F0.wireOp",EDGE,"E246.filletArc"),sQuery(id+"F0.wireOp",EDGE,"E248"),subQ1,subQ0,sQuery(id+"F0.wireOp",EDGE,"E291"),sQuery(id+"F0.wireOp",EDGE,"E297"),sQuery(id+"F0.wireOp",EDGE,"E298")])],"isStart":true}),makeQuery(id+"F31.opExtrude","SWEPT_FACE",FACE,{"disambiguationData":[OSD([sQuery(id+"F0.wireOp",EDGE,"E96"),subQ1,subQ0])]})]}),"instanceName":"1"}),"instanceName":"1"});}
            var Q12;
            Q12=makeQuery(id+"F36.opPattern","COPY",EDGE,{"derivedFrom":makeQuery(id+"F34.opPattern","COPY",EDGE,{"derivedFrom":makeQuery(id+"F28.boolean.opBoolean","INTERSECT",EDGE,{"derivedFrom":[makeQuery(id+"F27.opExtrude","CAP_FACE",FACE,{"disambiguationData":[OSD([sQuery(id+"F0.wireOp",EDGE,"E0"),sQuery(id+"F0.wireOp",EDGE,"E3"),sQuery(id+"F0.wireOp",EDGE,"E29"),sQuery(id+"F0.wireOp",EDGE,"E91"),sQuery(id+"F0.wireOp",EDGE,"E95"),sQuery(id+"F0.wireOp",EDGE,"E97"),sQuery(id+"F0.wireOp",EDGE,"E98"),sQuery(id+"F0.wireOp",EDGE,"E99"),sQuery(id+"F0.wireOp",EDGE,"E100"),sQuery(id+"F0.wireOp",EDGE,"E101"),sQuery(id+"F0.wireOp",EDGE,"E102"),sQuery(id+"F0.wireOp",EDGE,"E103"),sQuery(id+"F0.wireOp",EDGE,"E104"),sQuery(id+"F0.wireOp",EDGE,"E105"),sQuery(id+"F0.wireOp",EDGE,"E106"),sQuery(id+"F0.wireOp",EDGE,"E107"),sQuery(id+"F0.wireOp",EDGE,"E108"),sQuery(id+"F0.wireOp",EDGE,"E109"),sQuery(id+"F0.wireOp",EDGE,"E110"),sQuery(id+"F0.wireOp",EDGE,"E111"),sQuery(id+"F0.wireOp",EDGE,"E112"),sQuery(id+"F0.wireOp",EDGE,"E113"),sQuery(id+"F0.wireOp",EDGE,"E185.0"),sQuery(id+"F0.wireOp",EDGE,"E185.1"),sQuery(id+"F0.wireOp",EDGE,"E185.2"),sQuery(id+"F0.wireOp",EDGE,"E185.3"),sQuery(id+"F0.wireOp",EDGE,"E185.4"),sQuery(id+"F0.wireOp",EDGE,"E185.5"),sQuery(id+"F0.wireOp",EDGE,"E188.trimOffspring"),sQuery(id+"F0.wireOp",EDGE,"E201.0"),sQuery(id+"F0.wireOp",EDGE,"E201.1"),sQuery(id+"F0.wireOp",EDGE,"E201.2"),sQuery(id+"F0.wireOp",EDGE,"E201.3"),sQuery(id+"F0.wireOp",EDGE,"E201.4"),sQuery(id+"F0.wireOp",EDGE,"E201.5"),sQuery(id+"F0.wireOp",EDGE,"E204.trimOffspring"),sQuery(id+"F0.wireOp",EDGE,"E244.filletArc")])],"isStart":true}),makeQuery(id+"F28.opExtrude","SWEPT_FACE",FACE,{"disambiguationData":[OSD([sQuery(id+"F0.wireOp",EDGE,"E89.0")])]})]}),"instanceName":"1"}),"instanceName":"1"});
            var Q13;
            {var subQ0=sQuery(id+"F0.wireOp",EDGE,"E297");var subQ1=sQuery(id+"F0.wireOp",EDGE,"E248");Q13=makeQuery(id+"F35.opPattern","COPY",EDGE,{"derivedFrom":makeQuery(id+"F31.boolean.opBoolean","INTERSECT",EDGE,{"derivedFrom":[makeQuery(id+"F30.opExtrude","CAP_FACE",FACE,{"disambiguationData":[OSD([sQuery(id+"F0.wireOp",EDGE,"E2"),sQuery(id+"F0.wireOp",EDGE,"E28"),sQuery(id+"F0.wireOp",EDGE,"E40.0"),sQuery(id+"F0.wireOp",EDGE,"E40.1"),sQuery(id+"F0.wireOp",EDGE,"E40.2"),sQuery(id+"F0.wireOp",EDGE,"E40.3"),sQuery(id+"F0.wireOp",EDGE,"E40.4"),sQuery(id+"F0.wireOp",EDGE,"E40.5"),sQuery(id+"F0.wireOp",EDGE,"E43.trimOffspring"),sQuery(id+"F0.wireOp",EDGE,"E54.0"),sQuery(id+"F0.wireOp",EDGE,"E54.1"),sQuery(id+"F0.wireOp",EDGE,"E54.2"),sQuery(id+"F0.wireOp",EDGE,"E54.3"),sQuery(id+"F0.wireOp",EDGE,"E54.4"),sQuery(id+"F0.wireOp",EDGE,"E54.5"),sQuery(id+"F0.wireOp",EDGE,"E57.trimOffspring"),sQuery(id+"F0.wireOp",EDGE,"E92"),sQuery(id+"F0.wireOp",EDGE,"E93"),sQuery(id+"F0.wireOp",EDGE,"E94"),sQuery(id+"F0.wireOp",EDGE,"E114.0"),sQuery(id+"F0.wireOp",EDGE,"E114.1"),sQuery(id+"F0.wireOp",EDGE,"E114.2"),sQuery(id+"F0.wireOp",EDGE,"E114.3"),sQuery(id+"F0.wireOp",EDGE,"E114.4"),sQuery(id+"F0.wireOp",EDGE,"E114.5"),sQuery(id+"F0.wireOp",EDGE,"E114.6"),sQuery(id+"F0.wireOp",EDGE,"E114.7"),sQuery(id+"F0.wireOp",EDGE,"E114.8"),sQuery(id+"F0.wireOp",EDGE,"E114.9"),sQuery(id+"F0.wireOp",EDGE,"E114.10"),sQuery(id+"F0.wireOp",EDGE,"E114.11"),sQuery(id+"F0.wireOp",EDGE,"E114.12"),sQuery(id+"F0.wireOp",EDGE,"E114.13"),sQuery(id+"F0.wireOp",EDGE,"E114.14"),sQuery(id+"F0.wireOp",EDGE,"E114.15"),sQuery(id+"F0.wireOp",EDGE,"E114.16"),sQuery(id+"F0.wireOp",EDGE,"E115"),sQuery(id+"F0.wireOp",EDGE,"E154"),sQuery(id+"F0.wireOp",EDGE,"E174.0"),sQuery(id+"F0.wireOp",EDGE,"E246.filletArc"),subQ1,sQuery(id+"F0.wireOp",EDGE,"E250"),sQuery(id+"F0.wireOp",EDGE,"E285"),sQuery(id+"F0.wireOp",EDGE,"E291"),subQ0,sQuery(id+"F0.wireOp",EDGE,"E298")])],"isStart":true}),makeQuery(id+"F31.opExtrude","SWEPT_FACE",FACE,{"disambiguationData":[OSD([sQuery(id+"F0.wireOp",EDGE,"E86.0"),subQ1,sQuery(id+"F0.wireOp",EDGE,"E267"),subQ0])]})]}),"instanceName":"1"});}
            var Q14;
            {var subQ0=sQuery(id+"F0.wireOp",EDGE,"E297");var subQ1=sQuery(id+"F0.wireOp",EDGE,"E248");Q14=makeQuery(id+"F37.opPattern","COPY",EDGE,{"derivedFrom":makeQuery(id+"F35.opPattern","COPY",EDGE,{"derivedFrom":makeQuery(id+"F31.boolean.opBoolean","INTERSECT",EDGE,{"derivedFrom":[makeQuery(id+"F30.opExtrude","CAP_FACE",FACE,{"disambiguationData":[OSD([sQuery(id+"F0.wireOp",EDGE,"E2"),sQuery(id+"F0.wireOp",EDGE,"E28"),sQuery(id+"F0.wireOp",EDGE,"E40.0"),sQuery(id+"F0.wireOp",EDGE,"E40.1"),sQuery(id+"F0.wireOp",EDGE,"E40.2"),sQuery(id+"F0.wireOp",EDGE,"E40.3"),sQuery(id+"F0.wireOp",EDGE,"E40.4"),sQuery(id+"F0.wireOp",EDGE,"E40.5"),sQuery(id+"F0.wireOp",EDGE,"E43.trimOffspring"),sQuery(id+"F0.wireOp",EDGE,"E54.0"),sQuery(id+"F0.wireOp",EDGE,"E54.1"),sQuery(id+"F0.wireOp",EDGE,"E54.2"),sQuery(id+"F0.wireOp",EDGE,"E54.3"),sQuery(id+"F0.wireOp",EDGE,"E54.4"),sQuery(id+"F0.wireOp",EDGE,"E54.5"),sQuery(id+"F0.wireOp",EDGE,"E57.trimOffspring"),sQuery(id+"F0.wireOp",EDGE,"E92"),sQuery(id+"F0.wireOp",EDGE,"E93"),sQuery(id+"F0.wireOp",EDGE,"E94"),sQuery(id+"F0.wireOp",EDGE,"E114.0"),sQuery(id+"F0.wireOp",EDGE,"E114.1"),sQuery(id+"F0.wireOp",EDGE,"E114.2"),sQuery(id+"F0.wireOp",EDGE,"E114.3"),sQuery(id+"F0.wireOp",EDGE,"E114.4"),sQuery(id+"F0.wireOp",EDGE,"E114.5"),sQuery(id+"F0.wireOp",EDGE,"E114.6"),sQuery(id+"F0.wireOp",EDGE,"E114.7"),sQuery(id+"F0.wireOp",EDGE,"E114.8"),sQuery(id+"F0.wireOp",EDGE,"E114.9"),sQuery(id+"F0.wireOp",EDGE,"E114.10"),sQuery(id+"F0.wireOp",EDGE,"E114.11"),sQuery(id+"F0.wireOp",EDGE,"E114.12"),sQuery(id+"F0.wireOp",EDGE,"E114.13"),sQuery(id+"F0.wireOp",EDGE,"E114.14"),sQuery(id+"F0.wireOp",EDGE,"E114.15"),sQuery(id+"F0.wireOp",EDGE,"E114.16"),sQuery(id+"F0.wireOp",EDGE,"E115"),sQuery(id+"F0.wireOp",EDGE,"E154"),sQuery(id+"F0.wireOp",EDGE,"E174.0"),sQuery(id+"F0.wireOp",EDGE,"E246.filletArc"),subQ1,sQuery(id+"F0.wireOp",EDGE,"E250"),sQuery(id+"F0.wireOp",EDGE,"E285"),sQuery(id+"F0.wireOp",EDGE,"E291"),subQ0,sQuery(id+"F0.wireOp",EDGE,"E298")])],"isStart":true}),makeQuery(id+"F31.opExtrude","SWEPT_FACE",FACE,{"disambiguationData":[OSD([sQuery(id+"F0.wireOp",EDGE,"E86.0"),subQ1,sQuery(id+"F0.wireOp",EDGE,"E267"),subQ0])]})]}),"instanceName":"1"}),"instanceName":"1"});}
            var Q15;
            Q15=makeQuery(id+"F24.opExtrude","CAP_EDGE",EDGE,{"disambiguationData":[OSD([sQuery(id+"F0.wireOp",EDGE,"E156.trimOffspring"),sQuery(id+"F0.wireOp",EDGE,"E288"),sQuery(id+"F0.wireOp",EDGE,"E296")])],"isStart":true});
            var Q16;
            Q16=makeQuery(id+"F25.opPattern","COPY",EDGE,{"derivedFrom":makeQuery(id+"F24.opExtrude","CAP_EDGE",EDGE,{"disambiguationData":[OSD([sQuery(id+"F0.wireOp",EDGE,"E156.trimOffspring"),sQuery(id+"F0.wireOp",EDGE,"E288"),sQuery(id+"F0.wireOp",EDGE,"E296")])],"isStart":true}),"instanceName":"1"});
            var Q17;
            Q17=makeQuery(id+"F15.opExtrude","CAP_EDGE",EDGE,{"disambiguationData":[OSD([sQuery(id+"F0.wireOp",EDGE,"E280"),sQuery(id+"F0.wireOp",EDGE,"E289"),sQuery(id+"F0.wireOp",EDGE,"E290")])],"isStart":true});
            var Q18;
            Q18=makeQuery(id+"F26.opPattern","COPY",EDGE,{"derivedFrom":makeQuery(id+"F25.opPattern","COPY",EDGE,{"derivedFrom":makeQuery(id+"F24.opExtrude","CAP_EDGE",EDGE,{"disambiguationData":[OSD([sQuery(id+"F0.wireOp",EDGE,"E156.trimOffspring"),sQuery(id+"F0.wireOp",EDGE,"E288"),sQuery(id+"F0.wireOp",EDGE,"E296")])],"isStart":true}),"instanceName":"1"}),"instanceName":"1"});
            var Q19;
            Q19=makeQuery(id+"F20.opExtrude","CAP_EDGE",EDGE,{"disambiguationData":[OSD([sQuery(id+"F0.wireOp",EDGE,"E280"),sQuery(id+"F0.wireOp",EDGE,"E289"),sQuery(id+"F0.wireOp",EDGE,"E290")])],"isStart":true});
            var Q20;
            Q20=makeQuery(id+"F37.opPattern","COPY",EDGE,{"derivedFrom":makeQuery(id+"F35.opPattern","COPY",EDGE,{"derivedFrom":makeQuery(id+"F30.opExtrude","CAP_EDGE",EDGE,{"disambiguationData":[OSD([sQuery(id+"F0.wireOp",EDGE,"E174.0"),sQuery(id+"F0.wireOp",EDGE,"E291"),sQuery(id+"F0.wireOp",EDGE,"E298")])],"isStart":true}),"instanceName":"1"}),"instanceName":"1"});
            var Q21;
            Q21=makeQuery(id+"F35.opPattern","COPY",EDGE,{"derivedFrom":makeQuery(id+"F30.opExtrude","CAP_EDGE",EDGE,{"disambiguationData":[OSD([sQuery(id+"F0.wireOp",EDGE,"E174.0"),sQuery(id+"F0.wireOp",EDGE,"E291"),sQuery(id+"F0.wireOp",EDGE,"E298")])],"isStart":true}),"instanceName":"1"});
            var Q22;
            Q22=makeQuery(id+"F30.opExtrude","CAP_EDGE",EDGE,{"disambiguationData":[OSD([sQuery(id+"F0.wireOp",EDGE,"E174.0"),sQuery(id+"F0.wireOp",EDGE,"E291"),sQuery(id+"F0.wireOp",EDGE,"E298")])],"isStart":true});
            var Q23;
            Q23=makeQuery(id+"F2.opExtrude","CAP_EDGE",EDGE,{"disambiguationData":[OSD([sQuery(id+"F0.wireOp",EDGE,"E86.0"),sQuery(id+"F0.wireOp",EDGE,"E267")])],"isStart":false});
            var Q24;
            Q24=makeQuery(id+"F4.opExtrude","CAP_EDGE",EDGE,{"disambiguationData":[OSD([sQuery(id+"F0.wireOp",EDGE,"E87.0"),sQuery(id+"F0.wireOp",EDGE,"E268")])],"isStart":false});
            var Q25;
            Q25=makeQuery(id+"F4.opExtrude","CAP_EDGE",EDGE,{"disambiguationData":[OSD([sQuery(id+"F0.wireOp",EDGE,"E156.trimOffspring"),sQuery(id+"F0.wireOp",EDGE,"E158.0"),sQuery(id+"F0.wireOp",EDGE,"E243"),sQuery(id+"F0.wireOp",EDGE,"E277"),sQuery(id+"F0.wireOp",EDGE,"E280"),sQuery(id+"F0.wireOp",EDGE,"E288"),sQuery(id+"F0.wireOp",EDGE,"E289"),sQuery(id+"F0.wireOp",EDGE,"E290")])],"isStart":true});
            var Q26;
            Q26=makeQuery(id+"F4.opExtrude","CAP_EDGE",EDGE,{"disambiguationData":[OSD([sQuery(id+"F0.wireOp",EDGE,"E6"),sQuery(id+"F0.wireOp",EDGE,"E8"),sQuery(id+"F0.wireOp",EDGE,"E14")])],"isStart":true});
            var Q27;
            Q27=makeQuery(id+"F2.opExtrude","CAP_EDGE",EDGE,{"disambiguationData":[OSD([sQuery(id+"F0.wireOp",EDGE,"E86.0"),sQuery(id+"F0.wireOp",EDGE,"E267")])],"isStart":true});
            var Q28;
            Q28=makeQuery(id+"F2.opExtrude","CAP_EDGE",EDGE,{"disambiguationData":[OSD([sQuery(id+"F0.wireOp",EDGE,"E2")])],"isStart":true});
            var Q29;
            Q29=makeQuery(id+"F5.opExtrude","CAP_EDGE",EDGE,{"disambiguationData":[OSD([sQuery(id+"F0.wireOp",EDGE,"E24")])],"isStart":true});
            var Q30;
            Q30=makeQuery(id+"F8.boolean.opBoolean","MERGE",EDGE,{"derivedFrom":[makeQuery(id+"F5.opExtrude","CAP_EDGE",EDGE,{"disambiguationData":[OSD([sQuery(id+"F0.wireOp",EDGE,"E25")])],"isStart":true}),makeQuery(id+"F5.opExtrude","CAP_EDGE",EDGE,{"disambiguationData":[OSD([sQuery(id+"F0.wireOp",EDGE,"E42.trimOffspring")])],"isStart":true}),makeQuery(id+"F5.opExtrude","CAP_EDGE",EDGE,{"disambiguationData":[OSD([sQuery(id+"F0.wireOp",EDGE,"E56.trimOffspring")])],"isStart":true}),makeQuery(id+"F8.opExtrude","CAP_EDGE",EDGE,{"disambiguationData":[OSD([sQuery(id+"F7.wireOp",EDGE,"E300")])],"isStart":true}),makeQuery(id+"F8.opExtrude","CAP_EDGE",EDGE,{"disambiguationData":[OSD([sQuery(id+"F7.wireOp",EDGE,"E301")])],"isStart":true})]});
            var Q31;
            Q31=makeQuery(id+"F8.boolean.opBoolean","MERGE",EDGE,{"derivedFrom":[makeQuery(id+"F5.opExtrude","CAP_EDGE",EDGE,{"disambiguationData":[OSD([sQuery(id+"F0.wireOp",EDGE,"E26")])],"isStart":true}),makeQuery(id+"F5.opExtrude","CAP_EDGE",EDGE,{"disambiguationData":[OSD([sQuery(id+"F0.wireOp",EDGE,"E71.trimOffspring")])],"isStart":true}),makeQuery(id+"F5.opExtrude","CAP_EDGE",EDGE,{"disambiguationData":[OSD([sQuery(id+"F0.wireOp",EDGE,"E85.trimOffspring")])],"isStart":true}),makeQuery(id+"F8.opExtrude","CAP_EDGE",EDGE,{"disambiguationData":[OSD([sQuery(id+"F7.wireOp",EDGE,"E302")])],"isStart":true}),makeQuery(id+"F8.opExtrude","CAP_EDGE",EDGE,{"disambiguationData":[OSD([sQuery(id+"F7.wireOp",EDGE,"E303")])],"isStart":true})]});
            var Q32;
            Q32=makeQuery(id+"F5.opExtrude","CAP_EDGE",EDGE,{"disambiguationData":[OSD([sQuery(id+"F0.wireOp",EDGE,"E19")])],"isStart":true});
            var Q33;
            Q33=makeQuery(id+"F6.opExtrude","CAP_EDGE",EDGE,{"disambiguationData":[OSD([sQuery(id+"F0.wireOp",EDGE,"E19")])],"isStart":true});
            fillet(context, id + "F38", {"entities" : qUnion([Q0, Q1, Q2, Q3, Q4, Q5, Q6, Q7, Q8, Q9, Q10, Q11, Q12, Q13, Q14, Q15, Q16, Q17, Q18, Q19, Q20, Q21, Q22, Q23, Q24, Q25, Q26, Q27, Q28, Q29, Q30, Q31, Q32, Q33]), "radius" : 2 * mm, "tangentPropagation" : true, "allowEdgeOverflow" : false});
        }
    });
